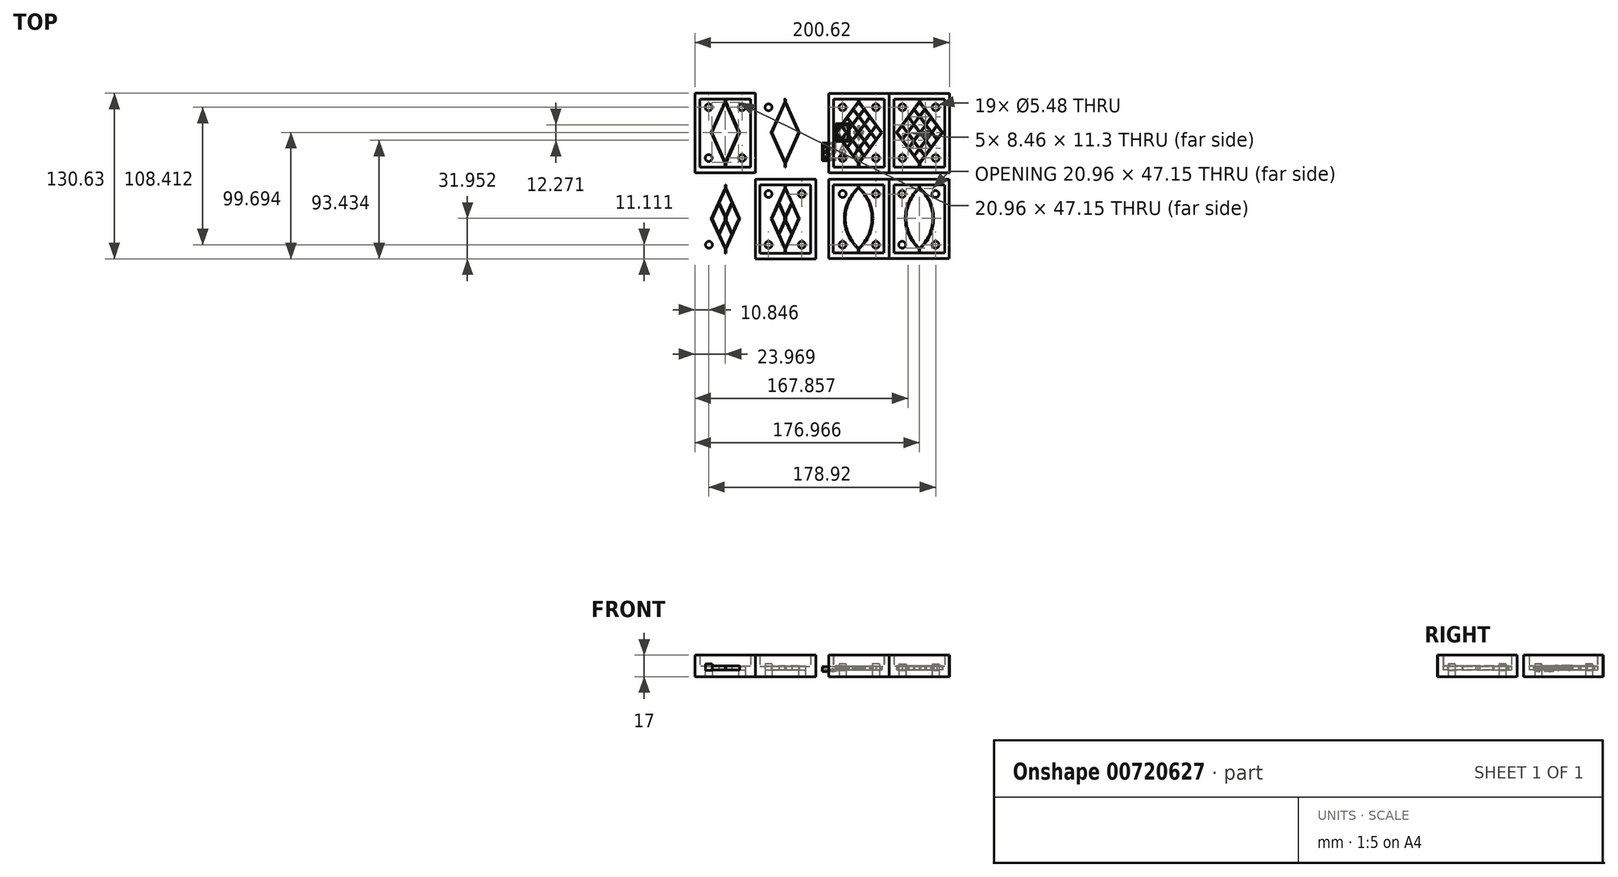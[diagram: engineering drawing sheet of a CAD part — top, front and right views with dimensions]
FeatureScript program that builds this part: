
annotation { "Feature Type Name" : "Feature", "Feature Type Description" : "" }
export const myFeature = defineFeature(function(context is Context, id is Id, definition is map)
    precondition{}
    {
        {
            var Q0;
            Q0=qCreatedBy(makeId("Top.planeOp"),FACE);
            var sketch = newSketch(context, id + "F0", { "sketchPlane" : qUnion([Q0])});
            skLineSegment(sketch, "E0.bottom", {"start": v(-19.96, 26.4) * mm, "end": v(20.09, 26.4) * mm});
            skLineSegment(sketch, "E0.top", {"start": v(-19.96, -27.38) * mm, "end": v(20.09, -27.38) * mm});
            skLineSegment(sketch, "E0.left", {"start": v(-19.96, 26.4) * mm, "end": v(-19.96, -27.38) * mm});
            skLineSegment(sketch, "E0.right", {"start": v(20.09, 26.4) * mm, "end": v(20.09, -27.38) * mm});
            skLineSegment(sketch, "E1.bottom", {"start": v(-23.57, 30.94) * mm, "end": v(23.97, 30.94) * mm});
            skLineSegment(sketch, "E1.top", {"start": v(-23.57, -31.82) * mm, "end": v(23.97, -31.82) * mm});
            skLineSegment(sketch, "E1.left", {"start": v(-23.57, 30.94) * mm, "end": v(-23.57, -31.82) * mm});
            skLineSegment(sketch, "E1.right", {"start": v(23.97, 30.94) * mm, "end": v(23.97, -31.82) * mm});
            skPoint(sketch, "E2.startSnap0", {"position": v(-19.96, -0.48) * mm});
            skLineSegment(sketch, "E3", {"start": v(-13.42, 5.65) * mm, "end": v(-9.19, 11.3) * mm});
            skLineSegment(sketch, "E4", {"start": v(-9.19, 11.3) * mm, "end": v(-5.32, 6.14) * mm});
            skLineSegment(sketch, "E5", {"start": v(-5.32, 6.14) * mm, "end": v(-9.55, 0.48) * mm});
            skLineSegment(sketch, "E6", {"start": v(-17.65, 0) * mm, "end": v(-13.78, 5.17) * mm});
            skLineSegment(sketch, "E7", {"start": v(0, 23.57) * mm, "end": v(-3.87, 18.4) * mm});
            skLineSegment(sketch, "E8", {"start": v(-4.23, 17.92) * mm, "end": v(-8.83, 11.79) * mm});
            skLineSegment(sketch, "E9", {"start": v(-13.78, -5.17) * mm, "end": v(-9.92, 0) * mm});
            skPoint(sketch, "E10.endSnap0", {"position": v(-4.96, 6.62) * mm});
            skLineSegment(sketch, "E11", {"start": v(0, 13.24) * mm, "end": v(3.87, 18.4) * mm});
            skLineSegment(sketch, "E12", {"start": v(-4.96, 6.62) * mm, "end": v(-0.36, 12.76) * mm});
            skLineSegment(sketch, "E13", {"start": v(-13.42, -5.65) * mm, "end": v(-9.55, -0.48) * mm});
            skLineSegment(sketch, "E14", {"start": v(-9.55, -0.48) * mm, "end": v(-5.32, -6.14) * mm});
            skLineSegment(sketch, "E15", {"start": v(-5.32, -6.14) * mm, "end": v(-9.19, -11.3) * mm});
            skLineSegment(sketch, "E16", {"start": v(-9.19, -11.3) * mm, "end": v(-13.42, -5.65) * mm});
            skLineSegment(sketch, "E17", {"start": v(-4.96, -5.65) * mm, "end": v(-0.73, 0) * mm});
            skLineSegment(sketch, "E18", {"start": v(-0.73, 0) * mm, "end": v(-4.96, 5.65) * mm});
            skLineSegment(sketch, "E19", {"start": v(-4.96, 5.65) * mm, "end": v(-9.19, 0) * mm});
            skLineSegment(sketch, "E20", {"start": v(-9.19, 0) * mm, "end": v(-4.96, -5.65) * mm});
            skLineSegment(sketch, "E21", {"start": v(4.23, 6.62) * mm, "end": v(0, 12.27) * mm});
            skLineSegment(sketch, "E22", {"start": v(0, 12.27) * mm, "end": v(-4.6, 6.14) * mm});
            skLineSegment(sketch, "E23", {"start": v(-4.6, 6.14) * mm, "end": v(-0.36, 0.48) * mm});
            skLineSegment(sketch, "E24", {"start": v(-0.36, 0.48) * mm, "end": v(4.23, 6.62) * mm});
            skLineSegment(sketch, "E25", {"start": v(4.6, 7.1) * mm, "end": v(8.46, 12.27) * mm});
            skLineSegment(sketch, "E26", {"start": v(8.46, 12.27) * mm, "end": v(4.23, 17.92) * mm});
            skLineSegment(sketch, "E27", {"start": v(4.23, 17.92) * mm, "end": v(0.36, 12.76) * mm});
            skLineSegment(sketch, "E28", {"start": v(0.36, 12.76) * mm, "end": v(4.6, 7.1) * mm});
            skLineSegment(sketch, "E29", {"start": v(-4.23, -17.92) * mm, "end": v(-0.36, -12.76) * mm});
            skLineSegment(sketch, "E30", {"start": v(-0.36, -12.76) * mm, "end": v(-4.96, -6.62) * mm});
            skLineSegment(sketch, "E31", {"start": v(-8.83, -11.79) * mm, "end": v(-4.96, -6.62) * mm});
            skLineSegment(sketch, "E32", {"start": v(-8.83, -11.79) * mm, "end": v(-4.23, -17.92) * mm});
            skLineSegment(sketch, "E33", {"start": v(0, -12.27) * mm, "end": v(-4.6, -6.14) * mm});
            skLineSegment(sketch, "E34", {"start": v(-0.36, -0.48) * mm, "end": v(-4.6, -6.14) * mm});
            skLineSegment(sketch, "E35", {"start": v(4.23, -6.62) * mm, "end": v(-0.36, -0.48) * mm});
            skLineSegment(sketch, "E36", {"start": v(4.23, -6.62) * mm, "end": v(0, -12.27) * mm});
            skLineSegment(sketch, "E37", {"start": v(9.19, 0) * mm, "end": v(4.6, 6.14) * mm});
            skLineSegment(sketch, "E38", {"start": v(4.6, 6.14) * mm, "end": v(0, 0) * mm});
            skLineSegment(sketch, "E39", {"start": v(0, 0) * mm, "end": v(4.6, -6.14) * mm});
            skLineSegment(sketch, "E40", {"start": v(4.6, -6.14) * mm, "end": v(9.19, 0) * mm});
            skLineSegment(sketch, "E41", {"start": v(4.96, 6.62) * mm, "end": v(8.83, 11.79) * mm});
            skLineSegment(sketch, "E42", {"start": v(8.83, 11.79) * mm, "end": v(13.42, 5.65) * mm});
            skLineSegment(sketch, "E43", {"start": v(13.42, 5.65) * mm, "end": v(9.55, 0.48) * mm});
            skLineSegment(sketch, "E44", {"start": v(9.55, 0.48) * mm, "end": v(4.96, 6.62) * mm});
            skLineSegment(sketch, "E45", {"start": v(-3.87, -18.4) * mm, "end": v(0, -13.24) * mm});
            skLineSegment(sketch, "E46", {"start": v(0, -13.24) * mm, "end": v(3.87, -18.4) * mm});
            skLineSegment(sketch, "E47", {"start": v(3.87, -18.4) * mm, "end": v(0, -23.57) * mm});
            skLineSegment(sketch, "E48", {"start": v(0, -23.57) * mm, "end": v(-3.87, -18.4) * mm});
            skLineSegment(sketch, "E49", {"start": v(4.23, -17.92) * mm, "end": v(8.46, -12.27) * mm});
            skLineSegment(sketch, "E50", {"start": v(8.46, -12.27) * mm, "end": v(4.6, -7.1) * mm});
            skLineSegment(sketch, "E51", {"start": v(4.6, -7.1) * mm, "end": v(0.36, -12.76) * mm});
            skLineSegment(sketch, "E52", {"start": v(0.36, -12.76) * mm, "end": v(4.23, -17.92) * mm});
            skLineSegment(sketch, "E53", {"start": v(8.83, -11.79) * mm, "end": v(4.96, -6.62) * mm});
            skLineSegment(sketch, "E54", {"start": v(4.96, -6.62) * mm, "end": v(9.55, -0.48) * mm});
            skLineSegment(sketch, "E55", {"start": v(9.55, -0.48) * mm, "end": v(13.42, -5.65) * mm});
            skLineSegment(sketch, "E56", {"start": v(13.42, -5.65) * mm, "end": v(8.83, -11.79) * mm});
            skLineSegment(sketch, "E57", {"start": v(17.65, 0) * mm, "end": v(13.78, 5.17) * mm});
            skLineSegment(sketch, "E58", {"start": v(13.78, 5.17) * mm, "end": v(9.92, 0) * mm});
            skLineSegment(sketch, "E59", {"start": v(9.92, 0) * mm, "end": v(13.78, -5.17) * mm});
            skLineSegment(sketch, "E60", {"start": v(13.78, -5.17) * mm, "end": v(17.65, 0) * mm});
            skLineSegment(sketch, "E61", {"start": v(0, 13.24) * mm, "end": v(-3.87, 18.4) * mm});
            skLineSegment(sketch, "E62", {"start": v(3.87, 18.4) * mm, "end": v(0, 23.57) * mm});
            skLineSegment(sketch, "E63", {"start": v(-0.36, 12.76) * mm, "end": v(-4.23, 17.92) * mm});
            skLineSegment(sketch, "E64", {"start": v(-13.78, -5.17) * mm, "end": v(-17.65, 0) * mm});
            skLineSegment(sketch, "E65", {"start": v(-9.92, 0) * mm, "end": v(-13.78, 5.17) * mm});
            skLineSegment(sketch, "E66", {"start": v(-9.55, 0.48) * mm, "end": v(-13.42, 5.65) * mm});
            skLineSegment(sketch, "E67", {"start": v(-4.96, 6.62) * mm, "end": v(-8.83, 11.79) * mm});
            skLineSegment(sketch, "E68", {"start": v(0.36, 24.06) * mm, "end": v(18.38, 0) * mm});
            skLineSegment(sketch, "E69", {"start": v(-18.38, 0) * mm, "end": v(-0.36, 24.06) * mm});
            skLineSegment(sketch, "E70.MirrorCS", {"start": v(-18.38, 0) * mm, "end": v(-0.36, -24.06) * mm});
            skLineSegment(sketch, "E71.MirrorCS", {"start": v(0.36, -24.06) * mm, "end": v(18.38, 0) * mm});
            skLineSegment(sketch, "E72", {"start": v(-0.36, -24.06) * mm, "end": v(-0.36, -27.38) * mm});
            skLineSegment(sketch, "E73", {"start": v(0.36, -24.06) * mm, "end": v(0.36, -27.38) * mm});
            skLineSegment(sketch, "E74", {"start": v(-0.36, 24.06) * mm, "end": v(-0.36, 26.4) * mm});
            skLineSegment(sketch, "E75", {"start": v(0.36, 24.06) * mm, "end": v(0.36, 26.4) * mm});
            skLineSegment(sketch, "E76.bottom", {"start": v(-77.96, 26.53) * mm, "end": v(-37.9, 26.53) * mm});
            skLineSegment(sketch, "E76.top", {"start": v(-77.96, -27.25) * mm, "end": v(-37.9, -27.25) * mm});
            skLineSegment(sketch, "E76.left", {"start": v(-77.96, 26.53) * mm, "end": v(-77.96, -27.25) * mm});
            skLineSegment(sketch, "E76.right", {"start": v(-37.9, 26.53) * mm, "end": v(-37.9, -27.25) * mm});
            skLineSegment(sketch, "E77.bottom", {"start": v(-81.56, 31.06) * mm, "end": v(-34.02, 31.06) * mm});
            skLineSegment(sketch, "E77.top", {"start": v(-81.56, -31.7) * mm, "end": v(-34.02, -31.7) * mm});
            skLineSegment(sketch, "E77.left", {"start": v(-81.56, 31.06) * mm, "end": v(-81.56, -31.7) * mm});
            skLineSegment(sketch, "E77.right", {"start": v(-34.02, 31.06) * mm, "end": v(-34.02, -31.7) * mm});
            skPoint(sketch, "E78.startSnap0", {"position": v(-77.96, -0.36) * mm});
            skLineSegment(sketch, "E79.MirrorCS", {"start": v(-69.2, -0.05) * mm, "end": v(-58.36, -23.93) * mm});
            skLineSegment(sketch, "E80", {"start": v(-58.36, -23.93) * mm, "end": v(-58.36, -27.25) * mm});
            skLineSegment(sketch, "E81", {"start": v(-57.63, -23.93) * mm, "end": v(-57.63, -27.25) * mm});
            skLineSegment(sketch, "E82", {"start": v(-58.36, 24.18) * mm, "end": v(-58.36, 26.53) * mm});
            skLineSegment(sketch, "E83", {"start": v(-57.63, 24.18) * mm, "end": v(-57.63, 26.53) * mm});
            skCircle(sketch, "E84", {"center": v(-71.12, 19.95) * mm, "radius": 2.74 * mm});
            skLineSegment(sketch, "E85", {"start": v(-69.2, -0.05) * mm, "end": v(-58.36, 24.18) * mm});
            skLineSegment(sketch, "E86.MirrorCS", {"start": v(-46.79, -0.05) * mm, "end": v(-57.63, 24.18) * mm});
            skLineSegment(sketch, "E87.MirrorCS", {"start": v(-47.52, -0.05) * mm, "end": v(-58, 23.7) * mm});
            skLineSegment(sketch, "E88.MirrorCS", {"start": v(-46.79, -0.05) * mm, "end": v(-57.63, -23.93) * mm});
            skLineSegment(sketch, "E89.MirrorCS", {"start": v(-47.52, -0.05) * mm, "end": v(-58, -23.45) * mm});
            skLineSegment(sketch, "E90.MirrorCS", {"start": v(-68.47, -0.05) * mm, "end": v(-58, 23.7) * mm});
            skLineSegment(sketch, "E91.MirrorCS", {"start": v(-68.47, -0.05) * mm, "end": v(-58, -23.45) * mm});
            skLineSegment(sketch, "E92.bottom", {"start": v(-77.85, -41.34) * mm, "end": v(-37.8, -41.34) * mm});
            skLineSegment(sketch, "E92.top", {"start": v(-77.85, -95.12) * mm, "end": v(-37.8, -95.12) * mm});
            skLineSegment(sketch, "E92.left", {"start": v(-77.85, -41.34) * mm, "end": v(-77.85, -95.12) * mm});
            skLineSegment(sketch, "E92.right", {"start": v(-37.8, -41.34) * mm, "end": v(-37.8, -95.12) * mm});
            skLineSegment(sketch, "E93.bottom", {"start": v(-81.46, -36.8) * mm, "end": v(-33.91, -36.8) * mm});
            skLineSegment(sketch, "E93.top", {"start": v(-81.46, -99.57) * mm, "end": v(-33.91, -99.57) * mm});
            skLineSegment(sketch, "E93.left", {"start": v(-81.46, -36.8) * mm, "end": v(-81.46, -99.57) * mm});
            skLineSegment(sketch, "E93.right", {"start": v(-33.91, -36.8) * mm, "end": v(-33.91, -99.57) * mm});
            skPoint(sketch, "E94.startSnap0", {"position": v(-77.85, -68.23) * mm});
            skLineSegment(sketch, "E95.MirrorCS", {"start": v(-69.1, -67.93) * mm, "end": v(-58.25, -91.8) * mm});
            skLineSegment(sketch, "E96", {"start": v(-58.25, -91.8) * mm, "end": v(-58.25, -95.12) * mm});
            skLineSegment(sketch, "E97", {"start": v(-57.52, -91.8) * mm, "end": v(-57.52, -95.12) * mm});
            skLineSegment(sketch, "E98", {"start": v(-58.25, -43.69) * mm, "end": v(-58.25, -41.34) * mm});
            skLineSegment(sketch, "E99", {"start": v(-57.52, -43.69) * mm, "end": v(-57.52, -41.34) * mm});
            skLineSegment(sketch, "E100", {"start": v(-69.1, -67.93) * mm, "end": v(-58.25, -43.69) * mm});
            skLineSegment(sketch, "E101.MirrorCS", {"start": v(-46.68, -67.93) * mm, "end": v(-57.52, -43.69) * mm});
            skLineSegment(sketch, "E102.MirrorCS", {"start": v(-46.68, -67.93) * mm, "end": v(-57.52, -91.8) * mm});
            skLineSegment(sketch, "E103", {"start": v(-57.89, -66.3) * mm, "end": v(-52.97, -55.31) * mm});
            skLineSegment(sketch, "E104", {"start": v(-57.89, -66.3) * mm, "end": v(-62.8, -55.31) * mm});
            skLineSegment(sketch, "E105", {"start": v(-52.65, -56.05) * mm, "end": v(-47.4, -67.93) * mm});
            skLineSegment(sketch, "E106", {"start": v(-63.13, -56.05) * mm, "end": v(-68.37, -67.93) * mm});
            skLineSegment(sketch, "E107", {"start": v(-57.89, -91.32) * mm, "end": v(-62.8, -80.35) * mm});
            skLineSegment(sketch, "E108", {"start": v(-62.8, -80.35) * mm, "end": v(-57.89, -69.52) * mm});
            skLineSegment(sketch, "E109", {"start": v(-57.89, -69.52) * mm, "end": v(-52.97, -80.35) * mm});
            skLineSegment(sketch, "E110", {"start": v(-52.97, -80.35) * mm, "end": v(-58, -91.59) * mm});
            skLineSegment(sketch, "E111", {"start": v(-68.37, -67.93) * mm, "end": v(-63.13, -79.62) * mm});
            skLineSegment(sketch, "E112", {"start": v(-52.65, -79.62) * mm, "end": v(-47.4, -67.93) * mm});
            skLineSegment(sketch, "E113.left", {"start": v(-57.2, -66.3) * mm, "end": v(-57.2, -69.37) * mm});
            skLineSegment(sketch, "E113.right", {"start": v(-58.57, -66.3) * mm, "end": v(-58.57, -69.37) * mm});
            skLineSegment(sketch, "E114", {"start": v(-63.13, -56.05) * mm, "end": v(-58.57, -66.3) * mm});
            skLineSegment(sketch, "E115", {"start": v(-57.2, -66.3) * mm, "end": v(-52.65, -56.05) * mm});
            skLineSegment(sketch, "E116", {"start": v(-57.2, -69.37) * mm, "end": v(-52.65, -79.62) * mm});
            skLineSegment(sketch, "E117", {"start": v(-58.57, -69.37) * mm, "end": v(-63.13, -79.62) * mm});
            skLineSegment(sketch, "E118.bottom", {"start": v(-20.04, -41.21) * mm, "end": v(20, -41.21) * mm});
            skLineSegment(sketch, "E118.top", {"start": v(-20.04, -95) * mm, "end": v(20, -95) * mm});
            skLineSegment(sketch, "E118.left", {"start": v(-20.04, -41.21) * mm, "end": v(-20.04, -95) * mm});
            skLineSegment(sketch, "E118.right", {"start": v(20, -41.21) * mm, "end": v(20, -95) * mm});
            skLineSegment(sketch, "E119.bottom", {"start": v(-23.65, -36.68) * mm, "end": v(23.9, -36.68) * mm});
            skLineSegment(sketch, "E119.top", {"start": v(-23.65, -99.44) * mm, "end": v(23.9, -99.44) * mm});
            skLineSegment(sketch, "E119.left", {"start": v(-23.65, -36.68) * mm, "end": v(-23.65, -99.44) * mm});
            skLineSegment(sketch, "E119.right", {"start": v(23.9, -36.68) * mm, "end": v(23.9, -99.44) * mm});
            skPoint(sketch, "E120.startSnap0", {"position": v(-20.04, -68.1) * mm});
            skLineSegment(sketch, "E121", {"start": v(-0.44, -91.68) * mm, "end": v(-0.44, -95) * mm});
            skLineSegment(sketch, "E122", {"start": v(0.28, -91.68) * mm, "end": v(0.28, -95) * mm});
            skLineSegment(sketch, "E123", {"start": v(-0.44, -43.56) * mm, "end": v(-0.44, -41.21) * mm});
            skLineSegment(sketch, "E124", {"start": v(0.28, -43.56) * mm, "end": v(0.28, -41.21) * mm});
            skArc(sketch, "E125", {"start": v(-0.44, -43.56) * mm, "mid": v(-11.29, -67.62) * mm, "end": v(-0.44, -91.68) * mm});
            skArc(sketch, "E126", {"start": v(-0.08, -44.04) * mm, "mid": v(-10.56, -67.62) * mm, "end": v(-0.08, -91.2) * mm});
            skArc(sketch, "E127", {"start": v(0.28, -91.68) * mm, "mid": v(11.12, -67.62) * mm, "end": v(0.28, -43.56) * mm});
            skArc(sketch, "E128", {"start": v(-0.08, -91.2) * mm, "mid": v(10.4, -67.62) * mm, "end": v(-0.08, -44.04) * mm});
            skCircle(sketch, "E129.MirrorC", {"center": v(-44.87, 19.95) * mm, "radius": 2.74 * mm});
            skCircle(sketch, "E130.MirrorC", {"center": v(-71.12, -20.06) * mm, "radius": 2.74 * mm});
            skCircle(sketch, "E131.MirrorC", {"center": v(-44.87, -20.06) * mm, "radius": 2.74 * mm});
            skCircle(sketch, "E132.MirrorC", {"center": v(-12.72, 19.95) * mm, "radius": 2.74 * mm});
            skCircle(sketch, "E133.MirrorC", {"center": v(-12.72, -20.06) * mm, "radius": 2.74 * mm});
            skCircle(sketch, "E134.MirrorC", {"center": v(13.53, -20.06) * mm, "radius": 2.74 * mm});
            skCircle(sketch, "E135.MirrorC", {"center": v(13.53, 19.95) * mm, "radius": 2.74 * mm});
            skCircle(sketch, "E136.MirrorC", {"center": v(-44.87, -48.45) * mm, "radius": 2.74 * mm});
            skCircle(sketch, "E137.MirrorC", {"center": v(-71.12, -48.45) * mm, "radius": 2.74 * mm});
            skCircle(sketch, "E138.MirrorC", {"center": v(-71.12, -88.46) * mm, "radius": 2.74 * mm});
            skCircle(sketch, "E139.MirrorC", {"center": v(-44.87, -88.46) * mm, "radius": 2.74 * mm});
            skCircle(sketch, "E140.MirrorC", {"center": v(-12.72, -48.45) * mm, "radius": 2.74 * mm});
            skCircle(sketch, "E141.MirrorC", {"center": v(13.53, -48.45) * mm, "radius": 2.74 * mm});
            skCircle(sketch, "E142.MirrorC", {"center": v(13.53, -88.46) * mm, "radius": 2.74 * mm});
            skCircle(sketch, "E143.MirrorC", {"center": v(-12.72, -88.46) * mm, "radius": 2.74 * mm});
            skLineSegment(sketch, "E144", {"start": v(-57.89, -44.49) * mm, "end": v(-52.97, -55.31) * mm});
            skLineSegment(sketch, "E145", {"start": v(-57.89, -44.49) * mm, "end": v(-62.8, -55.31) * mm});
            skSolve(sketch);
        }
        {
            var Q0;
            Q0=makeQuery(id+"F0.imprint","IMPRINT",FACE,{"disambiguationData":[TD([[makeQuery(id+"F0.imprint","IMPRINT",EDGE,{"derivedFrom":sQuery(id+"F0.wireOp",EDGE,"E3")}),1.0]])]});
            var Q1;
            Q1=makeQuery(id+"F0.imprint","IMPRINT",FACE,{"disambiguationData":[TD([[makeQuery(id+"F0.imprint","IMPRINT",EDGE,{"derivedFrom":sQuery(id+"F0.wireOp",EDGE,"E79.MirrorCS")}),1.0]])]});
            var Q2;
            {var subQ1=sQuery(id+"F0.wireOp",EDGE,"E121");Q2=makeQuery(id+"F0.imprint","IMPRINT",FACE,{"disambiguationData":[TD([[makeQuery(id+"F0.imprint","IMPRINT",EDGE,{"derivedFrom":subQ1}),1.0]])]});}
            var Q3;
            Q3=makeQuery(id+"F0.imprint","IMPRINT",FACE,{"disambiguationData":[TD([[makeQuery(id+"F0.imprint","IMPRINT",EDGE,{"derivedFrom":sQuery(id+"F0.wireOp",EDGE,"E95.MirrorCS")}),1.0]])]});
            extrude(context, id + "F1", {"entities" : qUnion([Q0, Q1, Q2, Q3]), "depth" : .3 * mm, "offsetDistance" : 25 * mm});
        }
        {
            var Q0;
            Q0=makeQuery(id+"F0.imprint","IMPRINT",FACE,{"disambiguationData":[TD([[makeQuery(id+"F0.imprint","IMPRINT",EDGE,{"derivedFrom":sQuery(id+"F0.wireOp",EDGE,"E0.bottom")}),1.0]])]});
            var Q1;
            Q1=makeQuery(id+"F0.imprint","IMPRINT",FACE,{"disambiguationData":[TD([[makeQuery(id+"F0.imprint","IMPRINT",EDGE,{"derivedFrom":sQuery(id+"F0.wireOp",EDGE,"W2vNM0GE-2OHP-QNdi-PDCA-W7E0gAEi5RRH")}),1.0]])]});
            var Q2;
            Q2=makeQuery(id+"F0.imprint","IMPRINT",FACE,{"disambiguationData":[TD([[makeQuery(id+"F0.imprint","IMPRINT",EDGE,{"derivedFrom":sQuery(id+"F0.wireOp",EDGE,"edaaeaec-2fa2-4ac8-96e5-24b6cc5294a60.MirrorC")}),-1.0]])]});
            var Q3;
            Q3=makeQuery(id+"F0.imprint","IMPRINT",FACE,{"disambiguationData":[TD([[makeQuery(id+"F0.imprint","IMPRINT",EDGE,{"derivedFrom":sQuery(id+"F0.wireOp",EDGE,"8cd1bf5f-9e5d-4626-ba93-0b63d8eae1ea0.MirrorC")}),-1.0]])]});
            var Q4;
            Q4=makeQuery(id+"F0.imprint","IMPRINT",FACE,{"disambiguationData":[TD([[makeQuery(id+"F0.imprint","IMPRINT",EDGE,{"derivedFrom":sQuery(id+"F0.wireOp",EDGE,"899422d1-b2af-4982-8523-cbcbc75a0b1b.MirrorC")}),-1.0]])]});
            var Q5;
            {var subQ1=sQuery(id+"F0.wireOp",EDGE,"E76.left");Q5=makeQuery(id+"F0.imprint","IMPRINT",FACE,{"disambiguationData":[TD([[makeQuery(id+"F0.imprint","IMPRINT",EDGE,{"derivedFrom":subQ1}),-1.0]])]});}
            var Q6;
            Q6=makeQuery(id+"F0.imprint","IMPRINT",FACE,{"disambiguationData":[TD([[makeQuery(id+"F0.imprint","IMPRINT",EDGE,{"derivedFrom":sQuery(id+"F0.wireOp",EDGE,"79d72fee-5c57-43ab-89ce-cfacb674b62a")}),1.0]])]});
            var Q7;
            Q7=makeQuery(id+"F0.imprint","IMPRINT",FACE,{"disambiguationData":[TD([[makeQuery(id+"F0.imprint","IMPRINT",EDGE,{"derivedFrom":sQuery(id+"F0.wireOp",EDGE,"ed612093-3e78-479f-b3c7-dd08aea9376b.MirrorC")}),-1.0]])]});
            var Q8;
            {var subQ1=sQuery(id+"F0.wireOp",EDGE,"E92.left");Q8=makeQuery(id+"F0.imprint","IMPRINT",FACE,{"disambiguationData":[TD([[makeQuery(id+"F0.imprint","IMPRINT",EDGE,{"derivedFrom":subQ1}),-1.0]])]});}
            var Q9;
            {var subQ1=sQuery(id+"F0.wireOp",EDGE,"E118.left");Q9=makeQuery(id+"F0.imprint","IMPRINT",FACE,{"disambiguationData":[TD([[makeQuery(id+"F0.imprint","IMPRINT",EDGE,{"derivedFrom":subQ1}),-1.0]])]});}
            var Q10;
            Q10=makeQuery(id+"F0.imprint","IMPRINT",FACE,{"disambiguationData":[TD([[makeQuery(id+"F0.imprint","IMPRINT",EDGE,{"derivedFrom":sQuery(id+"F0.wireOp",EDGE,"052349c2-b7bf-4fa4-ab4a-60abaacbaca7")}),1.0]])]});
            var Q11;
            Q11=makeQuery(id+"F0.imprint","IMPRINT",FACE,{"disambiguationData":[TD([[makeQuery(id+"F0.imprint","IMPRINT",EDGE,{"derivedFrom":sQuery(id+"F0.wireOp",EDGE,"c45039b2-2c3b-486d-bf61-685492c25083.MirrorC")}),-1.0]])]});
            extrude(context, id + "F2", {"entities" : qUnion([Q0, Q1, Q2, Q3, Q4, Q5, Q6, Q7, Q8, Q9, Q10, Q11]), "depth" : 12 * mm, "offsetDistance" : 25 * mm});
        }
        {
            var Q0;
            {var subQ0=sQuery(id+"F0.wireOp",EDGE,"E0.left");Q0=makeQuery(id+"F0.imprint","IMPRINT",FACE,{"disambiguationData":[TD([[makeQuery(id+"F0.imprint","IMPRINT",EDGE,{"derivedFrom":subQ0}),1.0]])]});}
            var Q1;
            {var subQ0=sQuery(id+"F0.wireOp",EDGE,"E0.right");Q1=makeQuery(id+"F0.imprint","IMPRINT",FACE,{"disambiguationData":[TD([[makeQuery(id+"F0.imprint","IMPRINT",EDGE,{"derivedFrom":subQ0}),-1.0]])]});}
            var Q2;
            Q2=makeQuery(id+"F1.opExtrude","CAP_FACE",FACE,{"disambiguationData":[OSD([sQuery(id+"F0.wireOp",EDGE,"E0.bottom"),sQuery(id+"F0.wireOp",EDGE,"E0.top"),sQuery(id+"F0.wireOp",EDGE,"E3"),sQuery(id+"F0.wireOp",EDGE,"E4"),sQuery(id+"F0.wireOp",EDGE,"E5"),sQuery(id+"F0.wireOp",EDGE,"E6"),sQuery(id+"F0.wireOp",EDGE,"E7"),sQuery(id+"F0.wireOp",EDGE,"E8"),sQuery(id+"F0.wireOp",EDGE,"E9"),sQuery(id+"F0.wireOp",EDGE,"E11"),sQuery(id+"F0.wireOp",EDGE,"E12"),sQuery(id+"F0.wireOp",EDGE,"E13"),sQuery(id+"F0.wireOp",EDGE,"E14"),sQuery(id+"F0.wireOp",EDGE,"E15"),sQuery(id+"F0.wireOp",EDGE,"E16"),sQuery(id+"F0.wireOp",EDGE,"E17"),sQuery(id+"F0.wireOp",EDGE,"E18"),sQuery(id+"F0.wireOp",EDGE,"E19"),sQuery(id+"F0.wireOp",EDGE,"E20"),sQuery(id+"F0.wireOp",EDGE,"E21"),sQuery(id+"F0.wireOp",EDGE,"E22"),sQuery(id+"F0.wireOp",EDGE,"E23"),sQuery(id+"F0.wireOp",EDGE,"E24"),sQuery(id+"F0.wireOp",EDGE,"E25"),sQuery(id+"F0.wireOp",EDGE,"E26"),sQuery(id+"F0.wireOp",EDGE,"E27"),sQuery(id+"F0.wireOp",EDGE,"E28"),sQuery(id+"F0.wireOp",EDGE,"E29"),sQuery(id+"F0.wireOp",EDGE,"E30"),sQuery(id+"F0.wireOp",EDGE,"E31"),sQuery(id+"F0.wireOp",EDGE,"E32"),sQuery(id+"F0.wireOp",EDGE,"E33"),sQuery(id+"F0.wireOp",EDGE,"E34"),sQuery(id+"F0.wireOp",EDGE,"E35"),sQuery(id+"F0.wireOp",EDGE,"E36"),sQuery(id+"F0.wireOp",EDGE,"E37"),sQuery(id+"F0.wireOp",EDGE,"E38"),sQuery(id+"F0.wireOp",EDGE,"E39"),sQuery(id+"F0.wireOp",EDGE,"E40"),sQuery(id+"F0.wireOp",EDGE,"E41"),sQuery(id+"F0.wireOp",EDGE,"E42"),sQuery(id+"F0.wireOp",EDGE,"E43"),sQuery(id+"F0.wireOp",EDGE,"E44"),sQuery(id+"F0.wireOp",EDGE,"E45"),sQuery(id+"F0.wireOp",EDGE,"E46"),sQuery(id+"F0.wireOp",EDGE,"E47"),sQuery(id+"F0.wireOp",EDGE,"E48"),sQuery(id+"F0.wireOp",EDGE,"E49"),sQuery(id+"F0.wireOp",EDGE,"E50"),sQuery(id+"F0.wireOp",EDGE,"E51"),sQuery(id+"F0.wireOp",EDGE,"E52"),sQuery(id+"F0.wireOp",EDGE,"E53"),sQuery(id+"F0.wireOp",EDGE,"E54"),sQuery(id+"F0.wireOp",EDGE,"E55"),sQuery(id+"F0.wireOp",EDGE,"E56"),sQuery(id+"F0.wireOp",EDGE,"E57"),sQuery(id+"F0.wireOp",EDGE,"E58"),sQuery(id+"F0.wireOp",EDGE,"E59"),sQuery(id+"F0.wireOp",EDGE,"E60"),sQuery(id+"F0.wireOp",EDGE,"E61"),sQuery(id+"F0.wireOp",EDGE,"E62"),sQuery(id+"F0.wireOp",EDGE,"E63"),sQuery(id+"F0.wireOp",EDGE,"E64"),sQuery(id+"F0.wireOp",EDGE,"E65"),sQuery(id+"F0.wireOp",EDGE,"E66"),sQuery(id+"F0.wireOp",EDGE,"E67"),sQuery(id+"F0.wireOp",EDGE,"E68"),sQuery(id+"F0.wireOp",EDGE,"E69"),sQuery(id+"F0.wireOp",EDGE,"E70.MirrorCS"),sQuery(id+"F0.wireOp",EDGE,"E71.MirrorCS"),sQuery(id+"F0.wireOp",EDGE,"E72"),sQuery(id+"F0.wireOp",EDGE,"E73"),sQuery(id+"F0.wireOp",EDGE,"E74"),sQuery(id+"F0.wireOp",EDGE,"E75")])],"isStart":false});
            var Q3;
            Q3=makeQuery(id+"F0.imprint","IMPRINT",FACE,{"disambiguationData":[TD([[makeQuery(id+"F0.imprint","IMPRINT",EDGE,{"derivedFrom":sQuery(id+"F0.wireOp",EDGE,"E45")}),-1.0]])]});
            var Q4;
            Q4=makeQuery(id+"F0.imprint","IMPRINT",FACE,{"disambiguationData":[TD([[makeQuery(id+"F0.imprint","IMPRINT",EDGE,{"derivedFrom":sQuery(id+"F0.wireOp",EDGE,"E49")}),1.0]])]});
            var Q5;
            Q5=makeQuery(id+"F0.imprint","IMPRINT",FACE,{"disambiguationData":[TD([[makeQuery(id+"F0.imprint","IMPRINT",EDGE,{"derivedFrom":sQuery(id+"F0.wireOp",EDGE,"E33")}),-1.0]])]});
            var Q6;
            Q6=makeQuery(id+"F0.imprint","IMPRINT",FACE,{"disambiguationData":[TD([[makeQuery(id+"F0.imprint","IMPRINT",EDGE,{"derivedFrom":sQuery(id+"F0.wireOp",EDGE,"E29")}),1.0]])]});
            var Q7;
            Q7=makeQuery(id+"F0.imprint","IMPRINT",FACE,{"disambiguationData":[TD([[makeQuery(id+"F0.imprint","IMPRINT",EDGE,{"derivedFrom":sQuery(id+"F0.wireOp",EDGE,"E13")}),-1.0]])]});
            var Q8;
            Q8=makeQuery(id+"F0.imprint","IMPRINT",FACE,{"disambiguationData":[TD([[makeQuery(id+"F0.imprint","IMPRINT",EDGE,{"derivedFrom":sQuery(id+"F0.wireOp",EDGE,"E17")}),1.0]])]});
            var Q9;
            Q9=makeQuery(id+"F0.imprint","IMPRINT",FACE,{"disambiguationData":[TD([[makeQuery(id+"F0.imprint","IMPRINT",EDGE,{"derivedFrom":sQuery(id+"F0.wireOp",EDGE,"E6")}),-1.0]])]});
            var Q10;
            Q10=makeQuery(id+"F0.imprint","IMPRINT",FACE,{"disambiguationData":[TD([[makeQuery(id+"F0.imprint","IMPRINT",EDGE,{"derivedFrom":sQuery(id+"F0.wireOp",EDGE,"E3")}),-1.0]])]});
            var Q11;
            Q11=makeQuery(id+"F0.imprint","IMPRINT",FACE,{"disambiguationData":[TD([[makeQuery(id+"F0.imprint","IMPRINT",EDGE,{"derivedFrom":sQuery(id+"F0.wireOp",EDGE,"E8")}),1.0]])]});
            var Q12;
            Q12=makeQuery(id+"F0.imprint","IMPRINT",FACE,{"disambiguationData":[TD([[makeQuery(id+"F0.imprint","IMPRINT",EDGE,{"derivedFrom":sQuery(id+"F0.wireOp",EDGE,"E7")}),1.0]])]});
            var Q13;
            Q13=makeQuery(id+"F0.imprint","IMPRINT",FACE,{"disambiguationData":[TD([[makeQuery(id+"F0.imprint","IMPRINT",EDGE,{"derivedFrom":sQuery(id+"F0.wireOp",EDGE,"E25")}),1.0]])]});
            var Q14;
            Q14=makeQuery(id+"F0.imprint","IMPRINT",FACE,{"disambiguationData":[TD([[makeQuery(id+"F0.imprint","IMPRINT",EDGE,{"derivedFrom":sQuery(id+"F0.wireOp",EDGE,"E21")}),1.0]])]});
            var Q15;
            Q15=makeQuery(id+"F0.imprint","IMPRINT",FACE,{"disambiguationData":[TD([[makeQuery(id+"F0.imprint","IMPRINT",EDGE,{"derivedFrom":sQuery(id+"F0.wireOp",EDGE,"E37")}),1.0]])]});
            var Q16;
            Q16=makeQuery(id+"F0.imprint","IMPRINT",FACE,{"disambiguationData":[TD([[makeQuery(id+"F0.imprint","IMPRINT",EDGE,{"derivedFrom":sQuery(id+"F0.wireOp",EDGE,"E41")}),-1.0]])]});
            var Q17;
            Q17=makeQuery(id+"F0.imprint","IMPRINT",FACE,{"disambiguationData":[TD([[makeQuery(id+"F0.imprint","IMPRINT",EDGE,{"derivedFrom":sQuery(id+"F0.wireOp",EDGE,"E57")}),1.0]])]});
            var Q18;
            Q18=makeQuery(id+"F0.imprint","IMPRINT",FACE,{"disambiguationData":[TD([[makeQuery(id+"F0.imprint","IMPRINT",EDGE,{"derivedFrom":sQuery(id+"F0.wireOp",EDGE,"E53")}),-1.0]])]});
            var Q19;
            {var subQ0=sQuery(id+"F0.wireOp",EDGE,"E76.left");Q19=makeQuery(id+"F0.imprint","IMPRINT",FACE,{"disambiguationData":[TD([[makeQuery(id+"F0.imprint","IMPRINT",EDGE,{"derivedFrom":subQ0}),1.0]])]});}
            var Q20;
            {var subQ1=sQuery(id+"F0.wireOp",EDGE,"E76.right");Q20=makeQuery(id+"F0.imprint","IMPRINT",FACE,{"disambiguationData":[TD([[makeQuery(id+"F0.imprint","IMPRINT",EDGE,{"derivedFrom":subQ1}),-1.0]])]});}
            var Q21;
            Q21=makeQuery(id+"F0.imprint","IMPRINT",FACE,{"disambiguationData":[TD([[makeQuery(id+"F0.imprint","IMPRINT",EDGE,{"derivedFrom":sQuery(id+"F0.wireOp",EDGE,"E87.MirrorCS")}),1.0]])]});
            var Q22;
            Q22=makeQuery(id+"F1.opExtrude","CAP_FACE",FACE,{"disambiguationData":[OSD([sQuery(id+"F0.wireOp",EDGE,"E76.bottom"),sQuery(id+"F0.wireOp",EDGE,"E76.top"),sQuery(id+"F0.wireOp",EDGE,"E79.MirrorCS"),sQuery(id+"F0.wireOp",EDGE,"E80"),sQuery(id+"F0.wireOp",EDGE,"E81"),sQuery(id+"F0.wireOp",EDGE,"E82"),sQuery(id+"F0.wireOp",EDGE,"E83"),sQuery(id+"F0.wireOp",EDGE,"E85"),sQuery(id+"F0.wireOp",EDGE,"E86.MirrorCS"),sQuery(id+"F0.wireOp",EDGE,"E87.MirrorCS"),sQuery(id+"F0.wireOp",EDGE,"E88.MirrorCS"),sQuery(id+"F0.wireOp",EDGE,"E89.MirrorCS"),sQuery(id+"F0.wireOp",EDGE,"E90.MirrorCS"),sQuery(id+"F0.wireOp",EDGE,"E91.MirrorCS")])],"isStart":false});
            var Q23;
            {var subQ0=sQuery(id+"F0.wireOp",EDGE,"E92.left");Q23=makeQuery(id+"F0.imprint","IMPRINT",FACE,{"disambiguationData":[TD([[makeQuery(id+"F0.imprint","IMPRINT",EDGE,{"derivedFrom":subQ0}),1.0]])]});}
            var Q24;
            Q24=makeQuery(id+"F1.opExtrude","CAP_FACE",FACE,{"disambiguationData":[OSD([sQuery(id+"F0.wireOp",EDGE,"E92.bottom"),sQuery(id+"F0.wireOp",EDGE,"E92.top"),sQuery(id+"F0.wireOp",EDGE,"E95.MirrorCS"),sQuery(id+"F0.wireOp",EDGE,"E96"),sQuery(id+"F0.wireOp",EDGE,"E97"),sQuery(id+"F0.wireOp",EDGE,"E98"),sQuery(id+"F0.wireOp",EDGE,"E99"),sQuery(id+"F0.wireOp",EDGE,"E100"),sQuery(id+"F0.wireOp",EDGE,"E101.MirrorCS"),sQuery(id+"F0.wireOp",EDGE,"E102.MirrorCS"),sQuery(id+"F0.wireOp",EDGE,"E103"),sQuery(id+"F0.wireOp",EDGE,"04NsANdn-taOn-ddKp-MDbT-y7dXd8gmv4Cl"),sQuery(id+"F0.wireOp",EDGE,"E104"),sQuery(id+"F0.wireOp",EDGE,"3R8MwXPY-31j6-GvAs-L5bG-rwEBLL8UpWRA"),sQuery(id+"F0.wireOp",EDGE,"E105"),sQuery(id+"F0.wireOp",EDGE,"E106"),sQuery(id+"F0.wireOp",EDGE,"E107"),sQuery(id+"F0.wireOp",EDGE,"E108"),sQuery(id+"F0.wireOp",EDGE,"E109"),sQuery(id+"F0.wireOp",EDGE,"E110"),sQuery(id+"F0.wireOp",EDGE,"E111"),sQuery(id+"F0.wireOp",EDGE,"E112"),sQuery(id+"F0.wireOp",EDGE,"E113.right"),sQuery(id+"F0.wireOp",EDGE,"E113.left"),sQuery(id+"F0.wireOp",EDGE,"E114"),sQuery(id+"F0.wireOp",EDGE,"E115"),sQuery(id+"F0.wireOp",EDGE,"E116"),sQuery(id+"F0.wireOp",EDGE,"E117")])],"isStart":false});
            var Q25;
            Q25=makeQuery(id+"F0.imprint","IMPRINT",FACE,{"disambiguationData":[TD([[makeQuery(id+"F0.imprint","IMPRINT",EDGE,{"derivedFrom":sQuery(id+"F0.wireOp",EDGE,"E106")}),1.0]])]});
            var Q26;
            Q26=makeQuery(id+"F0.imprint","IMPRINT",FACE,{"disambiguationData":[TD([[makeQuery(id+"F0.imprint","IMPRINT",EDGE,{"derivedFrom":sQuery(id+"F0.wireOp",EDGE,"E103")}),1.0]])]});
            var Q27;
            Q27=makeQuery(id+"F0.imprint","IMPRINT",FACE,{"disambiguationData":[TD([[makeQuery(id+"F0.imprint","IMPRINT",EDGE,{"derivedFrom":sQuery(id+"F0.wireOp",EDGE,"E107")}),-1.0]])]});
            var Q28;
            Q28=makeQuery(id+"F0.imprint","IMPRINT",FACE,{"disambiguationData":[TD([[makeQuery(id+"F0.imprint","IMPRINT",EDGE,{"derivedFrom":sQuery(id+"F0.wireOp",EDGE,"E105")}),-1.0]])]});
            var Q29;
            {var subQ1=sQuery(id+"F0.wireOp",EDGE,"E92.right");Q29=makeQuery(id+"F0.imprint","IMPRINT",FACE,{"disambiguationData":[TD([[makeQuery(id+"F0.imprint","IMPRINT",EDGE,{"derivedFrom":subQ1}),-1.0]])]});}
            var Q30;
            {var subQ1=sQuery(id+"F0.wireOp",EDGE,"E118.left");Q30=makeQuery(id+"F0.imprint","IMPRINT",FACE,{"disambiguationData":[TD([[makeQuery(id+"F0.imprint","IMPRINT",EDGE,{"derivedFrom":subQ1}),1.0]])]});}
            var Q31;
            Q31=makeQuery(id+"F0.imprint","IMPRINT",FACE,{"disambiguationData":[TD([[makeQuery(id+"F0.imprint","IMPRINT",EDGE,{"derivedFrom":sQuery(id+"F0.wireOp",EDGE,"E126")}),1.0]])]});
            var Q32;
            {var subQ1=sQuery(id+"F0.wireOp",EDGE,"E118.right");Q32=makeQuery(id+"F0.imprint","IMPRINT",FACE,{"disambiguationData":[TD([[makeQuery(id+"F0.imprint","IMPRINT",EDGE,{"derivedFrom":subQ1}),-1.0]])]});}
            var Q33;
            Q33=makeQuery(id+"F1.opExtrude","CAP_FACE",FACE,{"disambiguationData":[OSD([sQuery(id+"F0.wireOp",EDGE,"E118.bottom"),sQuery(id+"F0.wireOp",EDGE,"E118.top"),sQuery(id+"F0.wireOp",EDGE,"E121"),sQuery(id+"F0.wireOp",EDGE,"E122"),sQuery(id+"F0.wireOp",EDGE,"E123"),sQuery(id+"F0.wireOp",EDGE,"E124"),sQuery(id+"F0.wireOp",EDGE,"E125"),sQuery(id+"F0.wireOp",EDGE,"E126"),sQuery(id+"F0.wireOp",EDGE,"E127"),sQuery(id+"F0.wireOp",EDGE,"E128")])],"isStart":false});
            extrude(context, id + "F3", {"entities" : qUnion([Q0, Q1, Q2, Q3, Q4, Q5, Q6, Q7, Q8, Q9, Q10, Q11, Q12, Q13, Q14, Q15, Q16, Q17, Q18, Q19, Q20, Q21, Q22, Q23, Q24, Q25, Q26, Q27, Q28, Q29, Q30, Q31, Q32, Q33]), "depth" : 3 * mm, "offsetDistance" : 25 * mm});
        }
        {
            var Q0;
            {var subQ0=sQuery(id+"F0.wireOp",EDGE,"E72");Q0=makeQuery(id+"F3.opExtrude","CAP_EDGE",EDGE,{"disambiguationData":[OSD([subQ0]),TDD([makeQuery(id+"F1.opExtrude","CAP_EDGE",EDGE,{"disambiguationData":[OSD([subQ0])],"isStart":false})])],"isStart":false});}
            var Q1;
            {var subQ0=sQuery(id+"F0.wireOp",EDGE,"E73");Q1=makeQuery(id+"F3.opExtrude","CAP_EDGE",EDGE,{"disambiguationData":[OSD([subQ0]),TDD([makeQuery(id+"F1.opExtrude","CAP_EDGE",EDGE,{"disambiguationData":[OSD([subQ0])],"isStart":false})])],"isStart":false});}
            var Q2;
            {var subQ0=sQuery(id+"F0.wireOp",EDGE,"E70.MirrorCS");Q2=makeQuery(id+"F3.opExtrude","CAP_EDGE",EDGE,{"disambiguationData":[OSD([subQ0]),TDD([makeQuery(id+"F1.opExtrude","CAP_EDGE",EDGE,{"disambiguationData":[OSD([subQ0])],"isStart":false})])],"isStart":false});}
            var Q3;
            {var subQ0=sQuery(id+"F0.wireOp",EDGE,"E71.MirrorCS");Q3=makeQuery(id+"F3.opExtrude","CAP_EDGE",EDGE,{"disambiguationData":[OSD([subQ0]),TDD([makeQuery(id+"F1.opExtrude","CAP_EDGE",EDGE,{"disambiguationData":[OSD([subQ0])],"isStart":false})])],"isStart":false});}
            var Q4;
            {var subQ0=sQuery(id+"F0.wireOp",EDGE,"E47");Q4=makeQuery(id+"F3.opExtrude","CAP_EDGE",EDGE,{"disambiguationData":[OSD([subQ0]),TDD([makeQuery(id+"F1.opExtrude","CAP_EDGE",EDGE,{"disambiguationData":[OSD([subQ0])],"isStart":false})])],"isStart":false});}
            var Q5;
            {var subQ0=sQuery(id+"F0.wireOp",EDGE,"E48");Q5=makeQuery(id+"F3.opExtrude","CAP_EDGE",EDGE,{"disambiguationData":[OSD([subQ0]),TDD([makeQuery(id+"F1.opExtrude","CAP_EDGE",EDGE,{"disambiguationData":[OSD([subQ0])],"isStart":false})])],"isStart":false});}
            var Q6;
            {var subQ0=sQuery(id+"F0.wireOp",EDGE,"E46");Q6=makeQuery(id+"F3.opExtrude","CAP_EDGE",EDGE,{"disambiguationData":[OSD([subQ0]),TDD([makeQuery(id+"F1.opExtrude","CAP_EDGE",EDGE,{"disambiguationData":[OSD([subQ0])],"isStart":false})])],"isStart":false});}
            var Q7;
            {var subQ0=sQuery(id+"F0.wireOp",EDGE,"E45");Q7=makeQuery(id+"F3.opExtrude","CAP_EDGE",EDGE,{"disambiguationData":[OSD([subQ0]),TDD([makeQuery(id+"F1.opExtrude","CAP_EDGE",EDGE,{"disambiguationData":[OSD([subQ0])],"isStart":false})])],"isStart":false});}
            var Q8;
            {var subQ0=sQuery(id+"F0.wireOp",EDGE,"E52");Q8=makeQuery(id+"F3.opExtrude","CAP_EDGE",EDGE,{"disambiguationData":[OSD([subQ0]),TDD([makeQuery(id+"F1.opExtrude","CAP_EDGE",EDGE,{"disambiguationData":[OSD([subQ0])],"isStart":false})])],"isStart":false});}
            var Q9;
            {var subQ0=sQuery(id+"F0.wireOp",EDGE,"E49");Q9=makeQuery(id+"F3.opExtrude","CAP_EDGE",EDGE,{"disambiguationData":[OSD([subQ0]),TDD([makeQuery(id+"F1.opExtrude","CAP_EDGE",EDGE,{"disambiguationData":[OSD([subQ0])],"isStart":false})])],"isStart":false});}
            var Q10;
            {var subQ0=sQuery(id+"F0.wireOp",EDGE,"E50");Q10=makeQuery(id+"F3.opExtrude","CAP_EDGE",EDGE,{"disambiguationData":[OSD([subQ0]),TDD([makeQuery(id+"F1.opExtrude","CAP_EDGE",EDGE,{"disambiguationData":[OSD([subQ0])],"isStart":false})])],"isStart":false});}
            var Q11;
            {var subQ0=sQuery(id+"F0.wireOp",EDGE,"E51");Q11=makeQuery(id+"F3.opExtrude","CAP_EDGE",EDGE,{"disambiguationData":[OSD([subQ0]),TDD([makeQuery(id+"F1.opExtrude","CAP_EDGE",EDGE,{"disambiguationData":[OSD([subQ0])],"isStart":false})])],"isStart":false});}
            var Q12;
            {var subQ0=sQuery(id+"F0.wireOp",EDGE,"E56");Q12=makeQuery(id+"F3.opExtrude","CAP_EDGE",EDGE,{"disambiguationData":[OSD([subQ0]),TDD([makeQuery(id+"F1.opExtrude","CAP_EDGE",EDGE,{"disambiguationData":[OSD([subQ0])],"isStart":false})])],"isStart":false});}
            var Q13;
            {var subQ0=sQuery(id+"F0.wireOp",EDGE,"E55");Q13=makeQuery(id+"F3.opExtrude","CAP_EDGE",EDGE,{"disambiguationData":[OSD([subQ0]),TDD([makeQuery(id+"F1.opExtrude","CAP_EDGE",EDGE,{"disambiguationData":[OSD([subQ0])],"isStart":false})])],"isStart":false});}
            var Q14;
            {var subQ0=sQuery(id+"F0.wireOp",EDGE,"E53");Q14=makeQuery(id+"F3.opExtrude","CAP_EDGE",EDGE,{"disambiguationData":[OSD([subQ0]),TDD([makeQuery(id+"F1.opExtrude","CAP_EDGE",EDGE,{"disambiguationData":[OSD([subQ0])],"isStart":false})])],"isStart":false});}
            var Q15;
            {var subQ0=sQuery(id+"F0.wireOp",EDGE,"E54");Q15=makeQuery(id+"F3.opExtrude","CAP_EDGE",EDGE,{"disambiguationData":[OSD([subQ0]),TDD([makeQuery(id+"F1.opExtrude","CAP_EDGE",EDGE,{"disambiguationData":[OSD([subQ0])],"isStart":false})])],"isStart":false});}
            var Q16;
            {var subQ0=sQuery(id+"F0.wireOp",EDGE,"E68");Q16=makeQuery(id+"F3.opExtrude","CAP_EDGE",EDGE,{"disambiguationData":[OSD([subQ0]),TDD([makeQuery(id+"F1.opExtrude","CAP_EDGE",EDGE,{"disambiguationData":[OSD([subQ0])],"isStart":false})])],"isStart":false});}
            var Q17;
            {var subQ0=sQuery(id+"F0.wireOp",EDGE,"E57");Q17=makeQuery(id+"F3.opExtrude","CAP_EDGE",EDGE,{"disambiguationData":[OSD([subQ0]),TDD([makeQuery(id+"F1.opExtrude","CAP_EDGE",EDGE,{"disambiguationData":[OSD([subQ0])],"isStart":false})])],"isStart":false});}
            var Q18;
            {var subQ0=sQuery(id+"F0.wireOp",EDGE,"E60");Q18=makeQuery(id+"F3.opExtrude","CAP_EDGE",EDGE,{"disambiguationData":[OSD([subQ0]),TDD([makeQuery(id+"F1.opExtrude","CAP_EDGE",EDGE,{"disambiguationData":[OSD([subQ0])],"isStart":false})])],"isStart":false});}
            var Q19;
            {var subQ0=sQuery(id+"F0.wireOp",EDGE,"E59");Q19=makeQuery(id+"F3.opExtrude","CAP_EDGE",EDGE,{"disambiguationData":[OSD([subQ0]),TDD([makeQuery(id+"F1.opExtrude","CAP_EDGE",EDGE,{"disambiguationData":[OSD([subQ0])],"isStart":false})])],"isStart":false});}
            var Q20;
            {var subQ0=sQuery(id+"F0.wireOp",EDGE,"E58");Q20=makeQuery(id+"F3.opExtrude","CAP_EDGE",EDGE,{"disambiguationData":[OSD([subQ0]),TDD([makeQuery(id+"F1.opExtrude","CAP_EDGE",EDGE,{"disambiguationData":[OSD([subQ0])],"isStart":false})])],"isStart":false});}
            var Q21;
            {var subQ0=sQuery(id+"F0.wireOp",EDGE,"E43");Q21=makeQuery(id+"F3.opExtrude","CAP_EDGE",EDGE,{"disambiguationData":[OSD([subQ0]),TDD([makeQuery(id+"F1.opExtrude","CAP_EDGE",EDGE,{"disambiguationData":[OSD([subQ0])],"isStart":false})])],"isStart":false});}
            var Q22;
            {var subQ0=sQuery(id+"F0.wireOp",EDGE,"E44");Q22=makeQuery(id+"F3.opExtrude","CAP_EDGE",EDGE,{"disambiguationData":[OSD([subQ0]),TDD([makeQuery(id+"F1.opExtrude","CAP_EDGE",EDGE,{"disambiguationData":[OSD([subQ0])],"isStart":false})])],"isStart":false});}
            var Q23;
            {var subQ0=sQuery(id+"F0.wireOp",EDGE,"E37");Q23=makeQuery(id+"F3.opExtrude","CAP_EDGE",EDGE,{"disambiguationData":[OSD([subQ0]),TDD([makeQuery(id+"F1.opExtrude","CAP_EDGE",EDGE,{"disambiguationData":[OSD([subQ0])],"isStart":false})])],"isStart":false});}
            var Q24;
            {var subQ0=sQuery(id+"F0.wireOp",EDGE,"E40");Q24=makeQuery(id+"F3.opExtrude","CAP_EDGE",EDGE,{"disambiguationData":[OSD([subQ0]),TDD([makeQuery(id+"F1.opExtrude","CAP_EDGE",EDGE,{"disambiguationData":[OSD([subQ0])],"isStart":false})])],"isStart":false});}
            var Q25;
            {var subQ0=sQuery(id+"F0.wireOp",EDGE,"E38");Q25=makeQuery(id+"F3.opExtrude","CAP_EDGE",EDGE,{"disambiguationData":[OSD([subQ0]),TDD([makeQuery(id+"F1.opExtrude","CAP_EDGE",EDGE,{"disambiguationData":[OSD([subQ0])],"isStart":false})])],"isStart":false});}
            var Q26;
            {var subQ0=sQuery(id+"F0.wireOp",EDGE,"E39");Q26=makeQuery(id+"F3.opExtrude","CAP_EDGE",EDGE,{"disambiguationData":[OSD([subQ0]),TDD([makeQuery(id+"F1.opExtrude","CAP_EDGE",EDGE,{"disambiguationData":[OSD([subQ0])],"isStart":false})])],"isStart":false});}
            var Q27;
            {var subQ0=sQuery(id+"F0.wireOp",EDGE,"E25");Q27=makeQuery(id+"F3.opExtrude","CAP_EDGE",EDGE,{"disambiguationData":[OSD([subQ0]),TDD([makeQuery(id+"F1.opExtrude","CAP_EDGE",EDGE,{"disambiguationData":[OSD([subQ0])],"isStart":false})])],"isStart":false});}
            var Q28;
            {var subQ0=sQuery(id+"F0.wireOp",EDGE,"E26");Q28=makeQuery(id+"F3.opExtrude","CAP_EDGE",EDGE,{"disambiguationData":[OSD([subQ0]),TDD([makeQuery(id+"F1.opExtrude","CAP_EDGE",EDGE,{"disambiguationData":[OSD([subQ0])],"isStart":false})])],"isStart":false});}
            var Q29;
            {var subQ0=sQuery(id+"F0.wireOp",EDGE,"E27");Q29=makeQuery(id+"F3.opExtrude","CAP_EDGE",EDGE,{"disambiguationData":[OSD([subQ0]),TDD([makeQuery(id+"F1.opExtrude","CAP_EDGE",EDGE,{"disambiguationData":[OSD([subQ0])],"isStart":false})])],"isStart":false});}
            var Q30;
            {var subQ0=sQuery(id+"F0.wireOp",EDGE,"E28");Q30=makeQuery(id+"F3.opExtrude","CAP_EDGE",EDGE,{"disambiguationData":[OSD([subQ0]),TDD([makeQuery(id+"F1.opExtrude","CAP_EDGE",EDGE,{"disambiguationData":[OSD([subQ0])],"isStart":false})])],"isStart":false});}
            var Q31;
            {var subQ0=sQuery(id+"F0.wireOp",EDGE,"E24");Q31=makeQuery(id+"F3.opExtrude","CAP_EDGE",EDGE,{"disambiguationData":[OSD([subQ0]),TDD([makeQuery(id+"F1.opExtrude","CAP_EDGE",EDGE,{"disambiguationData":[OSD([subQ0])],"isStart":false})])],"isStart":false});}
            var Q32;
            {var subQ0=sQuery(id+"F0.wireOp",EDGE,"E21");Q32=makeQuery(id+"F3.opExtrude","CAP_EDGE",EDGE,{"disambiguationData":[OSD([subQ0]),TDD([makeQuery(id+"F1.opExtrude","CAP_EDGE",EDGE,{"disambiguationData":[OSD([subQ0])],"isStart":false})])],"isStart":false});}
            var Q33;
            {var subQ0=sQuery(id+"F0.wireOp",EDGE,"E22");Q33=makeQuery(id+"F3.opExtrude","CAP_EDGE",EDGE,{"disambiguationData":[OSD([subQ0]),TDD([makeQuery(id+"F1.opExtrude","CAP_EDGE",EDGE,{"disambiguationData":[OSD([subQ0])],"isStart":false})])],"isStart":false});}
            var Q34;
            {var subQ0=sQuery(id+"F0.wireOp",EDGE,"E23");Q34=makeQuery(id+"F3.opExtrude","CAP_EDGE",EDGE,{"disambiguationData":[OSD([subQ0]),TDD([makeQuery(id+"F1.opExtrude","CAP_EDGE",EDGE,{"disambiguationData":[OSD([subQ0])],"isStart":false})])],"isStart":false});}
            var Q35;
            {var subQ0=sQuery(id+"F0.wireOp",EDGE,"E17");Q35=makeQuery(id+"F3.opExtrude","CAP_EDGE",EDGE,{"disambiguationData":[OSD([subQ0]),TDD([makeQuery(id+"F1.opExtrude","CAP_EDGE",EDGE,{"disambiguationData":[OSD([subQ0])],"isStart":false})])],"isStart":false});}
            var Q36;
            {var subQ0=sQuery(id+"F0.wireOp",EDGE,"E18");Q36=makeQuery(id+"F3.opExtrude","CAP_EDGE",EDGE,{"disambiguationData":[OSD([subQ0]),TDD([makeQuery(id+"F1.opExtrude","CAP_EDGE",EDGE,{"disambiguationData":[OSD([subQ0])],"isStart":false})])],"isStart":false});}
            var Q37;
            {var subQ0=sQuery(id+"F0.wireOp",EDGE,"E19");Q37=makeQuery(id+"F3.opExtrude","CAP_EDGE",EDGE,{"disambiguationData":[OSD([subQ0]),TDD([makeQuery(id+"F1.opExtrude","CAP_EDGE",EDGE,{"disambiguationData":[OSD([subQ0])],"isStart":false})])],"isStart":false});}
            var Q38;
            {var subQ0=sQuery(id+"F0.wireOp",EDGE,"E20");Q38=makeQuery(id+"F3.opExtrude","CAP_EDGE",EDGE,{"disambiguationData":[OSD([subQ0]),TDD([makeQuery(id+"F1.opExtrude","CAP_EDGE",EDGE,{"disambiguationData":[OSD([subQ0])],"isStart":false})])],"isStart":false});}
            var Q39;
            {var subQ0=sQuery(id+"F0.wireOp",EDGE,"E15");Q39=makeQuery(id+"F3.opExtrude","CAP_EDGE",EDGE,{"disambiguationData":[OSD([subQ0]),TDD([makeQuery(id+"F1.opExtrude","CAP_EDGE",EDGE,{"disambiguationData":[OSD([subQ0])],"isStart":false})])],"isStart":false});}
            var Q40;
            {var subQ0=sQuery(id+"F0.wireOp",EDGE,"E16");Q40=makeQuery(id+"F3.opExtrude","CAP_EDGE",EDGE,{"disambiguationData":[OSD([subQ0]),TDD([makeQuery(id+"F1.opExtrude","CAP_EDGE",EDGE,{"disambiguationData":[OSD([subQ0])],"isStart":false})])],"isStart":false});}
            var Q41;
            {var subQ0=sQuery(id+"F0.wireOp",EDGE,"E14");Q41=makeQuery(id+"F3.opExtrude","CAP_EDGE",EDGE,{"disambiguationData":[OSD([subQ0]),TDD([makeQuery(id+"F1.opExtrude","CAP_EDGE",EDGE,{"disambiguationData":[OSD([subQ0])],"isStart":false})])],"isStart":false});}
            var Q42;
            {var subQ0=sQuery(id+"F0.wireOp",EDGE,"E13");Q42=makeQuery(id+"F3.opExtrude","CAP_EDGE",EDGE,{"disambiguationData":[OSD([subQ0]),TDD([makeQuery(id+"F1.opExtrude","CAP_EDGE",EDGE,{"disambiguationData":[OSD([subQ0])],"isStart":false})])],"isStart":false});}
            var Q43;
            {var subQ0=sQuery(id+"F0.wireOp",EDGE,"E9");Q43=makeQuery(id+"F3.opExtrude","CAP_EDGE",EDGE,{"disambiguationData":[OSD([subQ0]),TDD([makeQuery(id+"F1.opExtrude","CAP_EDGE",EDGE,{"disambiguationData":[OSD([subQ0])],"isStart":false})])],"isStart":false});}
            var Q44;
            {var subQ0=sQuery(id+"F0.wireOp",EDGE,"E64");Q44=makeQuery(id+"F3.opExtrude","CAP_EDGE",EDGE,{"disambiguationData":[OSD([subQ0]),TDD([makeQuery(id+"F1.opExtrude","CAP_EDGE",EDGE,{"disambiguationData":[OSD([subQ0])],"isStart":false})])],"isStart":false});}
            var Q45;
            {var subQ0=sQuery(id+"F0.wireOp",EDGE,"E65");Q45=makeQuery(id+"F3.opExtrude","CAP_EDGE",EDGE,{"disambiguationData":[OSD([subQ0]),TDD([makeQuery(id+"F1.opExtrude","CAP_EDGE",EDGE,{"disambiguationData":[OSD([subQ0])],"isStart":false})])],"isStart":false});}
            var Q46;
            {var subQ0=sQuery(id+"F0.wireOp",EDGE,"E6");Q46=makeQuery(id+"F3.opExtrude","CAP_EDGE",EDGE,{"disambiguationData":[OSD([subQ0]),TDD([makeQuery(id+"F1.opExtrude","CAP_EDGE",EDGE,{"disambiguationData":[OSD([subQ0])],"isStart":false})])],"isStart":false});}
            var Q47;
            {var subQ0=sQuery(id+"F0.wireOp",EDGE,"E66");Q47=makeQuery(id+"F3.opExtrude","CAP_EDGE",EDGE,{"disambiguationData":[OSD([subQ0]),TDD([makeQuery(id+"F1.opExtrude","CAP_EDGE",EDGE,{"disambiguationData":[OSD([subQ0])],"isStart":false})])],"isStart":false});}
            var Q48;
            {var subQ0=sQuery(id+"F0.wireOp",EDGE,"E3");Q48=makeQuery(id+"F3.opExtrude","CAP_EDGE",EDGE,{"disambiguationData":[OSD([subQ0]),TDD([makeQuery(id+"F1.opExtrude","CAP_EDGE",EDGE,{"disambiguationData":[OSD([subQ0])],"isStart":false})])],"isStart":false});}
            var Q49;
            {var subQ0=sQuery(id+"F0.wireOp",EDGE,"E4");Q49=makeQuery(id+"F3.opExtrude","CAP_EDGE",EDGE,{"disambiguationData":[OSD([subQ0]),TDD([makeQuery(id+"F1.opExtrude","CAP_EDGE",EDGE,{"disambiguationData":[OSD([subQ0])],"isStart":false})])],"isStart":false});}
            var Q50;
            {var subQ0=sQuery(id+"F0.wireOp",EDGE,"E5");Q50=makeQuery(id+"F3.opExtrude","CAP_EDGE",EDGE,{"disambiguationData":[OSD([subQ0]),TDD([makeQuery(id+"F1.opExtrude","CAP_EDGE",EDGE,{"disambiguationData":[OSD([subQ0])],"isStart":false})])],"isStart":false});}
            var Q51;
            {var subQ0=sQuery(id+"F0.wireOp",EDGE,"E63");Q51=makeQuery(id+"F3.opExtrude","CAP_EDGE",EDGE,{"disambiguationData":[OSD([subQ0]),TDD([makeQuery(id+"F1.opExtrude","CAP_EDGE",EDGE,{"disambiguationData":[OSD([subQ0])],"isStart":false})])],"isStart":false});}
            var Q52;
            {var subQ0=sQuery(id+"F0.wireOp",EDGE,"E12");Q52=makeQuery(id+"F3.opExtrude","CAP_EDGE",EDGE,{"disambiguationData":[OSD([subQ0]),TDD([makeQuery(id+"F1.opExtrude","CAP_EDGE",EDGE,{"disambiguationData":[OSD([subQ0])],"isStart":false})])],"isStart":false});}
            var Q53;
            {var subQ0=sQuery(id+"F0.wireOp",EDGE,"E8");Q53=makeQuery(id+"F3.opExtrude","CAP_EDGE",EDGE,{"disambiguationData":[OSD([subQ0]),TDD([makeQuery(id+"F1.opExtrude","CAP_EDGE",EDGE,{"disambiguationData":[OSD([subQ0])],"isStart":false})])],"isStart":false});}
            var Q54;
            {var subQ0=sQuery(id+"F0.wireOp",EDGE,"E67");Q54=makeQuery(id+"F3.opExtrude","CAP_EDGE",EDGE,{"disambiguationData":[OSD([subQ0]),TDD([makeQuery(id+"F1.opExtrude","CAP_EDGE",EDGE,{"disambiguationData":[OSD([subQ0])],"isStart":false})])],"isStart":false});}
            var Q55;
            {var subQ0=sQuery(id+"F0.wireOp",EDGE,"E75");Q55=makeQuery(id+"F3.opExtrude","CAP_EDGE",EDGE,{"disambiguationData":[OSD([subQ0]),TDD([makeQuery(id+"F1.opExtrude","CAP_EDGE",EDGE,{"disambiguationData":[OSD([subQ0])],"isStart":false})])],"isStart":false});}
            var Q56;
            {var subQ0=sQuery(id+"F0.wireOp",EDGE,"E74");Q56=makeQuery(id+"F3.opExtrude","CAP_EDGE",EDGE,{"disambiguationData":[OSD([subQ0]),TDD([makeQuery(id+"F1.opExtrude","CAP_EDGE",EDGE,{"disambiguationData":[OSD([subQ0])],"isStart":false})])],"isStart":false});}
            var Q57;
            {var subQ0=sQuery(id+"F0.wireOp",EDGE,"E7");Q57=makeQuery(id+"F3.opExtrude","CAP_EDGE",EDGE,{"disambiguationData":[OSD([subQ0]),TDD([makeQuery(id+"F1.opExtrude","CAP_EDGE",EDGE,{"disambiguationData":[OSD([subQ0])],"isStart":false})])],"isStart":false});}
            var Q58;
            {var subQ0=sQuery(id+"F0.wireOp",EDGE,"E69");Q58=makeQuery(id+"F3.opExtrude","CAP_EDGE",EDGE,{"disambiguationData":[OSD([subQ0]),TDD([makeQuery(id+"F1.opExtrude","CAP_EDGE",EDGE,{"disambiguationData":[OSD([subQ0])],"isStart":false})])],"isStart":false});}
            var Q59;
            {var subQ0=sQuery(id+"F0.wireOp",EDGE,"E62");Q59=makeQuery(id+"F3.opExtrude","CAP_EDGE",EDGE,{"disambiguationData":[OSD([subQ0]),TDD([makeQuery(id+"F1.opExtrude","CAP_EDGE",EDGE,{"disambiguationData":[OSD([subQ0])],"isStart":false})])],"isStart":false});}
            var Q60;
            {var subQ0=sQuery(id+"F0.wireOp",EDGE,"E61");Q60=makeQuery(id+"F3.opExtrude","CAP_EDGE",EDGE,{"disambiguationData":[OSD([subQ0]),TDD([makeQuery(id+"F1.opExtrude","CAP_EDGE",EDGE,{"disambiguationData":[OSD([subQ0])],"isStart":false})])],"isStart":false});}
            var Q61;
            {var subQ0=sQuery(id+"F0.wireOp",EDGE,"E11");Q61=makeQuery(id+"F3.opExtrude","CAP_EDGE",EDGE,{"disambiguationData":[OSD([subQ0]),TDD([makeQuery(id+"F1.opExtrude","CAP_EDGE",EDGE,{"disambiguationData":[OSD([subQ0])],"isStart":false})])],"isStart":false});}
            var Q62;
            {var subQ0=sQuery(id+"F0.wireOp",EDGE,"E32");Q62=makeQuery(id+"F3.opExtrude","CAP_EDGE",EDGE,{"disambiguationData":[OSD([subQ0]),TDD([makeQuery(id+"F1.opExtrude","CAP_EDGE",EDGE,{"disambiguationData":[OSD([subQ0])],"isStart":false})])],"isStart":false});}
            var Q63;
            {var subQ0=sQuery(id+"F0.wireOp",EDGE,"E30");Q63=makeQuery(id+"F3.opExtrude","CAP_EDGE",EDGE,{"disambiguationData":[OSD([subQ0]),TDD([makeQuery(id+"F1.opExtrude","CAP_EDGE",EDGE,{"disambiguationData":[OSD([subQ0])],"isStart":false})])],"isStart":false});}
            var Q64;
            {var subQ0=sQuery(id+"F0.wireOp",EDGE,"E31");Q64=makeQuery(id+"F3.opExtrude","CAP_EDGE",EDGE,{"disambiguationData":[OSD([subQ0]),TDD([makeQuery(id+"F1.opExtrude","CAP_EDGE",EDGE,{"disambiguationData":[OSD([subQ0])],"isStart":false})])],"isStart":false});}
            var Q65;
            {var subQ0=sQuery(id+"F0.wireOp",EDGE,"E29");Q65=makeQuery(id+"F3.opExtrude","CAP_EDGE",EDGE,{"disambiguationData":[OSD([subQ0]),TDD([makeQuery(id+"F1.opExtrude","CAP_EDGE",EDGE,{"disambiguationData":[OSD([subQ0])],"isStart":false})])],"isStart":false});}
            var Q66;
            {var subQ0=sQuery(id+"F0.wireOp",EDGE,"E33");Q66=makeQuery(id+"F3.opExtrude","CAP_EDGE",EDGE,{"disambiguationData":[OSD([subQ0]),TDD([makeQuery(id+"F1.opExtrude","CAP_EDGE",EDGE,{"disambiguationData":[OSD([subQ0])],"isStart":false})])],"isStart":false});}
            var Q67;
            {var subQ0=sQuery(id+"F0.wireOp",EDGE,"E36");Q67=makeQuery(id+"F3.opExtrude","CAP_EDGE",EDGE,{"disambiguationData":[OSD([subQ0]),TDD([makeQuery(id+"F1.opExtrude","CAP_EDGE",EDGE,{"disambiguationData":[OSD([subQ0])],"isStart":false})])],"isStart":false});}
            var Q68;
            {var subQ0=sQuery(id+"F0.wireOp",EDGE,"E34");Q68=makeQuery(id+"F3.opExtrude","CAP_EDGE",EDGE,{"disambiguationData":[OSD([subQ0]),TDD([makeQuery(id+"F1.opExtrude","CAP_EDGE",EDGE,{"disambiguationData":[OSD([subQ0])],"isStart":false})])],"isStart":false});}
            var Q69;
            {var subQ0=sQuery(id+"F0.wireOp",EDGE,"E35");Q69=makeQuery(id+"F3.opExtrude","CAP_EDGE",EDGE,{"disambiguationData":[OSD([subQ0]),TDD([makeQuery(id+"F1.opExtrude","CAP_EDGE",EDGE,{"disambiguationData":[OSD([subQ0])],"isStart":false})])],"isStart":false});}
            var Q70;
            {var subQ0=sQuery(id+"F0.wireOp",EDGE,"E41");Q70=makeQuery(id+"F3.opExtrude","CAP_EDGE",EDGE,{"disambiguationData":[OSD([subQ0]),TDD([makeQuery(id+"F1.opExtrude","CAP_EDGE",EDGE,{"disambiguationData":[OSD([subQ0])],"isStart":false})])],"isStart":false});}
            var Q71;
            {var subQ0=sQuery(id+"F0.wireOp",EDGE,"E42");Q71=makeQuery(id+"F3.opExtrude","CAP_EDGE",EDGE,{"disambiguationData":[OSD([subQ0]),TDD([makeQuery(id+"F1.opExtrude","CAP_EDGE",EDGE,{"disambiguationData":[OSD([subQ0])],"isStart":false})])],"isStart":false});}
            var Q72;
            {var subQ0=sQuery(id+"F0.wireOp",EDGE,"E85");Q72=makeQuery(id+"F3.opExtrude","CAP_EDGE",EDGE,{"disambiguationData":[OSD([subQ0]),TDD([makeQuery(id+"F1.opExtrude","CAP_EDGE",EDGE,{"disambiguationData":[OSD([subQ0])],"isStart":false})])],"isStart":false});}
            var Q73;
            {var subQ0=sQuery(id+"F0.wireOp",EDGE,"E90.MirrorCS");Q73=makeQuery(id+"F3.opExtrude","CAP_EDGE",EDGE,{"disambiguationData":[OSD([subQ0]),TDD([makeQuery(id+"F1.opExtrude","CAP_EDGE",EDGE,{"disambiguationData":[OSD([subQ0])],"isStart":false})])],"isStart":false});}
            var Q74;
            {var subQ0=sQuery(id+"F0.wireOp",EDGE,"E87.MirrorCS");Q74=makeQuery(id+"F3.opExtrude","CAP_EDGE",EDGE,{"disambiguationData":[OSD([subQ0]),TDD([makeQuery(id+"F1.opExtrude","CAP_EDGE",EDGE,{"disambiguationData":[OSD([subQ0])],"isStart":false})])],"isStart":false});}
            var Q75;
            {var subQ0=sQuery(id+"F0.wireOp",EDGE,"E86.MirrorCS");Q75=makeQuery(id+"F3.opExtrude","CAP_EDGE",EDGE,{"disambiguationData":[OSD([subQ0]),TDD([makeQuery(id+"F1.opExtrude","CAP_EDGE",EDGE,{"disambiguationData":[OSD([subQ0])],"isStart":false})])],"isStart":false});}
            var Q76;
            {var subQ0=sQuery(id+"F0.wireOp",EDGE,"E82");Q76=makeQuery(id+"F3.opExtrude","CAP_EDGE",EDGE,{"disambiguationData":[OSD([subQ0]),TDD([makeQuery(id+"F1.opExtrude","CAP_EDGE",EDGE,{"disambiguationData":[OSD([subQ0])],"isStart":false})])],"isStart":false});}
            var Q77;
            {var subQ0=sQuery(id+"F0.wireOp",EDGE,"E83");Q77=makeQuery(id+"F3.opExtrude","CAP_EDGE",EDGE,{"disambiguationData":[OSD([subQ0]),TDD([makeQuery(id+"F1.opExtrude","CAP_EDGE",EDGE,{"disambiguationData":[OSD([subQ0])],"isStart":false})])],"isStart":false});}
            var Q78;
            {var subQ0=sQuery(id+"F0.wireOp",EDGE,"E81");Q78=makeQuery(id+"F3.opExtrude","CAP_EDGE",EDGE,{"disambiguationData":[OSD([subQ0]),TDD([makeQuery(id+"F1.opExtrude","CAP_EDGE",EDGE,{"disambiguationData":[OSD([subQ0])],"isStart":false})])],"isStart":false});}
            var Q79;
            {var subQ0=sQuery(id+"F0.wireOp",EDGE,"E80");Q79=makeQuery(id+"F3.opExtrude","CAP_EDGE",EDGE,{"disambiguationData":[OSD([subQ0]),TDD([makeQuery(id+"F1.opExtrude","CAP_EDGE",EDGE,{"disambiguationData":[OSD([subQ0])],"isStart":false})])],"isStart":false});}
            var Q80;
            {var subQ0=sQuery(id+"F0.wireOp",EDGE,"E79.MirrorCS");Q80=makeQuery(id+"F3.opExtrude","CAP_EDGE",EDGE,{"disambiguationData":[OSD([subQ0]),TDD([makeQuery(id+"F1.opExtrude","CAP_EDGE",EDGE,{"disambiguationData":[OSD([subQ0])],"isStart":false})])],"isStart":false});}
            var Q81;
            {var subQ0=sQuery(id+"F0.wireOp",EDGE,"E91.MirrorCS");Q81=makeQuery(id+"F3.opExtrude","CAP_EDGE",EDGE,{"disambiguationData":[OSD([subQ0]),TDD([makeQuery(id+"F1.opExtrude","CAP_EDGE",EDGE,{"disambiguationData":[OSD([subQ0])],"isStart":false})])],"isStart":false});}
            var Q82;
            {var subQ0=sQuery(id+"F0.wireOp",EDGE,"E89.MirrorCS");Q82=makeQuery(id+"F3.opExtrude","CAP_EDGE",EDGE,{"disambiguationData":[OSD([subQ0]),TDD([makeQuery(id+"F1.opExtrude","CAP_EDGE",EDGE,{"disambiguationData":[OSD([subQ0])],"isStart":false})])],"isStart":false});}
            var Q83;
            {var subQ0=sQuery(id+"F0.wireOp",EDGE,"E88.MirrorCS");Q83=makeQuery(id+"F3.opExtrude","CAP_EDGE",EDGE,{"disambiguationData":[OSD([subQ0]),TDD([makeQuery(id+"F1.opExtrude","CAP_EDGE",EDGE,{"disambiguationData":[OSD([subQ0])],"isStart":false})])],"isStart":false});}
            var Q84;
            {var subQ0=sQuery(id+"F0.wireOp",EDGE,"E101.MirrorCS");Q84=makeQuery(id+"F3.opExtrude","CAP_EDGE",EDGE,{"disambiguationData":[OSD([subQ0]),TDD([makeQuery(id+"F1.opExtrude","CAP_EDGE",EDGE,{"disambiguationData":[OSD([subQ0])],"isStart":false})])],"isStart":false});}
            var Q85;
            {var subQ0=sQuery(id+"F0.wireOp",EDGE,"E100");Q85=makeQuery(id+"F3.opExtrude","CAP_EDGE",EDGE,{"disambiguationData":[OSD([subQ0]),TDD([makeQuery(id+"F1.opExtrude","CAP_EDGE",EDGE,{"disambiguationData":[OSD([subQ0])],"isStart":false})])],"isStart":false});}
            var Q86;
            {var subQ0=sQuery(id+"F0.wireOp",EDGE,"E98");Q86=makeQuery(id+"F3.opExtrude","CAP_EDGE",EDGE,{"disambiguationData":[OSD([subQ0]),TDD([makeQuery(id+"F1.opExtrude","CAP_EDGE",EDGE,{"disambiguationData":[OSD([subQ0])],"isStart":false})])],"isStart":false});}
            var Q87;
            {var subQ0=sQuery(id+"F0.wireOp",EDGE,"E99");Q87=makeQuery(id+"F3.opExtrude","CAP_EDGE",EDGE,{"disambiguationData":[OSD([subQ0]),TDD([makeQuery(id+"F1.opExtrude","CAP_EDGE",EDGE,{"disambiguationData":[OSD([subQ0])],"isStart":false})])],"isStart":false});}
            var Q88;
            {var subQ0=sQuery(id+"F0.wireOp",EDGE,"E95.MirrorCS");Q88=makeQuery(id+"F3.opExtrude","CAP_EDGE",EDGE,{"disambiguationData":[OSD([subQ0]),TDD([makeQuery(id+"F1.opExtrude","CAP_EDGE",EDGE,{"disambiguationData":[OSD([subQ0])],"isStart":false})])],"isStart":false});}
            var Q89;
            {var subQ0=sQuery(id+"F0.wireOp",EDGE,"E102.MirrorCS");Q89=makeQuery(id+"F3.opExtrude","CAP_EDGE",EDGE,{"disambiguationData":[OSD([subQ0]),TDD([makeQuery(id+"F1.opExtrude","CAP_EDGE",EDGE,{"disambiguationData":[OSD([subQ0])],"isStart":false})])],"isStart":false});}
            var Q90;
            {var subQ0=sQuery(id+"F0.wireOp",EDGE,"E106");Q90=makeQuery(id+"F3.opExtrude","CAP_EDGE",EDGE,{"disambiguationData":[OSD([subQ0]),TDD([makeQuery(id+"F1.opExtrude","CAP_EDGE",EDGE,{"disambiguationData":[OSD([subQ0])],"isStart":false})])],"isStart":false});}
            var Q91;
            {var subQ0=sQuery(id+"F0.wireOp",EDGE,"E114");Q91=makeQuery(id+"F3.opExtrude","CAP_EDGE",EDGE,{"disambiguationData":[OSD([subQ0]),TDD([makeQuery(id+"F1.opExtrude","CAP_EDGE",EDGE,{"disambiguationData":[OSD([subQ0])],"isStart":false})])],"isStart":false});}
            var Q92;
            {var subQ0=sQuery(id+"F0.wireOp",EDGE,"3R8MwXPY-31j6-GvAs-L5bG-rwEBLL8UpWRA");Q92=makeQuery(id+"F3.opExtrude","CAP_EDGE",EDGE,{"disambiguationData":[OSD([subQ0]),TDD([makeQuery(id+"F1.opExtrude","CAP_EDGE",EDGE,{"disambiguationData":[OSD([subQ0])],"isStart":false})])],"isStart":false});}
            var Q93;
            {var subQ0=sQuery(id+"F0.wireOp",EDGE,"04NsANdn-taOn-ddKp-MDbT-y7dXd8gmv4Cl");Q93=makeQuery(id+"F3.opExtrude","CAP_EDGE",EDGE,{"disambiguationData":[OSD([subQ0]),TDD([makeQuery(id+"F1.opExtrude","CAP_EDGE",EDGE,{"disambiguationData":[OSD([subQ0])],"isStart":false})])],"isStart":false});}
            var Q94;
            {var subQ0=sQuery(id+"F0.wireOp",EDGE,"E103");Q94=makeQuery(id+"F3.opExtrude","CAP_EDGE",EDGE,{"disambiguationData":[OSD([subQ0]),TDD([makeQuery(id+"F1.opExtrude","CAP_EDGE",EDGE,{"disambiguationData":[OSD([subQ0])],"isStart":false})])],"isStart":false});}
            var Q95;
            {var subQ0=sQuery(id+"F0.wireOp",EDGE,"E104");Q95=makeQuery(id+"F3.opExtrude","CAP_EDGE",EDGE,{"disambiguationData":[OSD([subQ0]),TDD([makeQuery(id+"F1.opExtrude","CAP_EDGE",EDGE,{"disambiguationData":[OSD([subQ0])],"isStart":false})])],"isStart":false});}
            var Q96;
            {var subQ0=sQuery(id+"F0.wireOp",EDGE,"E117");Q96=makeQuery(id+"F3.opExtrude","CAP_EDGE",EDGE,{"disambiguationData":[OSD([subQ0]),TDD([makeQuery(id+"F1.opExtrude","CAP_EDGE",EDGE,{"disambiguationData":[OSD([subQ0])],"isStart":false})])],"isStart":false});}
            var Q97;
            {var subQ0=sQuery(id+"F0.wireOp",EDGE,"E113.right");Q97=makeQuery(id+"F3.opExtrude","CAP_EDGE",EDGE,{"disambiguationData":[OSD([subQ0]),TDD([makeQuery(id+"F1.opExtrude","CAP_EDGE",EDGE,{"disambiguationData":[OSD([subQ0])],"isStart":false})])],"isStart":false});}
            var Q98;
            {var subQ0=sQuery(id+"F0.wireOp",EDGE,"E113.left");Q98=makeQuery(id+"F3.opExtrude","CAP_EDGE",EDGE,{"disambiguationData":[OSD([subQ0]),TDD([makeQuery(id+"F1.opExtrude","CAP_EDGE",EDGE,{"disambiguationData":[OSD([subQ0])],"isStart":false})])],"isStart":false});}
            var Q99;
            {var subQ0=sQuery(id+"F0.wireOp",EDGE,"E116");Q99=makeQuery(id+"F3.opExtrude","CAP_EDGE",EDGE,{"disambiguationData":[OSD([subQ0]),TDD([makeQuery(id+"F1.opExtrude","CAP_EDGE",EDGE,{"disambiguationData":[OSD([subQ0])],"isStart":false})])],"isStart":false});}
            var Q100;
            {var subQ0=sQuery(id+"F0.wireOp",EDGE,"E109");Q100=makeQuery(id+"F3.opExtrude","CAP_EDGE",EDGE,{"disambiguationData":[OSD([subQ0]),TDD([makeQuery(id+"F0.imprint","IMPRINT",EDGE,{"derivedFrom":subQ0})])],"isStart":false});}
            var Q101;
            {var subQ0=sQuery(id+"F0.wireOp",EDGE,"E105");Q101=makeQuery(id+"F3.opExtrude","CAP_EDGE",EDGE,{"disambiguationData":[OSD([subQ0]),TDD([makeQuery(id+"F1.opExtrude","CAP_EDGE",EDGE,{"disambiguationData":[OSD([subQ0])],"isStart":false})])],"isStart":false});}
            var Q102;
            {var subQ0=sQuery(id+"F0.wireOp",EDGE,"E115");Q102=makeQuery(id+"F3.opExtrude","CAP_EDGE",EDGE,{"disambiguationData":[OSD([subQ0]),TDD([makeQuery(id+"F1.opExtrude","CAP_EDGE",EDGE,{"disambiguationData":[OSD([subQ0])],"isStart":false})])],"isStart":false});}
            var Q103;
            {var subQ0=sQuery(id+"F0.wireOp",EDGE,"E112");Q103=makeQuery(id+"F3.opExtrude","CAP_EDGE",EDGE,{"disambiguationData":[OSD([subQ0]),TDD([makeQuery(id+"F1.opExtrude","CAP_EDGE",EDGE,{"disambiguationData":[OSD([subQ0])],"isStart":false})])],"isStart":false});}
            var Q104;
            {var subQ0=sQuery(id+"F0.wireOp",EDGE,"E96");Q104=makeQuery(id+"F3.opExtrude","CAP_EDGE",EDGE,{"disambiguationData":[OSD([subQ0]),TDD([makeQuery(id+"F1.opExtrude","CAP_EDGE",EDGE,{"disambiguationData":[OSD([subQ0])],"isStart":false})])],"isStart":false});}
            var Q105;
            {var subQ0=sQuery(id+"F0.wireOp",EDGE,"E97");Q105=makeQuery(id+"F3.opExtrude","CAP_EDGE",EDGE,{"disambiguationData":[OSD([subQ0]),TDD([makeQuery(id+"F1.opExtrude","CAP_EDGE",EDGE,{"disambiguationData":[OSD([subQ0])],"isStart":false})])],"isStart":false});}
            var Q106;
            {var subQ0=sQuery(id+"F0.wireOp",EDGE,"E110");Q106=makeQuery(id+"F3.opExtrude","CAP_EDGE",EDGE,{"disambiguationData":[OSD([subQ0]),TDD([makeQuery(id+"F1.opExtrude","CAP_EDGE",EDGE,{"disambiguationData":[OSD([subQ0])],"isStart":false})])],"isStart":false});}
            var Q107;
            {var subQ0=sQuery(id+"F0.wireOp",EDGE,"E111");Q107=makeQuery(id+"F3.opExtrude","CAP_EDGE",EDGE,{"disambiguationData":[OSD([subQ0]),TDD([makeQuery(id+"F1.opExtrude","CAP_EDGE",EDGE,{"disambiguationData":[OSD([subQ0])],"isStart":false})])],"isStart":false});}
            var Q108;
            {var subQ0=sQuery(id+"F0.wireOp",EDGE,"E107");Q108=makeQuery(id+"F3.opExtrude","CAP_EDGE",EDGE,{"disambiguationData":[OSD([subQ0]),TDD([makeQuery(id+"F1.opExtrude","CAP_EDGE",EDGE,{"disambiguationData":[OSD([subQ0])],"isStart":false})])],"isStart":false});}
            var Q109;
            {var subQ0=sQuery(id+"F0.wireOp",EDGE,"E108");Q109=makeQuery(id+"F3.opExtrude","CAP_EDGE",EDGE,{"disambiguationData":[OSD([subQ0]),TDD([makeQuery(id+"F1.opExtrude","CAP_EDGE",EDGE,{"disambiguationData":[OSD([subQ0])],"isStart":false})])],"isStart":false});}
            var Q110;
            {var subQ0=sQuery(id+"F0.wireOp",EDGE,"E126");Q110=makeQuery(id+"F3.opExtrude","CAP_EDGE",EDGE,{"disambiguationData":[OSD([subQ0]),TDD([makeQuery(id+"F1.opExtrude","CAP_EDGE",EDGE,{"disambiguationData":[OSD([subQ0])],"isStart":false})])],"isStart":false});}
            var Q111;
            {var subQ0=sQuery(id+"F0.wireOp",EDGE,"E128");Q111=makeQuery(id+"F3.opExtrude","CAP_EDGE",EDGE,{"disambiguationData":[OSD([subQ0]),TDD([makeQuery(id+"F1.opExtrude","CAP_EDGE",EDGE,{"disambiguationData":[OSD([subQ0])],"isStart":false})])],"isStart":false});}
            var Q112;
            {var subQ0=sQuery(id+"F0.wireOp",EDGE,"E123");Q112=makeQuery(id+"F3.opExtrude","CAP_EDGE",EDGE,{"disambiguationData":[OSD([subQ0]),TDD([makeQuery(id+"F1.opExtrude","CAP_EDGE",EDGE,{"disambiguationData":[OSD([subQ0])],"isStart":false})])],"isStart":false});}
            var Q113;
            {var subQ0=sQuery(id+"F0.wireOp",EDGE,"E124");Q113=makeQuery(id+"F3.opExtrude","CAP_EDGE",EDGE,{"disambiguationData":[OSD([subQ0]),TDD([makeQuery(id+"F1.opExtrude","CAP_EDGE",EDGE,{"disambiguationData":[OSD([subQ0])],"isStart":false})])],"isStart":false});}
            var Q114;
            {var subQ0=sQuery(id+"F0.wireOp",EDGE,"E125");Q114=makeQuery(id+"F3.opExtrude","CAP_EDGE",EDGE,{"disambiguationData":[OSD([subQ0]),TDD([makeQuery(id+"F1.opExtrude","CAP_EDGE",EDGE,{"disambiguationData":[OSD([subQ0])],"isStart":false})])],"isStart":false});}
            var Q115;
            {var subQ0=sQuery(id+"F0.wireOp",EDGE,"E127");Q115=makeQuery(id+"F3.opExtrude","CAP_EDGE",EDGE,{"disambiguationData":[OSD([subQ0]),TDD([makeQuery(id+"F1.opExtrude","CAP_EDGE",EDGE,{"disambiguationData":[OSD([subQ0])],"isStart":false})])],"isStart":false});}
            var Q116;
            {var subQ0=sQuery(id+"F0.wireOp",EDGE,"E121");Q116=makeQuery(id+"F3.opExtrude","CAP_EDGE",EDGE,{"disambiguationData":[OSD([subQ0]),TDD([makeQuery(id+"F1.opExtrude","CAP_EDGE",EDGE,{"disambiguationData":[OSD([subQ0])],"isStart":false})])],"isStart":false});}
            var Q117;
            {var subQ0=sQuery(id+"F0.wireOp",EDGE,"E122");Q117=makeQuery(id+"F3.opExtrude","CAP_EDGE",EDGE,{"disambiguationData":[OSD([subQ0]),TDD([makeQuery(id+"F1.opExtrude","CAP_EDGE",EDGE,{"disambiguationData":[OSD([subQ0])],"isStart":false})])],"isStart":false});}
            fillet(context, id + "F4", {"entities" : qUnion([Q0, Q1, Q2, Q3, Q4, Q5, Q6, Q7, Q8, Q9, Q10, Q11, Q12, Q13, Q14, Q15, Q16, Q17, Q18, Q19, Q20, Q21, Q22, Q23, Q24, Q25, Q26, Q27, Q28, Q29, Q30, Q31, Q32, Q33, Q34, Q35, Q36, Q37, Q38, Q39, Q40, Q41, Q42, Q43, Q44, Q45, Q46, Q47, Q48, Q49, Q50, Q51, Q52, Q53, Q54, Q55, Q56, Q57, Q58, Q59, Q60, Q61, Q62, Q63, Q64, Q65, Q66, Q67, Q68, Q69, Q70, Q71, Q72, Q73, Q74, Q75, Q76, Q77, Q78, Q79, Q80, Q81, Q82, Q83, Q84, Q85, Q86, Q87, Q88, Q89, Q90, Q91, Q92, Q93, Q94, Q95, Q96, Q97, Q98, Q99, Q100, Q101, Q102, Q103, Q104, Q105, Q106, Q107, Q108, Q109, Q110, Q111, Q112, Q113, Q114, Q115, Q116, Q117]), "radius" : .29 * mm, "allowEdgeOverflow" : false});
        }
        {
            var Q0;
            {var subQ0=sQuery(id+"F0.wireOp",EDGE,"E60");var subQ1=sQuery(id+"F0.wireOp",EDGE,"E59");var subQ2=sQuery(id+"F0.wireOp",EDGE,"E58");var subQ3=sQuery(id+"F0.wireOp",EDGE,"E57");var subQ4=sQuery(id+"F0.wireOp",EDGE,"E56");var subQ5=sQuery(id+"F0.wireOp",EDGE,"E55");var subQ6=sQuery(id+"F0.wireOp",EDGE,"E54");var subQ7=sQuery(id+"F0.wireOp",EDGE,"E53");var subQ8=sQuery(id+"F0.wireOp",EDGE,"E52");var subQ9=sQuery(id+"F0.wireOp",EDGE,"E51");var subQ10=sQuery(id+"F0.wireOp",EDGE,"E50");var subQ11=sQuery(id+"F0.wireOp",EDGE,"E49");var subQ12=sQuery(id+"F0.wireOp",EDGE,"E48");var subQ13=sQuery(id+"F0.wireOp",EDGE,"E47");var subQ14=sQuery(id+"F0.wireOp",EDGE,"E46");var subQ15=sQuery(id+"F0.wireOp",EDGE,"E45");var subQ16=sQuery(id+"F0.wireOp",EDGE,"E44");var subQ17=sQuery(id+"F0.wireOp",EDGE,"E43");var subQ18=sQuery(id+"F0.wireOp",EDGE,"E42");var subQ19=sQuery(id+"F0.wireOp",EDGE,"E41");var subQ20=sQuery(id+"F0.wireOp",EDGE,"E40");var subQ21=sQuery(id+"F0.wireOp",EDGE,"E39");var subQ22=sQuery(id+"F0.wireOp",EDGE,"E38");var subQ23=sQuery(id+"F0.wireOp",EDGE,"E37");var subQ24=sQuery(id+"F0.wireOp",EDGE,"E36");var subQ25=sQuery(id+"F0.wireOp",EDGE,"E35");var subQ26=sQuery(id+"F0.wireOp",EDGE,"E34");var subQ27=sQuery(id+"F0.wireOp",EDGE,"E33");var subQ28=sQuery(id+"F0.wireOp",EDGE,"E32");var subQ29=sQuery(id+"F0.wireOp",EDGE,"E31");var subQ30=sQuery(id+"F0.wireOp",EDGE,"E30");var subQ31=sQuery(id+"F0.wireOp",EDGE,"E29");var subQ32=sQuery(id+"F0.wireOp",EDGE,"E28");var subQ33=sQuery(id+"F0.wireOp",EDGE,"E27");var subQ34=sQuery(id+"F0.wireOp",EDGE,"E26");var subQ35=sQuery(id+"F0.wireOp",EDGE,"E25");var subQ36=sQuery(id+"F0.wireOp",EDGE,"E24");var subQ37=sQuery(id+"F0.wireOp",EDGE,"E23");var subQ38=sQuery(id+"F0.wireOp",EDGE,"E22");var subQ39=sQuery(id+"F0.wireOp",EDGE,"E21");var subQ40=sQuery(id+"F0.wireOp",EDGE,"E20");var subQ41=sQuery(id+"F0.wireOp",EDGE,"E19");var subQ42=sQuery(id+"F0.wireOp",EDGE,"E18");var subQ43=sQuery(id+"F0.wireOp",EDGE,"E17");var subQ44=sQuery(id+"F0.wireOp",EDGE,"E16");var subQ45=sQuery(id+"F0.wireOp",EDGE,"E15");var subQ46=sQuery(id+"F0.wireOp",EDGE,"E14");var subQ47=sQuery(id+"F0.wireOp",EDGE,"E13");var subQ48=sQuery(id+"F0.wireOp",EDGE,"E67");var subQ49=sQuery(id+"F0.wireOp",EDGE,"E63");var subQ50=sQuery(id+"F0.wireOp",EDGE,"E12");var subQ51=sQuery(id+"F0.wireOp",EDGE,"E8");var subQ52=sQuery(id+"F0.wireOp",EDGE,"E62");var subQ53=sQuery(id+"F0.wireOp",EDGE,"E61");var subQ54=sQuery(id+"F0.wireOp",EDGE,"E11");var subQ55=sQuery(id+"F0.wireOp",EDGE,"E7");var subQ56=sQuery(id+"F0.wireOp",EDGE,"E65");var subQ57=sQuery(id+"F0.wireOp",EDGE,"E64");var subQ58=sQuery(id+"F0.wireOp",EDGE,"E9");var subQ59=sQuery(id+"F0.wireOp",EDGE,"E6");var subQ60=sQuery(id+"F0.wireOp",EDGE,"E66");var subQ61=sQuery(id+"F0.wireOp",EDGE,"E5");var subQ62=sQuery(id+"F0.wireOp",EDGE,"E4");var subQ63=sQuery(id+"F0.wireOp",EDGE,"E3");var subQ64=sQuery(id+"F0.wireOp",EDGE,"edaaeaec-2fa2-4ac8-96e5-24b6cc5294a60.MirrorC");var subQ65=sQuery(id+"F0.wireOp",EDGE,"E75");var subQ66=sQuery(id+"F0.wireOp",EDGE,"E73");var subQ67=sQuery(id+"F0.wireOp",EDGE,"E71.MirrorCS");var subQ68=sQuery(id+"F0.wireOp",EDGE,"E68");var subQ69=sQuery(id+"F0.wireOp",EDGE,"E0.right");var subQ70=sQuery(id+"F0.wireOp",EDGE,"E0.top");var subQ71=sQuery(id+"F0.wireOp",EDGE,"E0.bottom");var subQ72=sQuery(id+"F0.wireOp",EDGE,"W2vNM0GE-2OHP-QNdi-PDCA-W7E0gAEi5RRH");var subQ73=sQuery(id+"F0.wireOp",EDGE,"E74");var subQ74=sQuery(id+"F0.wireOp",EDGE,"E72");var subQ75=sQuery(id+"F0.wireOp",EDGE,"E70.MirrorCS");var subQ76=sQuery(id+"F0.wireOp",EDGE,"E69");var subQ77=sQuery(id+"F0.wireOp",EDGE,"E0.left");var subQ78=makeQuery(id+"F2.opExtrude","CAP_FACE",FACE,{"disambiguationData":[OSD([subQ71,subQ70,subQ77,subQ69,sQuery(id+"F0.wireOp",EDGE,"E1.bottom"),sQuery(id+"F0.wireOp",EDGE,"E1.top"),sQuery(id+"F0.wireOp",EDGE,"E1.left"),sQuery(id+"F0.wireOp",EDGE,"E1.right")])],"isStart":true});Q0=makeQuery(id+"F6.boolean.opBoolean","MERGE",FACE,{"derivedFrom":[subQ78,makeQuery(id+"F6.opPattern","COPY",FACE,{"derivedFrom":makeQuery(id+"F1.opExtrude","CAP_FACE",FACE,{"disambiguationData":[OSD([subQ71,subQ70,subQ63,subQ62,subQ61,subQ59,subQ55,subQ51,subQ58,subQ54,subQ50,subQ47,subQ46,subQ45,subQ44,subQ43,subQ42,subQ41,subQ40,subQ39,subQ38,subQ37,subQ36,subQ35,subQ34,subQ33,subQ32,subQ31,subQ30,subQ29,subQ28,subQ27,subQ26,subQ25,subQ24,subQ23,subQ22,subQ21,subQ20,subQ19,subQ18,subQ17,subQ16,subQ15,subQ14,subQ13,subQ12,subQ11,subQ10,subQ9,subQ8,subQ7,subQ6,subQ5,subQ4,subQ3,subQ2,subQ1,subQ0,subQ53,subQ52,subQ49,subQ57,subQ56,subQ60,subQ48,subQ68,subQ76,subQ75,subQ67,subQ74,subQ66,subQ73,subQ65])],"isStart":true}),"instanceName":"1"}),makeQuery(id+"F6.opPattern","COPY",FACE,{"derivedFrom":subQ78,"instanceName":"1"}),makeQuery(id+"F6.opPattern","COPY",FACE,{"derivedFrom":makeQuery(id+"F2.opExtrude","CAP_FACE",FACE,{"disambiguationData":[OSD([subQ72])],"isStart":true}),"instanceName":"1"}),makeQuery(id+"F6.opPattern","COPY",FACE,{"derivedFrom":makeQuery(id+"F2.opExtrude","CAP_FACE",FACE,{"disambiguationData":[OSD([subQ64])],"isStart":true}),"instanceName":"1"}),makeQuery(id+"F6.opPattern","COPY",FACE,{"derivedFrom":makeQuery(id+"F3.opExtrude","CAP_FACE",FACE,{"disambiguationData":[OSD([subQ71,subQ70,subQ77,subQ76,subQ75,subQ74,subQ73,subQ72,sQuery(id+"F0.wireOp",EDGE,"0858af88-9474-4ed9-898e-377d812cf8890.MirrorC")])],"isStart":true}),"instanceName":"1"}),makeQuery(id+"F6.opPattern","COPY",FACE,{"derivedFrom":makeQuery(id+"F3.opExtrude","CAP_FACE",FACE,{"disambiguationData":[OSD([subQ71,subQ70,subQ69,subQ68,subQ67,subQ66,subQ65,subQ64,sQuery(id+"F0.wireOp",EDGE,"ccb5a7b4-4bd2-4bd8-aee6-5957949556a70.MirrorC")])],"isStart":true}),"instanceName":"1"}),makeQuery(id+"F6.opPattern","COPY",FACE,{"derivedFrom":makeQuery(id+"F3.opExtrude","CAP_FACE",FACE,{"disambiguationData":[OSD([subQ63,subQ62,subQ61,subQ60])],"isStart":true}),"instanceName":"1"}),makeQuery(id+"F6.opPattern","COPY",FACE,{"derivedFrom":makeQuery(id+"F3.opExtrude","CAP_FACE",FACE,{"disambiguationData":[OSD([subQ59,subQ58,subQ57,subQ56])],"isStart":true}),"instanceName":"1"}),makeQuery(id+"F6.opPattern","COPY",FACE,{"derivedFrom":makeQuery(id+"F3.opExtrude","CAP_FACE",FACE,{"disambiguationData":[OSD([subQ55,subQ54,subQ53,subQ52])],"isStart":true}),"instanceName":"1"}),makeQuery(id+"F6.opPattern","COPY",FACE,{"derivedFrom":makeQuery(id+"F3.opExtrude","CAP_FACE",FACE,{"disambiguationData":[OSD([subQ51,subQ50,subQ49,subQ48])],"isStart":true}),"instanceName":"1"}),makeQuery(id+"F6.opPattern","COPY",FACE,{"derivedFrom":makeQuery(id+"F3.opExtrude","CAP_FACE",FACE,{"disambiguationData":[OSD([subQ47,subQ46,subQ45,subQ44])],"isStart":true}),"instanceName":"1"}),makeQuery(id+"F6.opPattern","COPY",FACE,{"derivedFrom":makeQuery(id+"F3.opExtrude","CAP_FACE",FACE,{"disambiguationData":[OSD([subQ43,subQ42,subQ41,subQ40])],"isStart":true}),"instanceName":"1"}),makeQuery(id+"F6.opPattern","COPY",FACE,{"derivedFrom":makeQuery(id+"F3.opExtrude","CAP_FACE",FACE,{"disambiguationData":[OSD([subQ39,subQ38,subQ37,subQ36])],"isStart":true}),"instanceName":"1"}),makeQuery(id+"F6.opPattern","COPY",FACE,{"derivedFrom":makeQuery(id+"F3.opExtrude","CAP_FACE",FACE,{"disambiguationData":[OSD([subQ35,subQ34,subQ33,subQ32])],"isStart":true}),"instanceName":"1"}),makeQuery(id+"F6.opPattern","COPY",FACE,{"derivedFrom":makeQuery(id+"F3.opExtrude","CAP_FACE",FACE,{"disambiguationData":[OSD([subQ31,subQ30,subQ29,subQ28])],"isStart":true}),"instanceName":"1"}),makeQuery(id+"F6.opPattern","COPY",FACE,{"derivedFrom":makeQuery(id+"F3.opExtrude","CAP_FACE",FACE,{"disambiguationData":[OSD([subQ27,subQ26,subQ25,subQ24])],"isStart":true}),"instanceName":"1"}),makeQuery(id+"F6.opPattern","COPY",FACE,{"derivedFrom":makeQuery(id+"F3.opExtrude","CAP_FACE",FACE,{"disambiguationData":[OSD([subQ23,subQ22,subQ21,subQ20])],"isStart":true}),"instanceName":"1"}),makeQuery(id+"F6.opPattern","COPY",FACE,{"derivedFrom":makeQuery(id+"F3.opExtrude","CAP_FACE",FACE,{"disambiguationData":[OSD([subQ19,subQ18,subQ17,subQ16])],"isStart":true}),"instanceName":"1"}),makeQuery(id+"F6.opPattern","COPY",FACE,{"derivedFrom":makeQuery(id+"F3.opExtrude","CAP_FACE",FACE,{"disambiguationData":[OSD([subQ15,subQ14,subQ13,subQ12])],"isStart":true}),"instanceName":"1"}),makeQuery(id+"F6.opPattern","COPY",FACE,{"derivedFrom":makeQuery(id+"F3.opExtrude","CAP_FACE",FACE,{"disambiguationData":[OSD([subQ11,subQ10,subQ9,subQ8])],"isStart":true}),"instanceName":"1"}),makeQuery(id+"F6.opPattern","COPY",FACE,{"derivedFrom":makeQuery(id+"F3.opExtrude","CAP_FACE",FACE,{"disambiguationData":[OSD([subQ7,subQ6,subQ5,subQ4])],"isStart":true}),"instanceName":"1"}),makeQuery(id+"F6.opPattern","COPY",FACE,{"derivedFrom":makeQuery(id+"F3.opExtrude","CAP_FACE",FACE,{"disambiguationData":[OSD([subQ3,subQ2,subQ1,subQ0])],"isStart":true}),"instanceName":"1"})]});}
            var Q1;
            {var subQ0=sQuery(id+"F0.wireOp",EDGE,"E0.right");Q1=makeQuery(id+"F0.imprint","IMPRINT",FACE,{"disambiguationData":[TD([[makeQuery(id+"F0.imprint","IMPRINT",EDGE,{"derivedFrom":subQ0}),-1.0]])]});}
            var Q2;
            Q2=makeQuery(id+"F0.imprint","IMPRINT",FACE,{"disambiguationData":[TD([[makeQuery(id+"F0.imprint","IMPRINT",EDGE,{"derivedFrom":sQuery(id+"F0.wireOp",EDGE,"edaaeaec-2fa2-4ac8-96e5-24b6cc5294a60.MirrorC")}),-1.0]])]});
            var Q3;
            Q3=makeQuery(id+"F0.imprint","IMPRINT",FACE,{"disambiguationData":[TD([[makeQuery(id+"F0.imprint","IMPRINT",EDGE,{"derivedFrom":sQuery(id+"F0.wireOp",EDGE,"W2vNM0GE-2OHP-QNdi-PDCA-W7E0gAEi5RRH")}),1.0]])]});
            var Q4;
            {var subQ0=sQuery(id+"F0.wireOp",EDGE,"E0.left");Q4=makeQuery(id+"F0.imprint","IMPRINT",FACE,{"disambiguationData":[TD([[makeQuery(id+"F0.imprint","IMPRINT",EDGE,{"derivedFrom":subQ0}),1.0]])]});}
            var Q5;
            Q5=makeQuery(id+"F0.imprint","IMPRINT",FACE,{"disambiguationData":[TD([[makeQuery(id+"F0.imprint","IMPRINT",EDGE,{"derivedFrom":sQuery(id+"F0.wireOp",EDGE,"E3")}),1.0]])]});
            var Q6;
            Q6=makeQuery(id+"F0.imprint","IMPRINT",FACE,{"disambiguationData":[TD([[makeQuery(id+"F0.imprint","IMPRINT",EDGE,{"derivedFrom":sQuery(id+"F0.wireOp",EDGE,"E57")}),1.0]])]});
            var Q7;
            Q7=makeQuery(id+"F0.imprint","IMPRINT",FACE,{"disambiguationData":[TD([[makeQuery(id+"F0.imprint","IMPRINT",EDGE,{"derivedFrom":sQuery(id+"F0.wireOp",EDGE,"E53")}),-1.0]])]});
            var Q8;
            Q8=makeQuery(id+"F0.imprint","IMPRINT",FACE,{"disambiguationData":[TD([[makeQuery(id+"F0.imprint","IMPRINT",EDGE,{"derivedFrom":sQuery(id+"F0.wireOp",EDGE,"E37")}),1.0]])]});
            var Q9;
            Q9=makeQuery(id+"F0.imprint","IMPRINT",FACE,{"disambiguationData":[TD([[makeQuery(id+"F0.imprint","IMPRINT",EDGE,{"derivedFrom":sQuery(id+"F0.wireOp",EDGE,"E41")}),-1.0]])]});
            var Q10;
            Q10=makeQuery(id+"F0.imprint","IMPRINT",FACE,{"disambiguationData":[TD([[makeQuery(id+"F0.imprint","IMPRINT",EDGE,{"derivedFrom":sQuery(id+"F0.wireOp",EDGE,"E25")}),1.0]])]});
            var Q11;
            Q11=makeQuery(id+"F0.imprint","IMPRINT",FACE,{"disambiguationData":[TD([[makeQuery(id+"F0.imprint","IMPRINT",EDGE,{"derivedFrom":sQuery(id+"F0.wireOp",EDGE,"E8")}),1.0]])]});
            var Q12;
            Q12=makeQuery(id+"F0.imprint","IMPRINT",FACE,{"disambiguationData":[TD([[makeQuery(id+"F0.imprint","IMPRINT",EDGE,{"derivedFrom":sQuery(id+"F0.wireOp",EDGE,"E17")}),1.0]])]});
            var Q13;
            Q13=makeQuery(id+"F0.imprint","IMPRINT",FACE,{"disambiguationData":[TD([[makeQuery(id+"F0.imprint","IMPRINT",EDGE,{"derivedFrom":sQuery(id+"F0.wireOp",EDGE,"E33")}),-1.0]])]});
            var Q14;
            Q14=makeQuery(id+"F0.imprint","IMPRINT",FACE,{"disambiguationData":[TD([[makeQuery(id+"F0.imprint","IMPRINT",EDGE,{"derivedFrom":sQuery(id+"F0.wireOp",EDGE,"E45")}),-1.0]])]});
            var Q15;
            Q15=makeQuery(id+"F0.imprint","IMPRINT",FACE,{"disambiguationData":[TD([[makeQuery(id+"F0.imprint","IMPRINT",EDGE,{"derivedFrom":sQuery(id+"F0.wireOp",EDGE,"E29")}),1.0]])]});
            var Q16;
            Q16=makeQuery(id+"F0.imprint","IMPRINT",FACE,{"disambiguationData":[TD([[makeQuery(id+"F0.imprint","IMPRINT",EDGE,{"derivedFrom":sQuery(id+"F0.wireOp",EDGE,"E13")}),-1.0]])]});
            var Q17;
            Q17=makeQuery(id+"F0.imprint","IMPRINT",FACE,{"disambiguationData":[TD([[makeQuery(id+"F0.imprint","IMPRINT",EDGE,{"derivedFrom":sQuery(id+"F0.wireOp",EDGE,"E6")}),-1.0]])]});
            var Q18;
            Q18=makeQuery(id+"F0.imprint","IMPRINT",FACE,{"disambiguationData":[TD([[makeQuery(id+"F0.imprint","IMPRINT",EDGE,{"derivedFrom":sQuery(id+"F0.wireOp",EDGE,"E7")}),1.0]])]});
            var Q19;
            Q19=makeQuery(id+"F0.imprint","IMPRINT",FACE,{"disambiguationData":[TD([[makeQuery(id+"F0.imprint","IMPRINT",EDGE,{"derivedFrom":sQuery(id+"F0.wireOp",EDGE,"E21")}),1.0]])]});
            var Q20;
            Q20=makeQuery(id+"F0.imprint","IMPRINT",FACE,{"disambiguationData":[TD([[makeQuery(id+"F0.imprint","IMPRINT",EDGE,{"derivedFrom":sQuery(id+"F0.wireOp",EDGE,"E3")}),-1.0]])]});
            var Q21;
            Q21=makeQuery(id+"F0.imprint","IMPRINT",FACE,{"disambiguationData":[TD([[makeQuery(id+"F0.imprint","IMPRINT",EDGE,{"derivedFrom":sQuery(id+"F0.wireOp",EDGE,"E49")}),1.0]])]});
            var Q22;
            Q22=makeQuery(id+"F0.imprint","IMPRINT",FACE,{"disambiguationData":[TD([[makeQuery(id+"F0.imprint","IMPRINT",EDGE,{"derivedFrom":sQuery(id+"F0.wireOp",EDGE,"ccb5a7b4-4bd2-4bd8-aee6-5957949556a70.MirrorC")}),1.0]])]});
            var Q23;
            Q23=makeQuery(id+"F0.imprint","IMPRINT",FACE,{"disambiguationData":[TD([[makeQuery(id+"F0.imprint","IMPRINT",EDGE,{"derivedFrom":sQuery(id+"F0.wireOp",EDGE,"0858af88-9474-4ed9-898e-377d812cf8890.MirrorC")}),-1.0]])]});
            var Q24;
            Q24=makeQuery(id+"F0.imprint","IMPRINT",FACE,{"disambiguationData":[TD([[makeQuery(id+"F0.imprint","IMPRINT",EDGE,{"derivedFrom":sQuery(id+"F0.wireOp",EDGE,"d06192a0-faee-4ce2-b979-33eab6da30e80.MirrorC")}),-1.0]])]});
            var Q25;
            Q25=makeQuery(id+"F0.imprint","IMPRINT",FACE,{"disambiguationData":[TD([[makeQuery(id+"F0.imprint","IMPRINT",EDGE,{"derivedFrom":sQuery(id+"F0.wireOp",EDGE,"fcab7095-a197-4313-a40f-46269419fcac0.MirrorC")}),1.0]])]});
            var Q26;
            Q26=makeQuery(id+"F0.imprint","IMPRINT",FACE,{"disambiguationData":[TD([[makeQuery(id+"F0.imprint","IMPRINT",EDGE,{"derivedFrom":sQuery(id+"F0.wireOp",EDGE,"8cd1bf5f-9e5d-4626-ba93-0b63d8eae1ea0.MirrorC")}),-1.0]])]});
            var Q27;
            {var subQ1=sQuery(id+"F0.wireOp",EDGE,"E76.left");Q27=makeQuery(id+"F0.imprint","IMPRINT",FACE,{"disambiguationData":[TD([[makeQuery(id+"F0.imprint","IMPRINT",EDGE,{"derivedFrom":subQ1}),-1.0]])]});}
            var Q28;
            Q28=makeQuery(id+"F0.imprint","IMPRINT",FACE,{"disambiguationData":[TD([[makeQuery(id+"F0.imprint","IMPRINT",EDGE,{"derivedFrom":sQuery(id+"F0.wireOp",EDGE,"c05c3f3a-ed90-42bd-9269-905621a1effa.MirrorC")}),-1.0]])]});
            var Q29;
            Q29=makeQuery(id+"F0.imprint","IMPRINT",FACE,{"disambiguationData":[TD([[makeQuery(id+"F0.imprint","IMPRINT",EDGE,{"derivedFrom":sQuery(id+"F0.wireOp",EDGE,"d12e2bef-71cd-4f09-8da8-46f55b03c3f2.MirrorC")}),1.0]])]});
            var Q30;
            Q30=makeQuery(id+"F0.imprint","IMPRINT",FACE,{"disambiguationData":[TD([[makeQuery(id+"F0.imprint","IMPRINT",EDGE,{"derivedFrom":sQuery(id+"F0.wireOp",EDGE,"899422d1-b2af-4982-8523-cbcbc75a0b1b.MirrorC")}),-1.0]])]});
            var Q31;
            Q31=makeQuery(id+"F0.imprint","IMPRINT",FACE,{"disambiguationData":[TD([[makeQuery(id+"F0.imprint","IMPRINT",EDGE,{"derivedFrom":sQuery(id+"F0.wireOp",EDGE,"E84")}),1.0]])]});
            var Q32;
            Q32=makeQuery(id+"F0.imprint","IMPRINT",FACE,{"disambiguationData":[TD([[makeQuery(id+"F0.imprint","IMPRINT",EDGE,{"derivedFrom":sQuery(id+"F0.wireOp",EDGE,"E87.MirrorCS")}),1.0]])]});
            var Q33;
            Q33=makeQuery(id+"F0.imprint","IMPRINT",FACE,{"disambiguationData":[TD([[makeQuery(id+"F0.imprint","IMPRINT",EDGE,{"derivedFrom":sQuery(id+"F0.wireOp",EDGE,"E79.MirrorCS")}),1.0]])]});
            var Q34;
            {var subQ0=sQuery(id+"F0.wireOp",EDGE,"E76.left");Q34=makeQuery(id+"F0.imprint","IMPRINT",FACE,{"disambiguationData":[TD([[makeQuery(id+"F0.imprint","IMPRINT",EDGE,{"derivedFrom":subQ0}),1.0]])]});}
            var Q35;
            {var subQ1=sQuery(id+"F0.wireOp",EDGE,"E76.right");Q35=makeQuery(id+"F0.imprint","IMPRINT",FACE,{"disambiguationData":[TD([[makeQuery(id+"F0.imprint","IMPRINT",EDGE,{"derivedFrom":subQ1}),-1.0]])]});}
            var Q36;
            Q36=makeQuery(id+"F0.imprint","IMPRINT",FACE,{"disambiguationData":[TD([[makeQuery(id+"F0.imprint","IMPRINT",EDGE,{"derivedFrom":sQuery(id+"F0.wireOp",EDGE,"cd6a4581-39f0-41a9-89f3-eec7f9657f8e.MirrorC")}),1.0]])]});
            var Q37;
            Q37=makeQuery(id+"F0.imprint","IMPRINT",FACE,{"disambiguationData":[TD([[makeQuery(id+"F0.imprint","IMPRINT",EDGE,{"derivedFrom":sQuery(id+"F0.wireOp",EDGE,"f61199a6-9bd4-40db-99d5-838ce8c4140d.MirrorC")}),-1.0]])]});
            var Q38;
            Q38=makeQuery(id+"F0.imprint","IMPRINT",FACE,{"disambiguationData":[TD([[makeQuery(id+"F0.imprint","IMPRINT",EDGE,{"derivedFrom":sQuery(id+"F0.wireOp",EDGE,"ed612093-3e78-479f-b3c7-dd08aea9376b.MirrorC")}),-1.0]])]});
            var Q39;
            Q39=makeQuery(id+"F0.imprint","IMPRINT",FACE,{"disambiguationData":[TD([[makeQuery(id+"F0.imprint","IMPRINT",EDGE,{"derivedFrom":sQuery(id+"F0.wireOp",EDGE,"79d72fee-5c57-43ab-89ce-cfacb674b62a")}),1.0]])]});
            var Q40;
            {var subQ1=sQuery(id+"F0.wireOp",EDGE,"E92.right");Q40=makeQuery(id+"F0.imprint","IMPRINT",FACE,{"disambiguationData":[TD([[makeQuery(id+"F0.imprint","IMPRINT",EDGE,{"derivedFrom":subQ1}),-1.0]])]});}
            var Q41;
            {var subQ1=sQuery(id+"F0.wireOp",EDGE,"E92.left");Q41=makeQuery(id+"F0.imprint","IMPRINT",FACE,{"disambiguationData":[TD([[makeQuery(id+"F0.imprint","IMPRINT",EDGE,{"derivedFrom":subQ1}),-1.0]])]});}
            var Q42;
            Q42=makeQuery(id+"F0.imprint","IMPRINT",FACE,{"disambiguationData":[TD([[makeQuery(id+"F0.imprint","IMPRINT",EDGE,{"derivedFrom":sQuery(id+"F0.wireOp",EDGE,"E95.MirrorCS")}),1.0]])]});
            var Q43;
            Q43=makeQuery(id+"F0.imprint","IMPRINT",FACE,{"disambiguationData":[TD([[makeQuery(id+"F0.imprint","IMPRINT",EDGE,{"derivedFrom":sQuery(id+"F0.wireOp",EDGE,"E103")}),1.0]])]});
            var Q44;
            Q44=makeQuery(id+"F0.imprint","IMPRINT",FACE,{"disambiguationData":[TD([[makeQuery(id+"F0.imprint","IMPRINT",EDGE,{"derivedFrom":sQuery(id+"F0.wireOp",EDGE,"E105")}),-1.0]])]});
            var Q45;
            Q45=makeQuery(id+"F0.imprint","IMPRINT",FACE,{"disambiguationData":[TD([[makeQuery(id+"F0.imprint","IMPRINT",EDGE,{"derivedFrom":sQuery(id+"F0.wireOp",EDGE,"E107")}),-1.0]])]});
            var Q46;
            Q46=makeQuery(id+"F0.imprint","IMPRINT",FACE,{"disambiguationData":[TD([[makeQuery(id+"F0.imprint","IMPRINT",EDGE,{"derivedFrom":sQuery(id+"F0.wireOp",EDGE,"E106")}),1.0]])]});
            var Q47;
            {var subQ0=sQuery(id+"F0.wireOp",EDGE,"E92.left");Q47=makeQuery(id+"F0.imprint","IMPRINT",FACE,{"disambiguationData":[TD([[makeQuery(id+"F0.imprint","IMPRINT",EDGE,{"derivedFrom":subQ0}),1.0]])]});}
            var Q48;
            Q48=makeQuery(id+"F0.imprint","IMPRINT",FACE,{"disambiguationData":[TD([[makeQuery(id+"F0.imprint","IMPRINT",EDGE,{"derivedFrom":sQuery(id+"F0.wireOp",EDGE,"fca2dfff-7623-45b0-bbce-eb93675da3a8.MirrorC")}),-1.0]])]});
            var Q49;
            Q49=makeQuery(id+"F0.imprint","IMPRINT",FACE,{"disambiguationData":[TD([[makeQuery(id+"F0.imprint","IMPRINT",EDGE,{"derivedFrom":sQuery(id+"F0.wireOp",EDGE,"346b0c9b-f031-4a8f-ae90-6d73ea8d3143.MirrorC")}),1.0]])]});
            var Q50;
            Q50=makeQuery(id+"F0.imprint","IMPRINT",FACE,{"disambiguationData":[TD([[makeQuery(id+"F0.imprint","IMPRINT",EDGE,{"derivedFrom":sQuery(id+"F0.wireOp",EDGE,"052349c2-b7bf-4fa4-ab4a-60abaacbaca7")}),1.0]])]});
            var Q51;
            Q51=makeQuery(id+"F0.imprint","IMPRINT",FACE,{"disambiguationData":[TD([[makeQuery(id+"F0.imprint","IMPRINT",EDGE,{"derivedFrom":sQuery(id+"F0.wireOp",EDGE,"c45039b2-2c3b-486d-bf61-685492c25083.MirrorC")}),-1.0]])]});
            var Q52;
            {var subQ1=sQuery(id+"F0.wireOp",EDGE,"E118.left");Q52=makeQuery(id+"F0.imprint","IMPRINT",FACE,{"disambiguationData":[TD([[makeQuery(id+"F0.imprint","IMPRINT",EDGE,{"derivedFrom":subQ1}),-1.0]])]});}
            var Q53;
            Q53=makeQuery(id+"F0.imprint","IMPRINT",FACE,{"disambiguationData":[TD([[makeQuery(id+"F0.imprint","IMPRINT",EDGE,{"derivedFrom":sQuery(id+"F0.wireOp",EDGE,"E126")}),1.0]])]});
            var Q54;
            {var subQ1=sQuery(id+"F0.wireOp",EDGE,"E121");Q54=makeQuery(id+"F0.imprint","IMPRINT",FACE,{"disambiguationData":[TD([[makeQuery(id+"F0.imprint","IMPRINT",EDGE,{"derivedFrom":subQ1}),1.0]])]});}
            var Q55;
            {var subQ1=sQuery(id+"F0.wireOp",EDGE,"E118.left");Q55=makeQuery(id+"F0.imprint","IMPRINT",FACE,{"disambiguationData":[TD([[makeQuery(id+"F0.imprint","IMPRINT",EDGE,{"derivedFrom":subQ1}),1.0]])]});}
            var Q56;
            {var subQ1=sQuery(id+"F0.wireOp",EDGE,"E118.right");Q56=makeQuery(id+"F0.imprint","IMPRINT",FACE,{"disambiguationData":[TD([[makeQuery(id+"F0.imprint","IMPRINT",EDGE,{"derivedFrom":subQ1}),-1.0]])]});}
            var Q57;
            Q57=makeQuery(id+"F0.imprint","IMPRINT",FACE,{"disambiguationData":[TD([[makeQuery(id+"F0.imprint","IMPRINT",EDGE,{"derivedFrom":sQuery(id+"F0.wireOp",EDGE,"E129.MirrorC")}),-1.0]])]});
            var Q58;
            Q58=makeQuery(id+"F0.imprint","IMPRINT",FACE,{"disambiguationData":[TD([[makeQuery(id+"F0.imprint","IMPRINT",EDGE,{"derivedFrom":sQuery(id+"F0.wireOp",EDGE,"E131.MirrorC")}),1.0]])]});
            var Q59;
            Q59=makeQuery(id+"F0.imprint","IMPRINT",FACE,{"disambiguationData":[TD([[makeQuery(id+"F0.imprint","IMPRINT",EDGE,{"derivedFrom":sQuery(id+"F0.wireOp",EDGE,"E130.MirrorC")}),-1.0]])]});
            var Q60;
            Q60=makeQuery(id+"F0.imprint","IMPRINT",FACE,{"disambiguationData":[TD([[makeQuery(id+"F0.imprint","IMPRINT",EDGE,{"derivedFrom":sQuery(id+"F0.wireOp",EDGE,"E132.MirrorC")}),1.0]])]});
            var Q61;
            Q61=makeQuery(id+"F0.imprint","IMPRINT",FACE,{"disambiguationData":[TD([[makeQuery(id+"F0.imprint","IMPRINT",EDGE,{"derivedFrom":sQuery(id+"F0.wireOp",EDGE,"E135.MirrorC")}),-1.0]])]});
            var Q62;
            Q62=makeQuery(id+"F0.imprint","IMPRINT",FACE,{"disambiguationData":[TD([[makeQuery(id+"F0.imprint","IMPRINT",EDGE,{"derivedFrom":sQuery(id+"F0.wireOp",EDGE,"E133.MirrorC")}),-1.0]])]});
            var Q63;
            Q63=makeQuery(id+"F0.imprint","IMPRINT",FACE,{"disambiguationData":[TD([[makeQuery(id+"F0.imprint","IMPRINT",EDGE,{"derivedFrom":sQuery(id+"F0.wireOp",EDGE,"E134.MirrorC")}),1.0]])]});
            var Q64;
            Q64=makeQuery(id+"F0.imprint","IMPRINT",FACE,{"disambiguationData":[TD([[makeQuery(id+"F0.imprint","IMPRINT",EDGE,{"derivedFrom":sQuery(id+"F0.wireOp",EDGE,"E137.MirrorC")}),1.0]])]});
            var Q65;
            Q65=makeQuery(id+"F0.imprint","IMPRINT",FACE,{"disambiguationData":[TD([[makeQuery(id+"F0.imprint","IMPRINT",EDGE,{"derivedFrom":sQuery(id+"F0.wireOp",EDGE,"E136.MirrorC")}),-1.0]])]});
            var Q66;
            Q66=makeQuery(id+"F0.imprint","IMPRINT",FACE,{"disambiguationData":[TD([[makeQuery(id+"F0.imprint","IMPRINT",EDGE,{"derivedFrom":sQuery(id+"F0.wireOp",EDGE,"E140.MirrorC")}),1.0]])]});
            var Q67;
            Q67=makeQuery(id+"F0.imprint","IMPRINT",FACE,{"disambiguationData":[TD([[makeQuery(id+"F0.imprint","IMPRINT",EDGE,{"derivedFrom":sQuery(id+"F0.wireOp",EDGE,"E141.MirrorC")}),-1.0]])]});
            var Q68;
            Q68=makeQuery(id+"F0.imprint","IMPRINT",FACE,{"disambiguationData":[TD([[makeQuery(id+"F0.imprint","IMPRINT",EDGE,{"derivedFrom":sQuery(id+"F0.wireOp",EDGE,"E138.MirrorC")}),-1.0]])]});
            var Q69;
            Q69=makeQuery(id+"F0.imprint","IMPRINT",FACE,{"disambiguationData":[TD([[makeQuery(id+"F0.imprint","IMPRINT",EDGE,{"derivedFrom":sQuery(id+"F0.wireOp",EDGE,"E139.MirrorC")}),1.0]])]});
            var Q70;
            Q70=makeQuery(id+"F0.imprint","IMPRINT",FACE,{"disambiguationData":[TD([[makeQuery(id+"F0.imprint","IMPRINT",EDGE,{"derivedFrom":sQuery(id+"F0.wireOp",EDGE,"E143.MirrorC")}),-1.0]])]});
            var Q71;
            Q71=makeQuery(id+"F0.imprint","IMPRINT",FACE,{"disambiguationData":[TD([[makeQuery(id+"F0.imprint","IMPRINT",EDGE,{"derivedFrom":sQuery(id+"F0.wireOp",EDGE,"E142.MirrorC")}),1.0]])]});
            var Q72;
            Q72=sQuery(id+"F0.wireOp",EDGE,"E1.left");
            var Q73;
            Q73=sQuery(id+"F0.wireOp",EDGE,"E1.bottom");
            var Q74;
            Q74=sQuery(id+"F0.wireOp",EDGE,"E1.top");
            var Q75;
            Q75=sQuery(id+"F0.wireOp",EDGE,"E1.right");
            extrude(context, id + "F5", {"entities" : qUnion([Q0, Q1, Q2, Q3, Q4, Q5, Q6, Q7, Q8, Q9, Q10, Q11, Q12, Q13, Q14, Q15, Q16, Q17, Q18, Q19, Q20, Q21, Q22, Q23, Q24, Q25, Q26, Q27, Q28, Q29, Q30, Q31, Q32, Q33, Q34, Q35, Q36, Q37, Q38, Q39, Q40, Q41, Q42, Q43, Q44, Q45, Q46, Q47, Q48, Q49, Q50, Q51, Q52, Q53, Q54, Q55, Q56, Q57, Q58, Q59, Q60, Q61, Q62, Q63, Q64, Q65, Q66, Q67, Q68, Q69, Q70, Q71]), "operationType" : NewBodyOperationType.ADD, "surfaceEntities" : qUnion([Q72, Q73, Q74, Q75]), "depth" : 5 * mm, "offsetDistance" : 25 * mm});
        }
        {
            var Q0;
            Q0=makeQuery(id+"F2.opExtrude","SWEPT_BODY",BODY,{"disambiguationData":[OSD([sQuery(id+"F0.wireOp",EDGE,"ccb5a7b4-4bd2-4bd8-aee6-5957949556a70.MirrorC")])]});
            var Q1;
            Q1=makeQuery(id+"F3.opExtrude","SWEPT_BODY",BODY,{"disambiguationData":[OSD([sQuery(id+"F0.wireOp",EDGE,"E3"),sQuery(id+"F0.wireOp",EDGE,"E4"),sQuery(id+"F0.wireOp",EDGE,"E5"),sQuery(id+"F0.wireOp",EDGE,"E66")])]});
            var Q2;
            Q2=makeQuery(id+"F3.opExtrude","SWEPT_BODY",BODY,{"disambiguationData":[OSD([sQuery(id+"F0.wireOp",EDGE,"E13"),sQuery(id+"F0.wireOp",EDGE,"E14"),sQuery(id+"F0.wireOp",EDGE,"E15"),sQuery(id+"F0.wireOp",EDGE,"E16")])]});
            var Q3;
            Q3=makeQuery(id+"F3.opExtrude","SWEPT_BODY",BODY,{"disambiguationData":[OSD([sQuery(id+"F0.wireOp",EDGE,"E8"),sQuery(id+"F0.wireOp",EDGE,"E12"),sQuery(id+"F0.wireOp",EDGE,"E63"),sQuery(id+"F0.wireOp",EDGE,"E67")])]});
            var Q4;
            Q4=makeQuery(id+"F3.opExtrude","SWEPT_BODY",BODY,{"disambiguationData":[OSD([sQuery(id+"F0.wireOp",EDGE,"E17"),sQuery(id+"F0.wireOp",EDGE,"E18"),sQuery(id+"F0.wireOp",EDGE,"E19"),sQuery(id+"F0.wireOp",EDGE,"E20")])]});
            var Q5;
            Q5=makeQuery(id+"F3.opExtrude","SWEPT_BODY",BODY,{"disambiguationData":[OSD([sQuery(id+"F0.wireOp",EDGE,"E25"),sQuery(id+"F0.wireOp",EDGE,"E26"),sQuery(id+"F0.wireOp",EDGE,"E27"),sQuery(id+"F0.wireOp",EDGE,"E28")])]});
            var Q6;
            Q6=makeQuery(id+"F3.opExtrude","SWEPT_BODY",BODY,{"disambiguationData":[OSD([sQuery(id+"F0.wireOp",EDGE,"E33"),sQuery(id+"F0.wireOp",EDGE,"E34"),sQuery(id+"F0.wireOp",EDGE,"E35"),sQuery(id+"F0.wireOp",EDGE,"E36")])]});
            var Q7;
            Q7=makeQuery(id+"F3.opExtrude","SWEPT_BODY",BODY,{"disambiguationData":[OSD([sQuery(id+"F0.wireOp",EDGE,"E7"),sQuery(id+"F0.wireOp",EDGE,"E11"),sQuery(id+"F0.wireOp",EDGE,"E61"),sQuery(id+"F0.wireOp",EDGE,"E62")])]});
            var Q8;
            Q8=makeQuery(id+"F3.opExtrude","SWEPT_BODY",BODY,{"disambiguationData":[OSD([sQuery(id+"F0.wireOp",EDGE,"E6"),sQuery(id+"F0.wireOp",EDGE,"E9"),sQuery(id+"F0.wireOp",EDGE,"E64"),sQuery(id+"F0.wireOp",EDGE,"E65")])]});
            var Q9;
            Q9=makeQuery(id+"F3.opExtrude","SWEPT_BODY",BODY,{"disambiguationData":[OSD([sQuery(id+"F0.wireOp",EDGE,"E0.bottom"),sQuery(id+"F0.wireOp",EDGE,"E0.top"),sQuery(id+"F0.wireOp",EDGE,"E0.right"),sQuery(id+"F0.wireOp",EDGE,"E68"),sQuery(id+"F0.wireOp",EDGE,"E71.MirrorCS"),sQuery(id+"F0.wireOp",EDGE,"E73"),sQuery(id+"F0.wireOp",EDGE,"E75"),sQuery(id+"F0.wireOp",EDGE,"edaaeaec-2fa2-4ac8-96e5-24b6cc5294a60.MirrorC"),sQuery(id+"F0.wireOp",EDGE,"ccb5a7b4-4bd2-4bd8-aee6-5957949556a70.MirrorC")])]});
            var Q10;
            Q10=makeQuery(id+"F2.opExtrude","SWEPT_BODY",BODY,{"disambiguationData":[OSD([sQuery(id+"F0.wireOp",EDGE,"W2vNM0GE-2OHP-QNdi-PDCA-W7E0gAEi5RRH")])]});
            var Q11;
            Q11=makeQuery(id+"F3.opExtrude","SWEPT_BODY",BODY,{"disambiguationData":[OSD([sQuery(id+"F0.wireOp",EDGE,"E0.bottom"),sQuery(id+"F0.wireOp",EDGE,"E0.top"),sQuery(id+"F0.wireOp",EDGE,"E0.left"),sQuery(id+"F0.wireOp",EDGE,"E69"),sQuery(id+"F0.wireOp",EDGE,"E70.MirrorCS"),sQuery(id+"F0.wireOp",EDGE,"E72"),sQuery(id+"F0.wireOp",EDGE,"E74"),sQuery(id+"F0.wireOp",EDGE,"W2vNM0GE-2OHP-QNdi-PDCA-W7E0gAEi5RRH"),sQuery(id+"F0.wireOp",EDGE,"0858af88-9474-4ed9-898e-377d812cf8890.MirrorC")])]});
            var Q12;
            Q12=makeQuery(id+"F3.opExtrude","SWEPT_BODY",BODY,{"disambiguationData":[OSD([sQuery(id+"F0.wireOp",EDGE,"E57"),sQuery(id+"F0.wireOp",EDGE,"E58"),sQuery(id+"F0.wireOp",EDGE,"E59"),sQuery(id+"F0.wireOp",EDGE,"E60")])]});
            var Q13;
            Q13=makeQuery(id+"F2.opExtrude","SWEPT_BODY",BODY,{"disambiguationData":[OSD([sQuery(id+"F0.wireOp",EDGE,"E0.bottom"),sQuery(id+"F0.wireOp",EDGE,"E0.top"),sQuery(id+"F0.wireOp",EDGE,"E0.left"),sQuery(id+"F0.wireOp",EDGE,"E0.right"),sQuery(id+"F0.wireOp",EDGE,"E1.bottom"),sQuery(id+"F0.wireOp",EDGE,"E1.top"),sQuery(id+"F0.wireOp",EDGE,"E1.left"),sQuery(id+"F0.wireOp",EDGE,"E1.right")])]});
            var Q14;
            Q14=makeQuery(id+"F3.opExtrude","SWEPT_BODY",BODY,{"disambiguationData":[OSD([sQuery(id+"F0.wireOp",EDGE,"E29"),sQuery(id+"F0.wireOp",EDGE,"E30"),sQuery(id+"F0.wireOp",EDGE,"E31"),sQuery(id+"F0.wireOp",EDGE,"E32")])]});
            var Q15;
            Q15=makeQuery(id+"F3.opExtrude","SWEPT_BODY",BODY,{"disambiguationData":[OSD([sQuery(id+"F0.wireOp",EDGE,"E37"),sQuery(id+"F0.wireOp",EDGE,"E38"),sQuery(id+"F0.wireOp",EDGE,"E39"),sQuery(id+"F0.wireOp",EDGE,"E40")])]});
            var Q16;
            Q16=makeQuery(id+"F3.opExtrude","SWEPT_BODY",BODY,{"disambiguationData":[OSD([sQuery(id+"F0.wireOp",EDGE,"E21"),sQuery(id+"F0.wireOp",EDGE,"E22"),sQuery(id+"F0.wireOp",EDGE,"E23"),sQuery(id+"F0.wireOp",EDGE,"E24")])]});
            var Q17;
            Q17=makeQuery(id+"F3.opExtrude","SWEPT_BODY",BODY,{"disambiguationData":[OSD([sQuery(id+"F0.wireOp",EDGE,"E53"),sQuery(id+"F0.wireOp",EDGE,"E54"),sQuery(id+"F0.wireOp",EDGE,"E55"),sQuery(id+"F0.wireOp",EDGE,"E56")])]});
            var Q18;
            Q18=makeQuery(id+"F3.opExtrude","SWEPT_BODY",BODY,{"disambiguationData":[OSD([sQuery(id+"F0.wireOp",EDGE,"E41"),sQuery(id+"F0.wireOp",EDGE,"E42"),sQuery(id+"F0.wireOp",EDGE,"E43"),sQuery(id+"F0.wireOp",EDGE,"E44")])]});
            var Q19;
            Q19=makeQuery(id+"F3.opExtrude","SWEPT_BODY",BODY,{"disambiguationData":[OSD([sQuery(id+"F0.wireOp",EDGE,"E49"),sQuery(id+"F0.wireOp",EDGE,"E50"),sQuery(id+"F0.wireOp",EDGE,"E51"),sQuery(id+"F0.wireOp",EDGE,"E52")])]});
            var Q20;
            Q20=makeQuery(id+"F3.opExtrude","SWEPT_BODY",BODY,{"disambiguationData":[OSD([sQuery(id+"F0.wireOp",EDGE,"E45"),sQuery(id+"F0.wireOp",EDGE,"E46"),sQuery(id+"F0.wireOp",EDGE,"E47"),sQuery(id+"F0.wireOp",EDGE,"E48")])]});
            var Q21;
            Q21=makeQuery(id+"F3.opExtrude","SWEPT_BODY",BODY,{"disambiguationData":[OSD([sQuery(id+"F0.wireOp",EDGE,"E0.bottom"),sQuery(id+"F0.wireOp",EDGE,"E0.top"),sQuery(id+"F0.wireOp",EDGE,"E3"),sQuery(id+"F0.wireOp",EDGE,"E4"),sQuery(id+"F0.wireOp",EDGE,"E5"),sQuery(id+"F0.wireOp",EDGE,"E6"),sQuery(id+"F0.wireOp",EDGE,"E7"),sQuery(id+"F0.wireOp",EDGE,"E8"),sQuery(id+"F0.wireOp",EDGE,"E9"),sQuery(id+"F0.wireOp",EDGE,"E11"),sQuery(id+"F0.wireOp",EDGE,"E12"),sQuery(id+"F0.wireOp",EDGE,"E13"),sQuery(id+"F0.wireOp",EDGE,"E14"),sQuery(id+"F0.wireOp",EDGE,"E15"),sQuery(id+"F0.wireOp",EDGE,"E16"),sQuery(id+"F0.wireOp",EDGE,"E17"),sQuery(id+"F0.wireOp",EDGE,"E18"),sQuery(id+"F0.wireOp",EDGE,"E19"),sQuery(id+"F0.wireOp",EDGE,"E20"),sQuery(id+"F0.wireOp",EDGE,"E21"),sQuery(id+"F0.wireOp",EDGE,"E22"),sQuery(id+"F0.wireOp",EDGE,"E23"),sQuery(id+"F0.wireOp",EDGE,"E24"),sQuery(id+"F0.wireOp",EDGE,"E25"),sQuery(id+"F0.wireOp",EDGE,"E26"),sQuery(id+"F0.wireOp",EDGE,"E27"),sQuery(id+"F0.wireOp",EDGE,"E28"),sQuery(id+"F0.wireOp",EDGE,"E29"),sQuery(id+"F0.wireOp",EDGE,"E30"),sQuery(id+"F0.wireOp",EDGE,"E31"),sQuery(id+"F0.wireOp",EDGE,"E32"),sQuery(id+"F0.wireOp",EDGE,"E33"),sQuery(id+"F0.wireOp",EDGE,"E34"),sQuery(id+"F0.wireOp",EDGE,"E35"),sQuery(id+"F0.wireOp",EDGE,"E36"),sQuery(id+"F0.wireOp",EDGE,"E37"),sQuery(id+"F0.wireOp",EDGE,"E38"),sQuery(id+"F0.wireOp",EDGE,"E39"),sQuery(id+"F0.wireOp",EDGE,"E40"),sQuery(id+"F0.wireOp",EDGE,"E41"),sQuery(id+"F0.wireOp",EDGE,"E42"),sQuery(id+"F0.wireOp",EDGE,"E43"),sQuery(id+"F0.wireOp",EDGE,"E44"),sQuery(id+"F0.wireOp",EDGE,"E45"),sQuery(id+"F0.wireOp",EDGE,"E46"),sQuery(id+"F0.wireOp",EDGE,"E47"),sQuery(id+"F0.wireOp",EDGE,"E48"),sQuery(id+"F0.wireOp",EDGE,"E49"),sQuery(id+"F0.wireOp",EDGE,"E50"),sQuery(id+"F0.wireOp",EDGE,"E51"),sQuery(id+"F0.wireOp",EDGE,"E52"),sQuery(id+"F0.wireOp",EDGE,"E53"),sQuery(id+"F0.wireOp",EDGE,"E54"),sQuery(id+"F0.wireOp",EDGE,"E55"),sQuery(id+"F0.wireOp",EDGE,"E56"),sQuery(id+"F0.wireOp",EDGE,"E57"),sQuery(id+"F0.wireOp",EDGE,"E58"),sQuery(id+"F0.wireOp",EDGE,"E59"),sQuery(id+"F0.wireOp",EDGE,"E60"),sQuery(id+"F0.wireOp",EDGE,"E61"),sQuery(id+"F0.wireOp",EDGE,"E62"),sQuery(id+"F0.wireOp",EDGE,"E63"),sQuery(id+"F0.wireOp",EDGE,"E64"),sQuery(id+"F0.wireOp",EDGE,"E65"),sQuery(id+"F0.wireOp",EDGE,"E66"),sQuery(id+"F0.wireOp",EDGE,"E67"),sQuery(id+"F0.wireOp",EDGE,"E68"),sQuery(id+"F0.wireOp",EDGE,"E69"),sQuery(id+"F0.wireOp",EDGE,"E70.MirrorCS"),sQuery(id+"F0.wireOp",EDGE,"E71.MirrorCS"),sQuery(id+"F0.wireOp",EDGE,"E72"),sQuery(id+"F0.wireOp",EDGE,"E73"),sQuery(id+"F0.wireOp",EDGE,"E74"),sQuery(id+"F0.wireOp",EDGE,"E75")])]});
            var Q22;
            Q22=makeQuery(id+"F1.opExtrude","SWEPT_BODY",BODY,{"disambiguationData":[OSD([sQuery(id+"F0.wireOp",EDGE,"E0.bottom"),sQuery(id+"F0.wireOp",EDGE,"E0.top"),sQuery(id+"F0.wireOp",EDGE,"E3"),sQuery(id+"F0.wireOp",EDGE,"E4"),sQuery(id+"F0.wireOp",EDGE,"E5"),sQuery(id+"F0.wireOp",EDGE,"E6"),sQuery(id+"F0.wireOp",EDGE,"E7"),sQuery(id+"F0.wireOp",EDGE,"E8"),sQuery(id+"F0.wireOp",EDGE,"E9"),sQuery(id+"F0.wireOp",EDGE,"E11"),sQuery(id+"F0.wireOp",EDGE,"E12"),sQuery(id+"F0.wireOp",EDGE,"E13"),sQuery(id+"F0.wireOp",EDGE,"E14"),sQuery(id+"F0.wireOp",EDGE,"E15"),sQuery(id+"F0.wireOp",EDGE,"E16"),sQuery(id+"F0.wireOp",EDGE,"E17"),sQuery(id+"F0.wireOp",EDGE,"E18"),sQuery(id+"F0.wireOp",EDGE,"E19"),sQuery(id+"F0.wireOp",EDGE,"E20"),sQuery(id+"F0.wireOp",EDGE,"E21"),sQuery(id+"F0.wireOp",EDGE,"E22"),sQuery(id+"F0.wireOp",EDGE,"E23"),sQuery(id+"F0.wireOp",EDGE,"E24"),sQuery(id+"F0.wireOp",EDGE,"E25"),sQuery(id+"F0.wireOp",EDGE,"E26"),sQuery(id+"F0.wireOp",EDGE,"E27"),sQuery(id+"F0.wireOp",EDGE,"E28"),sQuery(id+"F0.wireOp",EDGE,"E29"),sQuery(id+"F0.wireOp",EDGE,"E30"),sQuery(id+"F0.wireOp",EDGE,"E31"),sQuery(id+"F0.wireOp",EDGE,"E32"),sQuery(id+"F0.wireOp",EDGE,"E33"),sQuery(id+"F0.wireOp",EDGE,"E34"),sQuery(id+"F0.wireOp",EDGE,"E35"),sQuery(id+"F0.wireOp",EDGE,"E36"),sQuery(id+"F0.wireOp",EDGE,"E37"),sQuery(id+"F0.wireOp",EDGE,"E38"),sQuery(id+"F0.wireOp",EDGE,"E39"),sQuery(id+"F0.wireOp",EDGE,"E40"),sQuery(id+"F0.wireOp",EDGE,"E41"),sQuery(id+"F0.wireOp",EDGE,"E42"),sQuery(id+"F0.wireOp",EDGE,"E43"),sQuery(id+"F0.wireOp",EDGE,"E44"),sQuery(id+"F0.wireOp",EDGE,"E45"),sQuery(id+"F0.wireOp",EDGE,"E46"),sQuery(id+"F0.wireOp",EDGE,"E47"),sQuery(id+"F0.wireOp",EDGE,"E48"),sQuery(id+"F0.wireOp",EDGE,"E49"),sQuery(id+"F0.wireOp",EDGE,"E50"),sQuery(id+"F0.wireOp",EDGE,"E51"),sQuery(id+"F0.wireOp",EDGE,"E52"),sQuery(id+"F0.wireOp",EDGE,"E53"),sQuery(id+"F0.wireOp",EDGE,"E54"),sQuery(id+"F0.wireOp",EDGE,"E55"),sQuery(id+"F0.wireOp",EDGE,"E56"),sQuery(id+"F0.wireOp",EDGE,"E57"),sQuery(id+"F0.wireOp",EDGE,"E58"),sQuery(id+"F0.wireOp",EDGE,"E59"),sQuery(id+"F0.wireOp",EDGE,"E60"),sQuery(id+"F0.wireOp",EDGE,"E61"),sQuery(id+"F0.wireOp",EDGE,"E62"),sQuery(id+"F0.wireOp",EDGE,"E63"),sQuery(id+"F0.wireOp",EDGE,"E64"),sQuery(id+"F0.wireOp",EDGE,"E65"),sQuery(id+"F0.wireOp",EDGE,"E66"),sQuery(id+"F0.wireOp",EDGE,"E67"),sQuery(id+"F0.wireOp",EDGE,"E68"),sQuery(id+"F0.wireOp",EDGE,"E69"),sQuery(id+"F0.wireOp",EDGE,"E70.MirrorCS"),sQuery(id+"F0.wireOp",EDGE,"E71.MirrorCS"),sQuery(id+"F0.wireOp",EDGE,"E72"),sQuery(id+"F0.wireOp",EDGE,"E73"),sQuery(id+"F0.wireOp",EDGE,"E74"),sQuery(id+"F0.wireOp",EDGE,"E75")])]});
            var Q23;
            Q23=makeQuery(id+"F2.opExtrude","SWEPT_BODY",BODY,{"disambiguationData":[OSD([sQuery(id+"F0.wireOp",EDGE,"edaaeaec-2fa2-4ac8-96e5-24b6cc5294a60.MirrorC")])]});
            var Q24;
            {var subQ0=sQuery(id+"F0.wireOp",EDGE,"E1.right");Q24=makeQuery(id+"F5.boolean.opBoolean","MERGE",FACE,{"derivedFrom":[makeQuery(id+"F2.opExtrude","SWEPT_FACE",FACE,{"disambiguationData":[OSD([subQ0])]}),makeQuery(id+"F5.opExtrude","SWEPT_FACE",FACE,{"disambiguationData":[OSD([subQ0])]})]});}
            mirror(context, id + "F6", {"operationType" : NewBodyOperationType.ADD, "entities" : qUnion([Q0, Q1, Q2, Q3, Q4, Q5, Q6, Q7, Q8, Q9, Q10, Q11, Q12, Q13, Q14, Q15, Q16, Q17, Q18, Q19, Q20, Q21, Q22, Q23]), "mirrorPlane" : qUnion([Q24])});
        }
        {
            var Q0;
            Q0=makeQuery(id+"F1.opExtrude","SWEPT_BODY",BODY,{"disambiguationData":[OSD([sQuery(id+"F0.wireOp",EDGE,"E76.bottom"),sQuery(id+"F0.wireOp",EDGE,"E76.top"),sQuery(id+"F0.wireOp",EDGE,"E79.MirrorCS"),sQuery(id+"F0.wireOp",EDGE,"E80"),sQuery(id+"F0.wireOp",EDGE,"E81"),sQuery(id+"F0.wireOp",EDGE,"E82"),sQuery(id+"F0.wireOp",EDGE,"E83"),sQuery(id+"F0.wireOp",EDGE,"E85"),sQuery(id+"F0.wireOp",EDGE,"E86.MirrorCS"),sQuery(id+"F0.wireOp",EDGE,"E87.MirrorCS"),sQuery(id+"F0.wireOp",EDGE,"E88.MirrorCS"),sQuery(id+"F0.wireOp",EDGE,"E89.MirrorCS"),sQuery(id+"F0.wireOp",EDGE,"E90.MirrorCS"),sQuery(id+"F0.wireOp",EDGE,"E91.MirrorCS")])]});
            var Q1;
            Q1=makeQuery(id+"F3.opExtrude","SWEPT_BODY",BODY,{"disambiguationData":[OSD([sQuery(id+"F0.wireOp",EDGE,"E76.bottom"),sQuery(id+"F0.wireOp",EDGE,"E76.top"),sQuery(id+"F0.wireOp",EDGE,"E79.MirrorCS"),sQuery(id+"F0.wireOp",EDGE,"E80"),sQuery(id+"F0.wireOp",EDGE,"E81"),sQuery(id+"F0.wireOp",EDGE,"E82"),sQuery(id+"F0.wireOp",EDGE,"E83"),sQuery(id+"F0.wireOp",EDGE,"E85"),sQuery(id+"F0.wireOp",EDGE,"E86.MirrorCS"),sQuery(id+"F0.wireOp",EDGE,"E87.MirrorCS"),sQuery(id+"F0.wireOp",EDGE,"E88.MirrorCS"),sQuery(id+"F0.wireOp",EDGE,"E89.MirrorCS"),sQuery(id+"F0.wireOp",EDGE,"E90.MirrorCS"),sQuery(id+"F0.wireOp",EDGE,"E91.MirrorCS")])]});
            var Q2;
            {var subQ0=sQuery(id+"F0.wireOp",EDGE,"E77.left");Q2=makeQuery(id+"F5.boolean.opBoolean","MERGE",FACE,{"derivedFrom":[makeQuery(id+"F2.opExtrude","SWEPT_FACE",FACE,{"disambiguationData":[OSD([subQ0])]}),makeQuery(id+"F5.opExtrude","SWEPT_FACE",FACE,{"disambiguationData":[OSD([subQ0])]})]});}
            mirror(context, id + "F7", {"operationType" : NewBodyOperationType.ADD, "entities" : qUnion([Q0, Q1]), "mirrorPlane" : qUnion([Q2])});
        }
        {
            var Q0;
            Q0=makeQuery(id+"F3.opExtrude","SWEPT_BODY",BODY,{"disambiguationData":[OSD([sQuery(id+"F0.wireOp",EDGE,"E92.bottom"),sQuery(id+"F0.wireOp",EDGE,"E92.top"),sQuery(id+"F0.wireOp",EDGE,"E95.MirrorCS"),sQuery(id+"F0.wireOp",EDGE,"E96"),sQuery(id+"F0.wireOp",EDGE,"E97"),sQuery(id+"F0.wireOp",EDGE,"E98"),sQuery(id+"F0.wireOp",EDGE,"E99"),sQuery(id+"F0.wireOp",EDGE,"E100"),sQuery(id+"F0.wireOp",EDGE,"E101.MirrorCS"),sQuery(id+"F0.wireOp",EDGE,"E102.MirrorCS"),sQuery(id+"F0.wireOp",EDGE,"E103"),sQuery(id+"F0.wireOp",EDGE,"04NsANdn-taOn-ddKp-MDbT-y7dXd8gmv4Cl"),sQuery(id+"F0.wireOp",EDGE,"E104"),sQuery(id+"F0.wireOp",EDGE,"3R8MwXPY-31j6-GvAs-L5bG-rwEBLL8UpWRA"),sQuery(id+"F0.wireOp",EDGE,"E105"),sQuery(id+"F0.wireOp",EDGE,"E106"),sQuery(id+"F0.wireOp",EDGE,"E107"),sQuery(id+"F0.wireOp",EDGE,"E108"),sQuery(id+"F0.wireOp",EDGE,"E109"),sQuery(id+"F0.wireOp",EDGE,"E110"),sQuery(id+"F0.wireOp",EDGE,"E111"),sQuery(id+"F0.wireOp",EDGE,"E112"),sQuery(id+"F0.wireOp",EDGE,"E113.right"),sQuery(id+"F0.wireOp",EDGE,"E113.left"),sQuery(id+"F0.wireOp",EDGE,"E114"),sQuery(id+"F0.wireOp",EDGE,"E115"),sQuery(id+"F0.wireOp",EDGE,"E116"),sQuery(id+"F0.wireOp",EDGE,"E117")])]});
            var Q1;
            Q1=makeQuery(id+"F3.opExtrude","SWEPT_BODY",BODY,{"disambiguationData":[OSD([sQuery(id+"F0.wireOp",EDGE,"E92.bottom"),sQuery(id+"F0.wireOp",EDGE,"E92.top"),sQuery(id+"F0.wireOp",EDGE,"E92.left"),sQuery(id+"F0.wireOp",EDGE,"E92.right"),sQuery(id+"F0.wireOp",EDGE,"E93.bottom"),sQuery(id+"F0.wireOp",EDGE,"E93.top"),sQuery(id+"F0.wireOp",EDGE,"E93.left"),sQuery(id+"F0.wireOp",EDGE,"E93.right")])]});
            var Q2;
            Q2=makeQuery(id+"F1.opExtrude","SWEPT_BODY",BODY,{"disambiguationData":[OSD([sQuery(id+"F0.wireOp",EDGE,"E92.bottom"),sQuery(id+"F0.wireOp",EDGE,"E92.top"),sQuery(id+"F0.wireOp",EDGE,"E95.MirrorCS"),sQuery(id+"F0.wireOp",EDGE,"E96"),sQuery(id+"F0.wireOp",EDGE,"E97"),sQuery(id+"F0.wireOp",EDGE,"E98"),sQuery(id+"F0.wireOp",EDGE,"E99"),sQuery(id+"F0.wireOp",EDGE,"E100"),sQuery(id+"F0.wireOp",EDGE,"E101.MirrorCS"),sQuery(id+"F0.wireOp",EDGE,"E102.MirrorCS"),sQuery(id+"F0.wireOp",EDGE,"E103"),sQuery(id+"F0.wireOp",EDGE,"04NsANdn-taOn-ddKp-MDbT-y7dXd8gmv4Cl"),sQuery(id+"F0.wireOp",EDGE,"E104"),sQuery(id+"F0.wireOp",EDGE,"3R8MwXPY-31j6-GvAs-L5bG-rwEBLL8UpWRA"),sQuery(id+"F0.wireOp",EDGE,"E105"),sQuery(id+"F0.wireOp",EDGE,"E106"),sQuery(id+"F0.wireOp",EDGE,"E107"),sQuery(id+"F0.wireOp",EDGE,"E108"),sQuery(id+"F0.wireOp",EDGE,"E109"),sQuery(id+"F0.wireOp",EDGE,"E110"),sQuery(id+"F0.wireOp",EDGE,"E111"),sQuery(id+"F0.wireOp",EDGE,"E112"),sQuery(id+"F0.wireOp",EDGE,"E113.right"),sQuery(id+"F0.wireOp",EDGE,"E113.left"),sQuery(id+"F0.wireOp",EDGE,"E114"),sQuery(id+"F0.wireOp",EDGE,"E115"),sQuery(id+"F0.wireOp",EDGE,"E116"),sQuery(id+"F0.wireOp",EDGE,"E117")])]});
            var Q3;
            {var subQ0=sQuery(id+"F0.wireOp",EDGE,"E93.left");Q3=makeQuery(id+"F5.boolean.opBoolean","MERGE",FACE,{"derivedFrom":[makeQuery(id+"F2.opExtrude","SWEPT_FACE",FACE,{"disambiguationData":[OSD([subQ0])]}),makeQuery(id+"F5.opExtrude","SWEPT_FACE",FACE,{"disambiguationData":[OSD([subQ0])]})]});}
            mirror(context, id + "F8", {"entities" : qUnion([Q0, Q1, Q2]), "mirrorPlane" : qUnion([Q3])});
        }
        {
            var Q0;
            Q0=makeQuery(id+"F3.opExtrude","SWEPT_BODY",BODY,{"disambiguationData":[OSD([sQuery(id+"F0.wireOp",EDGE,"E118.bottom"),sQuery(id+"F0.wireOp",EDGE,"E118.top"),sQuery(id+"F0.wireOp",EDGE,"E121"),sQuery(id+"F0.wireOp",EDGE,"E122"),sQuery(id+"F0.wireOp",EDGE,"E123"),sQuery(id+"F0.wireOp",EDGE,"E124"),sQuery(id+"F0.wireOp",EDGE,"E125"),sQuery(id+"F0.wireOp",EDGE,"E126"),sQuery(id+"F0.wireOp",EDGE,"E127"),sQuery(id+"F0.wireOp",EDGE,"E128")])]});
            var Q1;
            Q1=makeQuery(id+"F1.opExtrude","SWEPT_BODY",BODY,{"disambiguationData":[OSD([sQuery(id+"F0.wireOp",EDGE,"E118.bottom"),sQuery(id+"F0.wireOp",EDGE,"E118.top"),sQuery(id+"F0.wireOp",EDGE,"E121"),sQuery(id+"F0.wireOp",EDGE,"E122"),sQuery(id+"F0.wireOp",EDGE,"E123"),sQuery(id+"F0.wireOp",EDGE,"E124"),sQuery(id+"F0.wireOp",EDGE,"E125"),sQuery(id+"F0.wireOp",EDGE,"E126"),sQuery(id+"F0.wireOp",EDGE,"E127"),sQuery(id+"F0.wireOp",EDGE,"E128")])]});
            var Q2;
            {var subQ0=sQuery(id+"F0.wireOp",EDGE,"E119.right");Q2=makeQuery(id+"F5.boolean.opBoolean","MERGE",FACE,{"derivedFrom":[makeQuery(id+"F2.opExtrude","SWEPT_FACE",FACE,{"disambiguationData":[OSD([subQ0])]}),makeQuery(id+"F5.opExtrude","SWEPT_FACE",FACE,{"disambiguationData":[OSD([subQ0])]})]});}
            mirror(context, id + "F9", {"operationType" : NewBodyOperationType.ADD, "entities" : qUnion([Q0, Q1]), "mirrorPlane" : qUnion([Q2])});
        }
        {
            var Q0;
            Q0=makeQuery(id+"F5.boolean.opBoolean","SPLIT",FACE,{"disambiguationData":[TD([makeQuery(id+"F3.opExtrude","SWEPT_FACE",FACE,{"disambiguationData":[OSD([sQuery(id+"F0.wireOp",EDGE,"E84")])]})])],"derivedFrom":makeQuery(id+"F5.opExtrude","CAP_FACE",FACE,{"disambiguationData":[OSD([sQuery(id+"F0.wireOp",EDGE,"E77.bottom"),sQuery(id+"F0.wireOp",EDGE,"E77.top"),sQuery(id+"F0.wireOp",EDGE,"E77.left"),sQuery(id+"F0.wireOp",EDGE,"E77.right")])],"isStart":true})});
            var Q1;
            Q1=makeQuery(id+"F5.boolean.opBoolean","SPLIT",FACE,{"disambiguationData":[TD([makeQuery(id+"F3.opExtrude","SWEPT_FACE",FACE,{"disambiguationData":[OSD([sQuery(id+"F0.wireOp",EDGE,"E129.MirrorC")])]})])],"derivedFrom":makeQuery(id+"F5.opExtrude","CAP_FACE",FACE,{"disambiguationData":[OSD([sQuery(id+"F0.wireOp",EDGE,"E77.bottom"),sQuery(id+"F0.wireOp",EDGE,"E77.top"),sQuery(id+"F0.wireOp",EDGE,"E77.left"),sQuery(id+"F0.wireOp",EDGE,"E77.right")])],"isStart":true})});
            var Q2;
            Q2=makeQuery(id+"F7.opPattern","COPY",FACE,{"derivedFrom":makeQuery(id+"F5.boolean.opBoolean","SPLIT",FACE,{"disambiguationData":[TD([makeQuery(id+"F3.opExtrude","SWEPT_FACE",FACE,{"disambiguationData":[OSD([sQuery(id+"F0.wireOp",EDGE,"E130.MirrorC")])]})])],"derivedFrom":makeQuery(id+"F5.opExtrude","CAP_FACE",FACE,{"disambiguationData":[OSD([sQuery(id+"F0.wireOp",EDGE,"E77.bottom"),sQuery(id+"F0.wireOp",EDGE,"E77.top"),sQuery(id+"F0.wireOp",EDGE,"E77.left"),sQuery(id+"F0.wireOp",EDGE,"E77.right")])],"isStart":true})}),"instanceName":"1"});
            var Q3;
            Q3=makeQuery(id+"F7.opPattern","COPY",FACE,{"derivedFrom":makeQuery(id+"F5.boolean.opBoolean","SPLIT",FACE,{"disambiguationData":[TD([makeQuery(id+"F3.opExtrude","SWEPT_FACE",FACE,{"disambiguationData":[OSD([sQuery(id+"F0.wireOp",EDGE,"E131.MirrorC")])]})])],"derivedFrom":makeQuery(id+"F5.opExtrude","CAP_FACE",FACE,{"disambiguationData":[OSD([sQuery(id+"F0.wireOp",EDGE,"E77.bottom"),sQuery(id+"F0.wireOp",EDGE,"E77.top"),sQuery(id+"F0.wireOp",EDGE,"E77.left"),sQuery(id+"F0.wireOp",EDGE,"E77.right")])],"isStart":true})}),"instanceName":"1"});
            var Q4;
            {var subQ0=sQuery(id+"F0.wireOp",EDGE,"E0.right");var subQ1=sQuery(id+"F0.wireOp",EDGE,"E0.left");var subQ2=sQuery(id+"F0.wireOp",EDGE,"E0.top");var subQ3=sQuery(id+"F0.wireOp",EDGE,"E0.bottom");Q4=makeQuery(id+"F5.boolean.opBoolean","MERGE",FACE,{"disambiguationData":[OD(0.0)],"derivedFrom":[makeQuery(id+"F5.opExtrude","CAP_FACE",FACE,{"disambiguationData":[OSD([subQ3,subQ2,subQ1,subQ0])],"isStart":true}),makeQuery(id+"F5.opExtrude","CAP_FACE",FACE,{"disambiguationData":[OSD([subQ3,subQ2,subQ1,subQ0,sQuery(id+"F0.wireOp",EDGE,"E1.bottom"),sQuery(id+"F0.wireOp",EDGE,"E1.top"),sQuery(id+"F0.wireOp",EDGE,"E1.left"),sQuery(id+"F0.wireOp",EDGE,"E1.right")])],"isStart":true})]});}
            var Q5;
            {var subQ0=sQuery(id+"F0.wireOp",EDGE,"E0.right");var subQ1=sQuery(id+"F0.wireOp",EDGE,"E0.left");var subQ2=sQuery(id+"F0.wireOp",EDGE,"E0.top");var subQ3=sQuery(id+"F0.wireOp",EDGE,"E0.bottom");Q5=makeQuery(id+"F5.boolean.opBoolean","MERGE",FACE,{"disambiguationData":[OD(3.0)],"derivedFrom":[makeQuery(id+"F5.opExtrude","CAP_FACE",FACE,{"disambiguationData":[OSD([subQ3,subQ2,subQ1,subQ0])],"isStart":true}),makeQuery(id+"F5.opExtrude","CAP_FACE",FACE,{"disambiguationData":[OSD([subQ3,subQ2,subQ1,subQ0,sQuery(id+"F0.wireOp",EDGE,"E1.bottom"),sQuery(id+"F0.wireOp",EDGE,"E1.top"),sQuery(id+"F0.wireOp",EDGE,"E1.left"),sQuery(id+"F0.wireOp",EDGE,"E1.right")])],"isStart":true})]});}
            var Q6;
            {var subQ0=sQuery(id+"F0.wireOp",EDGE,"E0.right");var subQ1=sQuery(id+"F0.wireOp",EDGE,"E0.left");var subQ2=sQuery(id+"F0.wireOp",EDGE,"E0.top");var subQ3=sQuery(id+"F0.wireOp",EDGE,"E0.bottom");Q6=makeQuery(id+"F6.opPattern","COPY",FACE,{"derivedFrom":makeQuery(id+"F5.boolean.opBoolean","MERGE",FACE,{"disambiguationData":[OD(1.0)],"derivedFrom":[makeQuery(id+"F5.opExtrude","CAP_FACE",FACE,{"disambiguationData":[OSD([subQ3,subQ2,subQ1,subQ0])],"isStart":true}),makeQuery(id+"F5.opExtrude","CAP_FACE",FACE,{"disambiguationData":[OSD([subQ3,subQ2,subQ1,subQ0,sQuery(id+"F0.wireOp",EDGE,"E1.bottom"),sQuery(id+"F0.wireOp",EDGE,"E1.top"),sQuery(id+"F0.wireOp",EDGE,"E1.left"),sQuery(id+"F0.wireOp",EDGE,"E1.right")])],"isStart":true})]}),"instanceName":"1"});}
            var Q7;
            {var subQ0=sQuery(id+"F0.wireOp",EDGE,"E0.right");var subQ1=sQuery(id+"F0.wireOp",EDGE,"E0.left");var subQ2=sQuery(id+"F0.wireOp",EDGE,"E0.top");var subQ3=sQuery(id+"F0.wireOp",EDGE,"E0.bottom");Q7=makeQuery(id+"F6.opPattern","COPY",FACE,{"derivedFrom":makeQuery(id+"F5.boolean.opBoolean","MERGE",FACE,{"disambiguationData":[OD(2.0)],"derivedFrom":[makeQuery(id+"F5.opExtrude","CAP_FACE",FACE,{"disambiguationData":[OSD([subQ3,subQ2,subQ1,subQ0])],"isStart":true}),makeQuery(id+"F5.opExtrude","CAP_FACE",FACE,{"disambiguationData":[OSD([subQ3,subQ2,subQ1,subQ0,sQuery(id+"F0.wireOp",EDGE,"E1.bottom"),sQuery(id+"F0.wireOp",EDGE,"E1.top"),sQuery(id+"F0.wireOp",EDGE,"E1.left"),sQuery(id+"F0.wireOp",EDGE,"E1.right")])],"isStart":true})]}),"instanceName":"1"});}
            var Q8;
            Q8=makeQuery(id+"F5.boolean.opBoolean","SPLIT",FACE,{"disambiguationData":[TD([makeQuery(id+"F3.opExtrude","SWEPT_FACE",FACE,{"disambiguationData":[OSD([sQuery(id+"F0.wireOp",EDGE,"E140.MirrorC")])]})])],"derivedFrom":makeQuery(id+"F5.opExtrude","CAP_FACE",FACE,{"disambiguationData":[OSD([sQuery(id+"F0.wireOp",EDGE,"E119.bottom"),sQuery(id+"F0.wireOp",EDGE,"E119.top"),sQuery(id+"F0.wireOp",EDGE,"E119.left"),sQuery(id+"F0.wireOp",EDGE,"E119.right")])],"isStart":true})});
            var Q9;
            Q9=makeQuery(id+"F5.boolean.opBoolean","SPLIT",FACE,{"disambiguationData":[TD([makeQuery(id+"F3.opExtrude","SWEPT_FACE",FACE,{"disambiguationData":[OSD([sQuery(id+"F0.wireOp",EDGE,"E141.MirrorC")])]})])],"derivedFrom":makeQuery(id+"F5.opExtrude","CAP_FACE",FACE,{"disambiguationData":[OSD([sQuery(id+"F0.wireOp",EDGE,"E119.bottom"),sQuery(id+"F0.wireOp",EDGE,"E119.top"),sQuery(id+"F0.wireOp",EDGE,"E119.left"),sQuery(id+"F0.wireOp",EDGE,"E119.right")])],"isStart":true})});
            var Q10;
            Q10=makeQuery(id+"F9.opPattern","COPY",FACE,{"derivedFrom":makeQuery(id+"F5.boolean.opBoolean","SPLIT",FACE,{"disambiguationData":[TD([makeQuery(id+"F3.opExtrude","SWEPT_FACE",FACE,{"disambiguationData":[OSD([sQuery(id+"F0.wireOp",EDGE,"E142.MirrorC")])]})])],"derivedFrom":makeQuery(id+"F5.opExtrude","CAP_FACE",FACE,{"disambiguationData":[OSD([sQuery(id+"F0.wireOp",EDGE,"E119.bottom"),sQuery(id+"F0.wireOp",EDGE,"E119.top"),sQuery(id+"F0.wireOp",EDGE,"E119.left"),sQuery(id+"F0.wireOp",EDGE,"E119.right")])],"isStart":true})}),"instanceName":"1"});
            var Q11;
            Q11=makeQuery(id+"F9.opPattern","COPY",FACE,{"derivedFrom":makeQuery(id+"F5.boolean.opBoolean","SPLIT",FACE,{"disambiguationData":[TD([makeQuery(id+"F3.opExtrude","SWEPT_FACE",FACE,{"disambiguationData":[OSD([sQuery(id+"F0.wireOp",EDGE,"E143.MirrorC")])]})])],"derivedFrom":makeQuery(id+"F5.opExtrude","CAP_FACE",FACE,{"disambiguationData":[OSD([sQuery(id+"F0.wireOp",EDGE,"E119.bottom"),sQuery(id+"F0.wireOp",EDGE,"E119.top"),sQuery(id+"F0.wireOp",EDGE,"E119.left"),sQuery(id+"F0.wireOp",EDGE,"E119.right")])],"isStart":true})}),"instanceName":"1"});
            var Q12;
            Q12=makeQuery(id+"F5.boolean.opBoolean","SPLIT",FACE,{"disambiguationData":[TD([makeQuery(id+"F3.opExtrude","SWEPT_FACE",FACE,{"disambiguationData":[OSD([sQuery(id+"F0.wireOp",EDGE,"E137.MirrorC")])]})])],"derivedFrom":makeQuery(id+"F5.opExtrude","CAP_FACE",FACE,{"disambiguationData":[OSD([sQuery(id+"F0.wireOp",EDGE,"E93.bottom"),sQuery(id+"F0.wireOp",EDGE,"E93.top"),sQuery(id+"F0.wireOp",EDGE,"E93.left"),sQuery(id+"F0.wireOp",EDGE,"E93.right")])],"isStart":true})});
            var Q13;
            Q13=makeQuery(id+"F5.boolean.opBoolean","SPLIT",FACE,{"disambiguationData":[TD([makeQuery(id+"F3.opExtrude","SWEPT_FACE",FACE,{"disambiguationData":[OSD([sQuery(id+"F0.wireOp",EDGE,"E136.MirrorC")])]})])],"derivedFrom":makeQuery(id+"F5.opExtrude","CAP_FACE",FACE,{"disambiguationData":[OSD([sQuery(id+"F0.wireOp",EDGE,"E93.bottom"),sQuery(id+"F0.wireOp",EDGE,"E93.top"),sQuery(id+"F0.wireOp",EDGE,"E93.left"),sQuery(id+"F0.wireOp",EDGE,"E93.right")])],"isStart":true})});
            var Q14;
            Q14=makeQuery(id+"F8.opPattern","COPY",FACE,{"derivedFrom":makeQuery(id+"F5.boolean.opBoolean","SPLIT",FACE,{"disambiguationData":[TD([makeQuery(id+"F3.opExtrude","SWEPT_FACE",FACE,{"disambiguationData":[OSD([sQuery(id+"F0.wireOp",EDGE,"E138.MirrorC")])]})])],"derivedFrom":makeQuery(id+"F5.opExtrude","CAP_FACE",FACE,{"disambiguationData":[OSD([sQuery(id+"F0.wireOp",EDGE,"E93.bottom"),sQuery(id+"F0.wireOp",EDGE,"E93.top"),sQuery(id+"F0.wireOp",EDGE,"E93.left"),sQuery(id+"F0.wireOp",EDGE,"E93.right")])],"isStart":true})}),"instanceName":"1"});
            var Q15;
            Q15=makeQuery(id+"F8.opPattern","COPY",FACE,{"derivedFrom":makeQuery(id+"F5.boolean.opBoolean","SPLIT",FACE,{"disambiguationData":[TD([makeQuery(id+"F3.opExtrude","SWEPT_FACE",FACE,{"disambiguationData":[OSD([sQuery(id+"F0.wireOp",EDGE,"E139.MirrorC")])]})])],"derivedFrom":makeQuery(id+"F5.opExtrude","CAP_FACE",FACE,{"disambiguationData":[OSD([sQuery(id+"F0.wireOp",EDGE,"E93.bottom"),sQuery(id+"F0.wireOp",EDGE,"E93.top"),sQuery(id+"F0.wireOp",EDGE,"E93.left"),sQuery(id+"F0.wireOp",EDGE,"E93.right")])],"isStart":true})}),"instanceName":"1"});
            extrude(context, id + "F10", {"entities" : qUnion([Q0, Q1, Q2, Q3, Q4, Q5, Q6, Q7, Q8, Q9, Q10, Q11, Q12, Q13, Q14, Q15]), "depth" : 5 * mm, "offsetDistance" : 25 * mm});
        }
        {
            var Q0;
            Q0=makeQuery(id+"F1.opExtrude","SWEPT_BODY",BODY,{"disambiguationData":[OSD([sQuery(id+"F0.wireOp",EDGE,"E76.bottom"),sQuery(id+"F0.wireOp",EDGE,"E76.top"),sQuery(id+"F0.wireOp",EDGE,"E79.MirrorCS"),sQuery(id+"F0.wireOp",EDGE,"E80"),sQuery(id+"F0.wireOp",EDGE,"E81"),sQuery(id+"F0.wireOp",EDGE,"E82"),sQuery(id+"F0.wireOp",EDGE,"E83"),sQuery(id+"F0.wireOp",EDGE,"E85"),sQuery(id+"F0.wireOp",EDGE,"E86.MirrorCS"),sQuery(id+"F0.wireOp",EDGE,"E87.MirrorCS"),sQuery(id+"F0.wireOp",EDGE,"E88.MirrorCS"),sQuery(id+"F0.wireOp",EDGE,"E89.MirrorCS"),sQuery(id+"F0.wireOp",EDGE,"E90.MirrorCS"),sQuery(id+"F0.wireOp",EDGE,"E91.MirrorCS")])]});
            var Q1;
            Q1=makeQuery(id+"F3.opExtrude","SWEPT_BODY",BODY,{"disambiguationData":[OSD([sQuery(id+"F0.wireOp",EDGE,"E0.bottom"),sQuery(id+"F0.wireOp",EDGE,"E0.top"),sQuery(id+"F0.wireOp",EDGE,"E3"),sQuery(id+"F0.wireOp",EDGE,"E4"),sQuery(id+"F0.wireOp",EDGE,"E5"),sQuery(id+"F0.wireOp",EDGE,"E6"),sQuery(id+"F0.wireOp",EDGE,"E7"),sQuery(id+"F0.wireOp",EDGE,"E8"),sQuery(id+"F0.wireOp",EDGE,"E9"),sQuery(id+"F0.wireOp",EDGE,"E11"),sQuery(id+"F0.wireOp",EDGE,"E12"),sQuery(id+"F0.wireOp",EDGE,"E13"),sQuery(id+"F0.wireOp",EDGE,"E14"),sQuery(id+"F0.wireOp",EDGE,"E15"),sQuery(id+"F0.wireOp",EDGE,"E16"),sQuery(id+"F0.wireOp",EDGE,"E17"),sQuery(id+"F0.wireOp",EDGE,"E18"),sQuery(id+"F0.wireOp",EDGE,"E19"),sQuery(id+"F0.wireOp",EDGE,"E20"),sQuery(id+"F0.wireOp",EDGE,"E21"),sQuery(id+"F0.wireOp",EDGE,"E22"),sQuery(id+"F0.wireOp",EDGE,"E23"),sQuery(id+"F0.wireOp",EDGE,"E24"),sQuery(id+"F0.wireOp",EDGE,"E25"),sQuery(id+"F0.wireOp",EDGE,"E26"),sQuery(id+"F0.wireOp",EDGE,"E27"),sQuery(id+"F0.wireOp",EDGE,"E28"),sQuery(id+"F0.wireOp",EDGE,"E29"),sQuery(id+"F0.wireOp",EDGE,"E30"),sQuery(id+"F0.wireOp",EDGE,"E31"),sQuery(id+"F0.wireOp",EDGE,"E32"),sQuery(id+"F0.wireOp",EDGE,"E33"),sQuery(id+"F0.wireOp",EDGE,"E34"),sQuery(id+"F0.wireOp",EDGE,"E35"),sQuery(id+"F0.wireOp",EDGE,"E36"),sQuery(id+"F0.wireOp",EDGE,"E37"),sQuery(id+"F0.wireOp",EDGE,"E38"),sQuery(id+"F0.wireOp",EDGE,"E39"),sQuery(id+"F0.wireOp",EDGE,"E40"),sQuery(id+"F0.wireOp",EDGE,"E41"),sQuery(id+"F0.wireOp",EDGE,"E42"),sQuery(id+"F0.wireOp",EDGE,"E43"),sQuery(id+"F0.wireOp",EDGE,"E44"),sQuery(id+"F0.wireOp",EDGE,"E45"),sQuery(id+"F0.wireOp",EDGE,"E46"),sQuery(id+"F0.wireOp",EDGE,"E47"),sQuery(id+"F0.wireOp",EDGE,"E48"),sQuery(id+"F0.wireOp",EDGE,"E49"),sQuery(id+"F0.wireOp",EDGE,"E50"),sQuery(id+"F0.wireOp",EDGE,"E51"),sQuery(id+"F0.wireOp",EDGE,"E52"),sQuery(id+"F0.wireOp",EDGE,"E53"),sQuery(id+"F0.wireOp",EDGE,"E54"),sQuery(id+"F0.wireOp",EDGE,"E55"),sQuery(id+"F0.wireOp",EDGE,"E56"),sQuery(id+"F0.wireOp",EDGE,"E57"),sQuery(id+"F0.wireOp",EDGE,"E58"),sQuery(id+"F0.wireOp",EDGE,"E59"),sQuery(id+"F0.wireOp",EDGE,"E60"),sQuery(id+"F0.wireOp",EDGE,"E61"),sQuery(id+"F0.wireOp",EDGE,"E62"),sQuery(id+"F0.wireOp",EDGE,"E63"),sQuery(id+"F0.wireOp",EDGE,"E64"),sQuery(id+"F0.wireOp",EDGE,"E65"),sQuery(id+"F0.wireOp",EDGE,"E66"),sQuery(id+"F0.wireOp",EDGE,"E67"),sQuery(id+"F0.wireOp",EDGE,"E68"),sQuery(id+"F0.wireOp",EDGE,"E69"),sQuery(id+"F0.wireOp",EDGE,"E70.MirrorCS"),sQuery(id+"F0.wireOp",EDGE,"E71.MirrorCS"),sQuery(id+"F0.wireOp",EDGE,"E72"),sQuery(id+"F0.wireOp",EDGE,"E73"),sQuery(id+"F0.wireOp",EDGE,"E74"),sQuery(id+"F0.wireOp",EDGE,"E75")])]});
            var Q2;
            Q2=makeQuery(id+"F3.opExtrude","SWEPT_BODY",BODY,{"disambiguationData":[OSD([sQuery(id+"F0.wireOp",EDGE,"E92.bottom"),sQuery(id+"F0.wireOp",EDGE,"E92.top"),sQuery(id+"F0.wireOp",EDGE,"E95.MirrorCS"),sQuery(id+"F0.wireOp",EDGE,"E96"),sQuery(id+"F0.wireOp",EDGE,"E97"),sQuery(id+"F0.wireOp",EDGE,"E98"),sQuery(id+"F0.wireOp",EDGE,"E99"),sQuery(id+"F0.wireOp",EDGE,"E100"),sQuery(id+"F0.wireOp",EDGE,"E101.MirrorCS"),sQuery(id+"F0.wireOp",EDGE,"E102.MirrorCS"),sQuery(id+"F0.wireOp",EDGE,"E103"),sQuery(id+"F0.wireOp",EDGE,"E104"),sQuery(id+"F0.wireOp",EDGE,"E105"),sQuery(id+"F0.wireOp",EDGE,"E106"),sQuery(id+"F0.wireOp",EDGE,"E107"),sQuery(id+"F0.wireOp",EDGE,"E108"),sQuery(id+"F0.wireOp",EDGE,"E109"),sQuery(id+"F0.wireOp",EDGE,"E110"),sQuery(id+"F0.wireOp",EDGE,"E111"),sQuery(id+"F0.wireOp",EDGE,"E112"),sQuery(id+"F0.wireOp",EDGE,"E113.right"),sQuery(id+"F0.wireOp",EDGE,"E113.left"),sQuery(id+"F0.wireOp",EDGE,"E114"),sQuery(id+"F0.wireOp",EDGE,"E115"),sQuery(id+"F0.wireOp",EDGE,"E116"),sQuery(id+"F0.wireOp",EDGE,"E117"),sQuery(id+"F0.wireOp",EDGE,"E144"),sQuery(id+"F0.wireOp",EDGE,"E145")])]});
            var Q3;
            Q3=makeQuery(id+"F3.opExtrude","SWEPT_BODY",BODY,{"disambiguationData":[OSD([sQuery(id+"F0.wireOp",EDGE,"E118.bottom"),sQuery(id+"F0.wireOp",EDGE,"E118.top"),sQuery(id+"F0.wireOp",EDGE,"E121"),sQuery(id+"F0.wireOp",EDGE,"E122"),sQuery(id+"F0.wireOp",EDGE,"E123"),sQuery(id+"F0.wireOp",EDGE,"E124"),sQuery(id+"F0.wireOp",EDGE,"E125"),sQuery(id+"F0.wireOp",EDGE,"E126"),sQuery(id+"F0.wireOp",EDGE,"E127"),sQuery(id+"F0.wireOp",EDGE,"E128")])]});
            var Q4;
            Q4=qCreatedBy(makeId("Top.planeOp"),FACE);
            transform(context, id + "F11", {"entities" : qUnion([Q0, Q1, Q2, Q3]), "transformType" : TransformType.TRANSLATION_DISTANCE, "transformDirection" : qUnion([Q4]), "distance" : 5 * mm, "makeCopy" : false});
        }
        {
            var Q0;
            Q0=makeQuery(id+"F1.opExtrude","SWEPT_BODY",BODY,{"disambiguationData":[OSD([sQuery(id+"F0.wireOp",EDGE,"E76.bottom"),sQuery(id+"F0.wireOp",EDGE,"E76.top"),sQuery(id+"F0.wireOp",EDGE,"E79.MirrorCS"),sQuery(id+"F0.wireOp",EDGE,"E80"),sQuery(id+"F0.wireOp",EDGE,"E81"),sQuery(id+"F0.wireOp",EDGE,"E82"),sQuery(id+"F0.wireOp",EDGE,"E83"),sQuery(id+"F0.wireOp",EDGE,"E85"),sQuery(id+"F0.wireOp",EDGE,"E86.MirrorCS"),sQuery(id+"F0.wireOp",EDGE,"E87.MirrorCS"),sQuery(id+"F0.wireOp",EDGE,"E88.MirrorCS"),sQuery(id+"F0.wireOp",EDGE,"E89.MirrorCS"),sQuery(id+"F0.wireOp",EDGE,"E90.MirrorCS"),sQuery(id+"F0.wireOp",EDGE,"E91.MirrorCS")])]});
            var Q1;
            Q1=makeQuery(id+"F3.opExtrude","SWEPT_BODY",BODY,{"disambiguationData":[OSD([sQuery(id+"F0.wireOp",EDGE,"E0.bottom"),sQuery(id+"F0.wireOp",EDGE,"E0.top"),sQuery(id+"F0.wireOp",EDGE,"E3"),sQuery(id+"F0.wireOp",EDGE,"E4"),sQuery(id+"F0.wireOp",EDGE,"E5"),sQuery(id+"F0.wireOp",EDGE,"E6"),sQuery(id+"F0.wireOp",EDGE,"E7"),sQuery(id+"F0.wireOp",EDGE,"E8"),sQuery(id+"F0.wireOp",EDGE,"E9"),sQuery(id+"F0.wireOp",EDGE,"E11"),sQuery(id+"F0.wireOp",EDGE,"E12"),sQuery(id+"F0.wireOp",EDGE,"E13"),sQuery(id+"F0.wireOp",EDGE,"E14"),sQuery(id+"F0.wireOp",EDGE,"E15"),sQuery(id+"F0.wireOp",EDGE,"E16"),sQuery(id+"F0.wireOp",EDGE,"E17"),sQuery(id+"F0.wireOp",EDGE,"E18"),sQuery(id+"F0.wireOp",EDGE,"E19"),sQuery(id+"F0.wireOp",EDGE,"E20"),sQuery(id+"F0.wireOp",EDGE,"E21"),sQuery(id+"F0.wireOp",EDGE,"E22"),sQuery(id+"F0.wireOp",EDGE,"E23"),sQuery(id+"F0.wireOp",EDGE,"E24"),sQuery(id+"F0.wireOp",EDGE,"E25"),sQuery(id+"F0.wireOp",EDGE,"E26"),sQuery(id+"F0.wireOp",EDGE,"E27"),sQuery(id+"F0.wireOp",EDGE,"E28"),sQuery(id+"F0.wireOp",EDGE,"E29"),sQuery(id+"F0.wireOp",EDGE,"E30"),sQuery(id+"F0.wireOp",EDGE,"E31"),sQuery(id+"F0.wireOp",EDGE,"E32"),sQuery(id+"F0.wireOp",EDGE,"E33"),sQuery(id+"F0.wireOp",EDGE,"E34"),sQuery(id+"F0.wireOp",EDGE,"E35"),sQuery(id+"F0.wireOp",EDGE,"E36"),sQuery(id+"F0.wireOp",EDGE,"E37"),sQuery(id+"F0.wireOp",EDGE,"E38"),sQuery(id+"F0.wireOp",EDGE,"E39"),sQuery(id+"F0.wireOp",EDGE,"E40"),sQuery(id+"F0.wireOp",EDGE,"E41"),sQuery(id+"F0.wireOp",EDGE,"E42"),sQuery(id+"F0.wireOp",EDGE,"E43"),sQuery(id+"F0.wireOp",EDGE,"E44"),sQuery(id+"F0.wireOp",EDGE,"E45"),sQuery(id+"F0.wireOp",EDGE,"E46"),sQuery(id+"F0.wireOp",EDGE,"E47"),sQuery(id+"F0.wireOp",EDGE,"E48"),sQuery(id+"F0.wireOp",EDGE,"E49"),sQuery(id+"F0.wireOp",EDGE,"E50"),sQuery(id+"F0.wireOp",EDGE,"E51"),sQuery(id+"F0.wireOp",EDGE,"E52"),sQuery(id+"F0.wireOp",EDGE,"E53"),sQuery(id+"F0.wireOp",EDGE,"E54"),sQuery(id+"F0.wireOp",EDGE,"E55"),sQuery(id+"F0.wireOp",EDGE,"E56"),sQuery(id+"F0.wireOp",EDGE,"E57"),sQuery(id+"F0.wireOp",EDGE,"E58"),sQuery(id+"F0.wireOp",EDGE,"E59"),sQuery(id+"F0.wireOp",EDGE,"E60"),sQuery(id+"F0.wireOp",EDGE,"E61"),sQuery(id+"F0.wireOp",EDGE,"E62"),sQuery(id+"F0.wireOp",EDGE,"E63"),sQuery(id+"F0.wireOp",EDGE,"E64"),sQuery(id+"F0.wireOp",EDGE,"E65"),sQuery(id+"F0.wireOp",EDGE,"E66"),sQuery(id+"F0.wireOp",EDGE,"E67"),sQuery(id+"F0.wireOp",EDGE,"E68"),sQuery(id+"F0.wireOp",EDGE,"E69"),sQuery(id+"F0.wireOp",EDGE,"E70.MirrorCS"),sQuery(id+"F0.wireOp",EDGE,"E71.MirrorCS"),sQuery(id+"F0.wireOp",EDGE,"E72"),sQuery(id+"F0.wireOp",EDGE,"E73"),sQuery(id+"F0.wireOp",EDGE,"E74"),sQuery(id+"F0.wireOp",EDGE,"E75")])]});
            var Q2;
            Q2=makeQuery(id+"F3.opExtrude","SWEPT_BODY",BODY,{"disambiguationData":[OSD([sQuery(id+"F0.wireOp",EDGE,"E118.bottom"),sQuery(id+"F0.wireOp",EDGE,"E118.top"),sQuery(id+"F0.wireOp",EDGE,"E121"),sQuery(id+"F0.wireOp",EDGE,"E122"),sQuery(id+"F0.wireOp",EDGE,"E123"),sQuery(id+"F0.wireOp",EDGE,"E124"),sQuery(id+"F0.wireOp",EDGE,"E125"),sQuery(id+"F0.wireOp",EDGE,"E126"),sQuery(id+"F0.wireOp",EDGE,"E127"),sQuery(id+"F0.wireOp",EDGE,"E128")])]});
            var Q3;
            Q3=makeQuery(id+"F8.opPattern","COPY",BODY,{"derivedFrom":makeQuery(id+"F1.opExtrude","SWEPT_BODY",BODY,{"disambiguationData":[OSD([sQuery(id+"F0.wireOp",EDGE,"E92.bottom"),sQuery(id+"F0.wireOp",EDGE,"E92.top"),sQuery(id+"F0.wireOp",EDGE,"E95.MirrorCS"),sQuery(id+"F0.wireOp",EDGE,"E96"),sQuery(id+"F0.wireOp",EDGE,"E97"),sQuery(id+"F0.wireOp",EDGE,"E98"),sQuery(id+"F0.wireOp",EDGE,"E99"),sQuery(id+"F0.wireOp",EDGE,"E100"),sQuery(id+"F0.wireOp",EDGE,"E101.MirrorCS"),sQuery(id+"F0.wireOp",EDGE,"E102.MirrorCS"),sQuery(id+"F0.wireOp",EDGE,"E103"),sQuery(id+"F0.wireOp",EDGE,"04NsANdn-taOn-ddKp-MDbT-y7dXd8gmv4Cl"),sQuery(id+"F0.wireOp",EDGE,"E104"),sQuery(id+"F0.wireOp",EDGE,"3R8MwXPY-31j6-GvAs-L5bG-rwEBLL8UpWRA"),sQuery(id+"F0.wireOp",EDGE,"E105"),sQuery(id+"F0.wireOp",EDGE,"E106"),sQuery(id+"F0.wireOp",EDGE,"E107"),sQuery(id+"F0.wireOp",EDGE,"E108"),sQuery(id+"F0.wireOp",EDGE,"E109"),sQuery(id+"F0.wireOp",EDGE,"E110"),sQuery(id+"F0.wireOp",EDGE,"E111"),sQuery(id+"F0.wireOp",EDGE,"E112"),sQuery(id+"F0.wireOp",EDGE,"E113.right"),sQuery(id+"F0.wireOp",EDGE,"E113.left"),sQuery(id+"F0.wireOp",EDGE,"E114"),sQuery(id+"F0.wireOp",EDGE,"E115"),sQuery(id+"F0.wireOp",EDGE,"E116"),sQuery(id+"F0.wireOp",EDGE,"E117")])]}),"instanceName":"1"});
            var Q4;
            Q4=makeQuery(id+"F3.opExtrude","SWEPT_BODY",BODY,{"disambiguationData":[OSD([sQuery(id+"F0.wireOp",EDGE,"E92.bottom"),sQuery(id+"F0.wireOp",EDGE,"E92.top"),sQuery(id+"F0.wireOp",EDGE,"E95.MirrorCS"),sQuery(id+"F0.wireOp",EDGE,"E96"),sQuery(id+"F0.wireOp",EDGE,"E97"),sQuery(id+"F0.wireOp",EDGE,"E98"),sQuery(id+"F0.wireOp",EDGE,"E99"),sQuery(id+"F0.wireOp",EDGE,"E100"),sQuery(id+"F0.wireOp",EDGE,"E101.MirrorCS"),sQuery(id+"F0.wireOp",EDGE,"E102.MirrorCS"),sQuery(id+"F0.wireOp",EDGE,"E103"),sQuery(id+"F0.wireOp",EDGE,"E104"),sQuery(id+"F0.wireOp",EDGE,"E105"),sQuery(id+"F0.wireOp",EDGE,"E106"),sQuery(id+"F0.wireOp",EDGE,"E107"),sQuery(id+"F0.wireOp",EDGE,"E108"),sQuery(id+"F0.wireOp",EDGE,"E109"),sQuery(id+"F0.wireOp",EDGE,"E110"),sQuery(id+"F0.wireOp",EDGE,"E111"),sQuery(id+"F0.wireOp",EDGE,"E112"),sQuery(id+"F0.wireOp",EDGE,"E113.right"),sQuery(id+"F0.wireOp",EDGE,"E113.left"),sQuery(id+"F0.wireOp",EDGE,"E114"),sQuery(id+"F0.wireOp",EDGE,"E115"),sQuery(id+"F0.wireOp",EDGE,"E116"),sQuery(id+"F0.wireOp",EDGE,"E117"),sQuery(id+"F0.wireOp",EDGE,"E144"),sQuery(id+"F0.wireOp",EDGE,"E145")])]});
            var Q5;
            Q5=sQuery(id+"F0.wireOp",VERTEX,"E39.start");
            transform(context, id + "F12", {"entities" : qUnion([Q0, Q1, Q2, Q3, Q4]), "transformType" : TransformType.SCALE_UNIFORMLY, "scale" : 0.22, "scalePoint" : qUnion([Q5]), "makeCopy" : false});
        }
        {
            var Q0;
            Q0=makeQuery(id+"F7.opPattern","COPY",EDGE,{"derivedFrom":makeQuery(id+"F3.opExtrude","CAP_EDGE",EDGE,{"disambiguationData":[OSD([sQuery(id+"F0.wireOp",EDGE,"E129.MirrorC")])],"isStart":true}),"instanceName":"1"});
            var Q1;
            Q1=makeQuery(id+"F7.opPattern","COPY",FACE,{"derivedFrom":makeQuery(id+"F5.boolean.opBoolean","SPLIT",FACE,{"disambiguationData":[TD([makeQuery(id+"F3.opExtrude","SWEPT_FACE",FACE,{"disambiguationData":[OSD([sQuery(id+"F0.wireOp",EDGE,"E84")])]})])],"derivedFrom":makeQuery(id+"F5.opExtrude","CAP_FACE",FACE,{"disambiguationData":[OSD([sQuery(id+"F0.wireOp",EDGE,"E77.bottom"),sQuery(id+"F0.wireOp",EDGE,"E77.top"),sQuery(id+"F0.wireOp",EDGE,"E77.left"),sQuery(id+"F0.wireOp",EDGE,"E77.right")])],"isStart":true})}),"instanceName":"1"});
            var Q2;
            Q2=makeQuery(id+"F5.boolean.opBoolean","SPLIT",FACE,{"disambiguationData":[TD([makeQuery(id+"F3.opExtrude","SWEPT_FACE",FACE,{"disambiguationData":[OSD([sQuery(id+"F0.wireOp",EDGE,"E130.MirrorC")])]})])],"derivedFrom":makeQuery(id+"F5.opExtrude","CAP_FACE",FACE,{"disambiguationData":[OSD([sQuery(id+"F0.wireOp",EDGE,"E77.bottom"),sQuery(id+"F0.wireOp",EDGE,"E77.top"),sQuery(id+"F0.wireOp",EDGE,"E77.left"),sQuery(id+"F0.wireOp",EDGE,"E77.right")])],"isStart":true})});
            var Q3;
            Q3=makeQuery(id+"F5.boolean.opBoolean","SPLIT",FACE,{"disambiguationData":[TD([makeQuery(id+"F3.opExtrude","SWEPT_FACE",FACE,{"disambiguationData":[OSD([sQuery(id+"F0.wireOp",EDGE,"E131.MirrorC")])]})])],"derivedFrom":makeQuery(id+"F5.opExtrude","CAP_FACE",FACE,{"disambiguationData":[OSD([sQuery(id+"F0.wireOp",EDGE,"E77.bottom"),sQuery(id+"F0.wireOp",EDGE,"E77.top"),sQuery(id+"F0.wireOp",EDGE,"E77.left"),sQuery(id+"F0.wireOp",EDGE,"E77.right")])],"isStart":true})});
            var Q4;
            {var subQ0=sQuery(id+"F0.wireOp",EDGE,"E0.right");var subQ1=sQuery(id+"F0.wireOp",EDGE,"E0.left");var subQ2=sQuery(id+"F0.wireOp",EDGE,"E0.top");var subQ3=sQuery(id+"F0.wireOp",EDGE,"E0.bottom");Q4=makeQuery(id+"F5.boolean.opBoolean","MERGE",FACE,{"disambiguationData":[OD(1.0)],"derivedFrom":[makeQuery(id+"F5.opExtrude","CAP_FACE",FACE,{"disambiguationData":[OSD([subQ3,subQ2,subQ1,subQ0])],"isStart":true}),makeQuery(id+"F5.opExtrude","CAP_FACE",FACE,{"disambiguationData":[OSD([subQ3,subQ2,subQ1,subQ0,sQuery(id+"F0.wireOp",EDGE,"E1.bottom"),sQuery(id+"F0.wireOp",EDGE,"E1.top"),sQuery(id+"F0.wireOp",EDGE,"E1.left"),sQuery(id+"F0.wireOp",EDGE,"E1.right")])],"isStart":true})]});}
            var Q5;
            {var subQ0=sQuery(id+"F0.wireOp",EDGE,"E0.right");var subQ1=sQuery(id+"F0.wireOp",EDGE,"E0.left");var subQ2=sQuery(id+"F0.wireOp",EDGE,"E0.top");var subQ3=sQuery(id+"F0.wireOp",EDGE,"E0.bottom");Q5=makeQuery(id+"F5.boolean.opBoolean","MERGE",FACE,{"disambiguationData":[OD(2.0)],"derivedFrom":[makeQuery(id+"F5.opExtrude","CAP_FACE",FACE,{"disambiguationData":[OSD([subQ3,subQ2,subQ1,subQ0])],"isStart":true}),makeQuery(id+"F5.opExtrude","CAP_FACE",FACE,{"disambiguationData":[OSD([subQ3,subQ2,subQ1,subQ0,sQuery(id+"F0.wireOp",EDGE,"E1.bottom"),sQuery(id+"F0.wireOp",EDGE,"E1.top"),sQuery(id+"F0.wireOp",EDGE,"E1.left"),sQuery(id+"F0.wireOp",EDGE,"E1.right")])],"isStart":true})]});}
            var Q6;
            {var subQ0=sQuery(id+"F0.wireOp",EDGE,"E0.right");var subQ1=sQuery(id+"F0.wireOp",EDGE,"E0.left");var subQ2=sQuery(id+"F0.wireOp",EDGE,"E0.top");var subQ3=sQuery(id+"F0.wireOp",EDGE,"E0.bottom");Q6=makeQuery(id+"F6.opPattern","COPY",FACE,{"derivedFrom":makeQuery(id+"F5.boolean.opBoolean","MERGE",FACE,{"disambiguationData":[OD(3.0)],"derivedFrom":[makeQuery(id+"F5.opExtrude","CAP_FACE",FACE,{"disambiguationData":[OSD([subQ3,subQ2,subQ1,subQ0])],"isStart":true}),makeQuery(id+"F5.opExtrude","CAP_FACE",FACE,{"disambiguationData":[OSD([subQ3,subQ2,subQ1,subQ0,sQuery(id+"F0.wireOp",EDGE,"E1.bottom"),sQuery(id+"F0.wireOp",EDGE,"E1.top"),sQuery(id+"F0.wireOp",EDGE,"E1.left"),sQuery(id+"F0.wireOp",EDGE,"E1.right")])],"isStart":true})]}),"instanceName":"1"});}
            var Q7;
            {var subQ0=sQuery(id+"F0.wireOp",EDGE,"E0.right");var subQ1=sQuery(id+"F0.wireOp",EDGE,"E0.left");var subQ2=sQuery(id+"F0.wireOp",EDGE,"E0.top");var subQ3=sQuery(id+"F0.wireOp",EDGE,"E0.bottom");Q7=makeQuery(id+"F6.opPattern","COPY",FACE,{"derivedFrom":makeQuery(id+"F5.boolean.opBoolean","MERGE",FACE,{"disambiguationData":[OD(0.0)],"derivedFrom":[makeQuery(id+"F5.opExtrude","CAP_FACE",FACE,{"disambiguationData":[OSD([subQ3,subQ2,subQ1,subQ0])],"isStart":true}),makeQuery(id+"F5.opExtrude","CAP_FACE",FACE,{"disambiguationData":[OSD([subQ3,subQ2,subQ1,subQ0,sQuery(id+"F0.wireOp",EDGE,"E1.bottom"),sQuery(id+"F0.wireOp",EDGE,"E1.top"),sQuery(id+"F0.wireOp",EDGE,"E1.left"),sQuery(id+"F0.wireOp",EDGE,"E1.right")])],"isStart":true})]}),"instanceName":"1"});}
            var Q8;
            Q8=makeQuery(id+"F9.opPattern","COPY",FACE,{"derivedFrom":makeQuery(id+"F5.boolean.opBoolean","SPLIT",FACE,{"disambiguationData":[TD([makeQuery(id+"F3.opExtrude","SWEPT_FACE",FACE,{"disambiguationData":[OSD([sQuery(id+"F0.wireOp",EDGE,"E141.MirrorC")])]})])],"derivedFrom":makeQuery(id+"F5.opExtrude","CAP_FACE",FACE,{"disambiguationData":[OSD([sQuery(id+"F0.wireOp",EDGE,"E119.bottom"),sQuery(id+"F0.wireOp",EDGE,"E119.top"),sQuery(id+"F0.wireOp",EDGE,"E119.left"),sQuery(id+"F0.wireOp",EDGE,"E119.right")])],"isStart":true})}),"instanceName":"1"});
            var Q9;
            Q9=makeQuery(id+"F9.opPattern","COPY",EDGE,{"derivedFrom":makeQuery(id+"F3.opExtrude","CAP_EDGE",EDGE,{"disambiguationData":[OSD([sQuery(id+"F0.wireOp",EDGE,"E140.MirrorC")])],"isStart":true}),"instanceName":"1"});
            var Q10;
            Q10=makeQuery(id+"F5.boolean.opBoolean","SPLIT",FACE,{"disambiguationData":[TD([makeQuery(id+"F3.opExtrude","SWEPT_FACE",FACE,{"disambiguationData":[OSD([sQuery(id+"F0.wireOp",EDGE,"E142.MirrorC")])]})])],"derivedFrom":makeQuery(id+"F5.opExtrude","CAP_FACE",FACE,{"disambiguationData":[OSD([sQuery(id+"F0.wireOp",EDGE,"E119.bottom"),sQuery(id+"F0.wireOp",EDGE,"E119.top"),sQuery(id+"F0.wireOp",EDGE,"E119.left"),sQuery(id+"F0.wireOp",EDGE,"E119.right")])],"isStart":true})});
            var Q11;
            Q11=makeQuery(id+"F5.boolean.opBoolean","SPLIT",FACE,{"disambiguationData":[TD([makeQuery(id+"F3.opExtrude","SWEPT_FACE",FACE,{"disambiguationData":[OSD([sQuery(id+"F0.wireOp",EDGE,"E143.MirrorC")])]})])],"derivedFrom":makeQuery(id+"F5.opExtrude","CAP_FACE",FACE,{"disambiguationData":[OSD([sQuery(id+"F0.wireOp",EDGE,"E119.bottom"),sQuery(id+"F0.wireOp",EDGE,"E119.top"),sQuery(id+"F0.wireOp",EDGE,"E119.left"),sQuery(id+"F0.wireOp",EDGE,"E119.right")])],"isStart":true})});
            var Q12;
            Q12=makeQuery(id+"F3.opExtrude","CAP_EDGE",EDGE,{"disambiguationData":[OSD([sQuery(id+"F0.wireOp",EDGE,"E139.MirrorC")])],"isStart":true});
            var Q13;
            Q13=makeQuery(id+"F3.opExtrude","CAP_EDGE",EDGE,{"disambiguationData":[OSD([sQuery(id+"F0.wireOp",EDGE,"E138.MirrorC")])],"isStart":true});
            var Q14;
            Q14=makeQuery(id+"F8.opPattern","COPY",FACE,{"derivedFrom":makeQuery(id+"F5.boolean.opBoolean","SPLIT",FACE,{"disambiguationData":[TD([makeQuery(id+"F3.opExtrude","SWEPT_FACE",FACE,{"disambiguationData":[OSD([sQuery(id+"F0.wireOp",EDGE,"E136.MirrorC")])]})])],"derivedFrom":makeQuery(id+"F5.opExtrude","CAP_FACE",FACE,{"disambiguationData":[OSD([sQuery(id+"F0.wireOp",EDGE,"E93.bottom"),sQuery(id+"F0.wireOp",EDGE,"E93.top"),sQuery(id+"F0.wireOp",EDGE,"E93.left"),sQuery(id+"F0.wireOp",EDGE,"E93.right")])],"isStart":true})}),"instanceName":"1"});
            var Q15;
            Q15=makeQuery(id+"F8.opPattern","COPY",FACE,{"derivedFrom":makeQuery(id+"F5.boolean.opBoolean","SPLIT",FACE,{"disambiguationData":[TD([makeQuery(id+"F3.opExtrude","SWEPT_FACE",FACE,{"disambiguationData":[OSD([sQuery(id+"F0.wireOp",EDGE,"E137.MirrorC")])]})])],"derivedFrom":makeQuery(id+"F5.opExtrude","CAP_FACE",FACE,{"disambiguationData":[OSD([sQuery(id+"F0.wireOp",EDGE,"E93.bottom"),sQuery(id+"F0.wireOp",EDGE,"E93.top"),sQuery(id+"F0.wireOp",EDGE,"E93.left"),sQuery(id+"F0.wireOp",EDGE,"E93.right")])],"isStart":true})}),"instanceName":"1"});
            fillet(context, id + "F13", {"entities" : qUnion([Q0, Q1, Q2, Q3, Q4, Q5, Q6, Q7, Q8, Q9, Q10, Q11, Q12, Q13, Q14, Q15]), "radius" : .6 * mm, "tangentPropagation" : true, "allowEdgeOverflow" : false});
        }
    });
